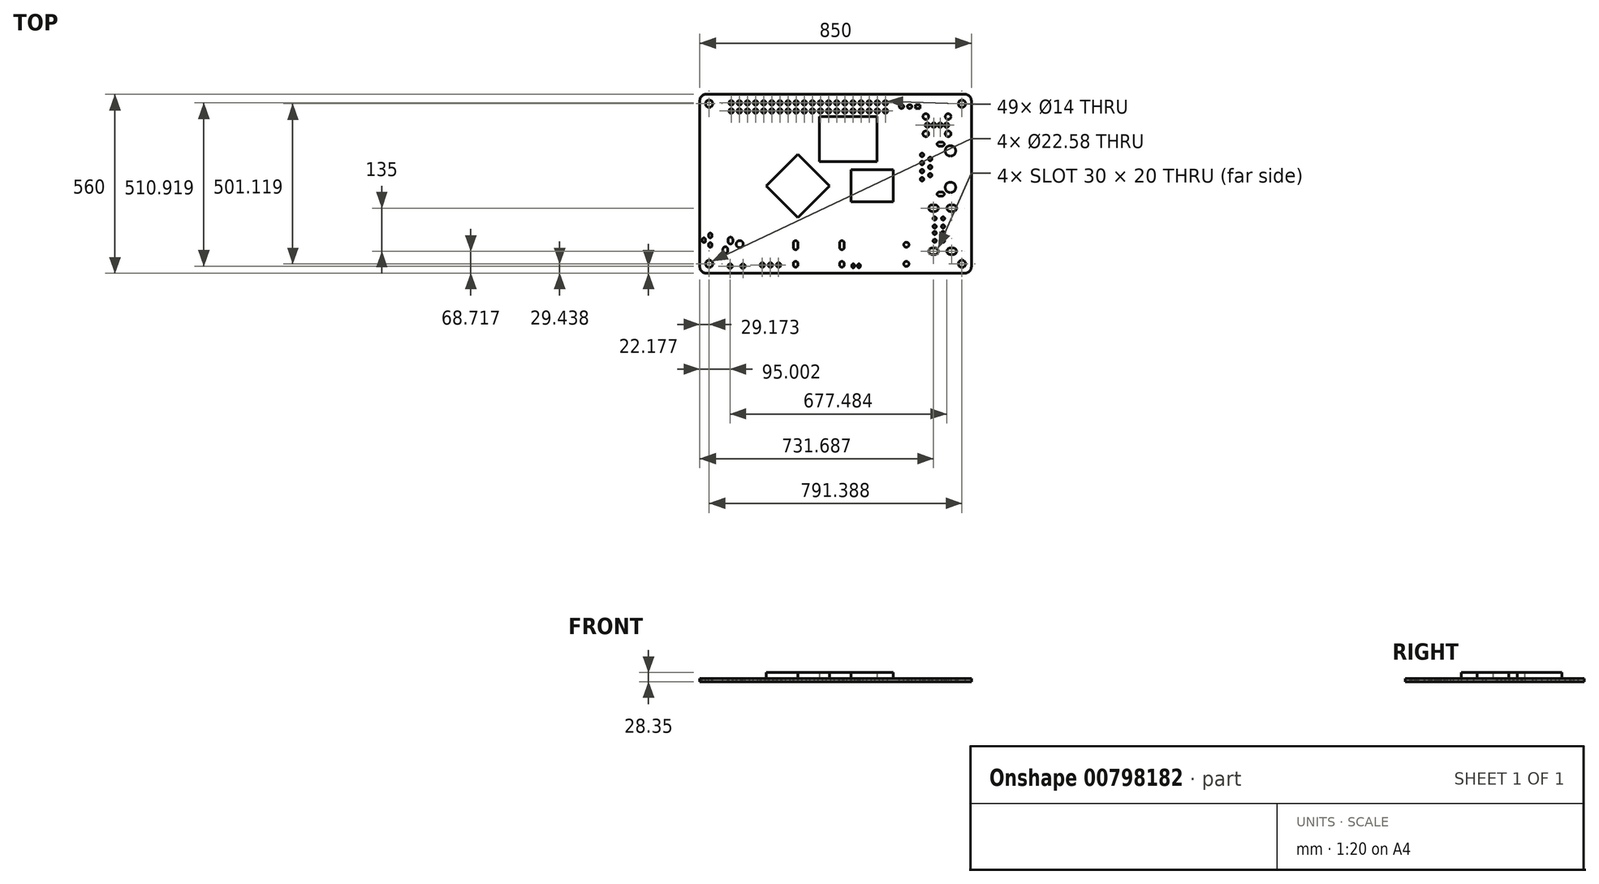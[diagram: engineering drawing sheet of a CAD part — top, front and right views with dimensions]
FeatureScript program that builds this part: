
annotation { "Feature Type Name" : "Feature", "Feature Type Description" : "" }
export const myFeature = defineFeature(function(context is Context, id is Id, definition is map)
    precondition{}
    {
        {
            var Q0;
            Q0=qCreatedBy(makeId("Top.planeOp"),FACE);
            var sketch = newSketch(context, id + "F0", { "sketchPlane" : qUnion([Q0])});
            skCircle(sketch, "E0", {"center": v(1575.33, 490.02) * mm, "radius": 27.56 * mm});
            skCircle(sketch, "E1", {"center": v(1575.33, 390.02) * mm, "radius": 27.56 * mm});
            skCircle(sketch, "E2", {"center": v(1575.33, 67.98) * mm, "radius": 27.56 * mm});
            skCircle(sketch, "E3", {"center": v(1575.33, -32.02) * mm, "radius": 27.56 * mm});
            skCircle(sketch, "E4", {"center": v(1415.5, 454) * mm, "radius": 65 * mm});
            skCircle(sketch, "E5", {"center": v(1415.5, 4) * mm, "radius": 65 * mm});
            skLineSegment(sketch, "E6", {"start": v(1275.73, 560.7) * mm, "end": v(1315.1, 560.7) * mm});
            skArc(sketch, "E7", {"start": v(1315.1, 560.7) * mm, "mid": v(1338.72, 537.07) * mm, "end": v(1315.1, 513.45) * mm});
            skLineSegment(sketch, "E8", {"start": v(1315.1, 513.45) * mm, "end": v(1275.73, 513.45) * mm});
            skArc(sketch, "E9", {"start": v(1275.73, 513.45) * mm, "mid": v(1252.1, 537.07) * mm, "end": v(1275.73, 560.7) * mm});
            skLineSegment(sketch, "E10", {"start": v(1275.73, -55.45) * mm, "end": v(1315.1, -55.45) * mm});
            skArc(sketch, "E11", {"start": v(1315.1, -55.45) * mm, "mid": v(1338.72, -79.07) * mm, "end": v(1315.1, -102.7) * mm});
            skLineSegment(sketch, "E12", {"start": v(1315.1, -102.7) * mm, "end": v(1275.73, -102.7) * mm});
            skArc(sketch, "E13", {"start": v(1275.73, -102.7) * mm, "mid": v(1252.1, -79.07) * mm, "end": v(1275.73, -55.45) * mm});
            skCircle(sketch, "E14", {"center": v(1165.5, 354) * mm, "radius": 21.65 * mm});
            skCircle(sketch, "E15", {"center": v(1165.5, 254) * mm, "radius": 21.65 * mm});
            skCircle(sketch, "E16", {"center": v(1165.5, 154) * mm, "radius": 21.65 * mm});
            skCircle(sketch, "E17", {"center": v(1065.5, 404) * mm, "radius": 21.65 * mm});
            skCircle(sketch, "E18", {"center": v(1065.5, 304) * mm, "radius": 21.65 * mm});
            skCircle(sketch, "E19", {"center": v(1065.5, 204) * mm, "radius": 21.65 * mm});
            skCircle(sketch, "E20", {"center": v(1065.5, 104) * mm, "radius": 21.65 * mm});
            skLineSegment(sketch, "E21", {"start": v(1187.15, 32.35) * mm, "end": v(1143.84, 32.35) * mm});
            skLineSegment(sketch, "E22", {"start": v(1143.84, 32.35) * mm, "end": v(1143.84, 75.65) * mm});
            skLineSegment(sketch, "E23", {"start": v(1143.84, 75.65) * mm, "end": v(1187.15, 75.65) * mm});
            skLineSegment(sketch, "E24", {"start": v(1187.15, 75.65) * mm, "end": v(1187.15, 32.35) * mm});
            skLineSegment(sketch, "E25", {"start": v(1651.71, 484.9) * mm, "end": v(1691.08, 484.9) * mm});
            skLineSegment(sketch, "E26", {"start": v(1671.4, 465.22) * mm, "end": v(1671.4, 504.6) * mm});
            skLineSegment(sketch, "E27", {"start": v(1651.71, -26.9) * mm, "end": v(1691.08, -26.9) * mm});
            skLineSegment(sketch, "E28", {"start": v(1671.4, -46.6) * mm, "end": v(1671.4, -7.22) * mm});
            skLineSegment(sketch, "E29", {"start": v(990.5, -76) * mm, "end": v(1840.5, -76) * mm});
            skLineSegment(sketch, "E30", {"start": v(1840.5, -76) * mm, "end": v(1840.5, 534) * mm});
            skLineSegment(sketch, "E31", {"start": v(1840.5, 534) * mm, "end": v(990.5, 534) * mm});
            skLineSegment(sketch, "E32", {"start": v(990.5, 534) * mm, "end": v(990.5, -76) * mm});
            skLineSegment(sketch, "E33", {"start": v(-197.69, 323.24) * mm, "end": v(-197.69, 874.44) * mm});
            skLineSegment(sketch, "E34", {"start": v(-197.69, 874.44) * mm, "end": v(511.01, 874.44) * mm});
            skLineSegment(sketch, "E35", {"start": v(511.01, 874.44) * mm, "end": v(511.01, 323.24) * mm});
            skLineSegment(sketch, "E36", {"start": v(511.01, 323.24) * mm, "end": v(-197.69, 323.24) * mm});
            skLineSegment(sketch, "E37", {"start": v(-197.39, 356.84) * mm, "end": v(-164.39, 323.84) * mm});
            skLineSegment(sketch, "E38", {"start": v(-164.39, 323.84) * mm, "end": v(-168.39, 323.84) * mm});
            skLineSegment(sketch, "E39", {"start": v(-168.39, 323.84) * mm, "end": v(-195.39, 350.84) * mm});
            skLineSegment(sketch, "E40", {"start": v(-195.39, 350.84) * mm, "end": v(-195.39, 346.84) * mm});
            skLineSegment(sketch, "E41", {"start": v(-195.39, 346.84) * mm, "end": v(-173.39, 324.84) * mm});
            skLineSegment(sketch, "E42", {"start": v(-173.39, 324.84) * mm, "end": v(-178.39, 324.84) * mm});
            skLineSegment(sketch, "E43", {"start": v(-178.39, 324.84) * mm, "end": v(-196.39, 342.84) * mm});
            skLineSegment(sketch, "E44", {"start": v(-196.39, 342.84) * mm, "end": v(-196.39, 337.84) * mm});
            skLineSegment(sketch, "E45", {"start": v(-196.39, 337.84) * mm, "end": v(-182.39, 323.84) * mm});
            skLineSegment(sketch, "E46", {"start": v(-182.39, 323.84) * mm, "end": v(-188.39, 323.84) * mm});
            skLineSegment(sketch, "E47", {"start": v(-188.39, 323.84) * mm, "end": v(-196.39, 331.84) * mm});
            skLineSegment(sketch, "E48", {"start": v(-196.39, 331.84) * mm, "end": v(-196.39, 328.84) * mm});
            skLineSegment(sketch, "E49", {"start": v(-196.39, 328.84) * mm, "end": v(-191.39, 323.84) * mm});
            skArc(sketch, "E50", {"start": v(1771.65, -246.84) * mm, "mid": v(1785.56, -252.6) * mm, "end": v(1791.32, -266.52) * mm});
            skArc(sketch, "E51", {"start": v(1791.32, -266.52) * mm, "mid": v(1785.56, -280.44) * mm, "end": v(1771.65, -286.2) * mm});
            skArc(sketch, "E52", {"start": v(1771.65, -286.2) * mm, "mid": v(1757.73, -280.44) * mm, "end": v(1751.97, -266.52) * mm});
            skArc(sketch, "E53", {"start": v(1751.97, -266.52) * mm, "mid": v(1757.73, -252.6) * mm, "end": v(1771.65, -246.84) * mm});
            skArc(sketch, "E54", {"start": v(1732.28, -660.25) * mm, "mid": v(1743.8, -632.41) * mm, "end": v(1771.64, -620.88) * mm});
            skArc(sketch, "E55", {"start": v(1771.65, -620.88) * mm, "mid": v(1799.48, -632.41) * mm, "end": v(1811.01, -660.25) * mm});
            skArc(sketch, "E56", {"start": v(1771.65, -699.62) * mm, "mid": v(1743.8, -688.1) * mm, "end": v(1732.28, -660.25) * mm});
            skArc(sketch, "E57", {"start": v(1811.01, -660.25) * mm, "mid": v(1799.48, -688.1) * mm, "end": v(1771.64, -699.62) * mm});
            skLineSegment(sketch, "E58", {"start": v(-1594.49, 1150.77) * mm, "end": v(1594.49, 1150.77) * mm});
            skArc(sketch, "E59", {"start": v(1594.49, 1150.77) * mm, "mid": v(1650.16, 1127.7) * mm, "end": v(1673.22, 1072.03) * mm});
            skLineSegment(sketch, "E60", {"start": v(1673.22, 1072.03) * mm, "end": v(1673.22, -975.21) * mm});
            skArc(sketch, "E61", {"start": v(1673.22, -975.21) * mm, "mid": v(1650.16, -1030.89) * mm, "end": v(1594.49, -1053.95) * mm});
            skLineSegment(sketch, "E62", {"start": v(1594.49, -1053.95) * mm, "end": v(-1594.49, -1053.95) * mm});
            skArc(sketch, "E63", {"start": v(-1594.49, -1053.95) * mm, "mid": v(-1650.16, -1030.89) * mm, "end": v(-1673.22, -975.21) * mm});
            skArc(sketch, "E64", {"start": v(-1673.22, 1072.03) * mm, "mid": v(-1650.16, 1127.7) * mm, "end": v(-1594.49, 1150.77) * mm});
            skLineSegment(sketch, "E65", {"start": v(-1629.3, 698.95) * mm, "end": v(-1629.3, 738.32) * mm});
            skLineSegment(sketch, "E66", {"start": v(-1629.3, 738.32) * mm, "end": v(-1550.56, 738.32) * mm});
            skLineSegment(sketch, "E67", {"start": v(-1550.56, 738.32) * mm, "end": v(-1550.56, 698.95) * mm});
            skLineSegment(sketch, "E68", {"start": v(-1550.56, 698.95) * mm, "end": v(-1629.3, 698.95) * mm});
            skLineSegment(sketch, "E69", {"start": v(-1629.3, 815.1) * mm, "end": v(-1629.3, 854.46) * mm});
            skLineSegment(sketch, "E70", {"start": v(-1629.3, 854.46) * mm, "end": v(-1550.56, 854.46) * mm});
            skLineSegment(sketch, "E71", {"start": v(-1550.56, 854.46) * mm, "end": v(-1550.56, 815.1) * mm});
            skLineSegment(sketch, "E72", {"start": v(-1550.56, 815.1) * mm, "end": v(-1629.3, 815.1) * mm});
            skLineSegment(sketch, "E73", {"start": v(-1545.55, 756.04) * mm, "end": v(-1545.55, 797.38) * mm});
            skLineSegment(sketch, "E74", {"start": v(-1545.55, 797.38) * mm, "end": v(-1506.18, 797.38) * mm});
            skLineSegment(sketch, "E75", {"start": v(-1506.18, 797.38) * mm, "end": v(-1506.18, 756.04) * mm});
            skLineSegment(sketch, "E76", {"start": v(-1506.18, 756.04) * mm, "end": v(-1545.55, 756.04) * mm});
            skLineSegment(sketch, "E77", {"start": v(-197.36, -502.66) * mm, "end": v(-181.38, -502.66) * mm});
            skLineSegment(sketch, "E78", {"start": v(-181.38, -502.66) * mm, "end": v(-181.38, -542.66) * mm});
            skLineSegment(sketch, "E79", {"start": v(-181.38, -542.66) * mm, "end": v(-197.36, -542.66) * mm});
            skLineSegment(sketch, "E80", {"start": v(-197.36, -542.66) * mm, "end": v(-197.36, -502.66) * mm});
            skLineSegment(sketch, "E81", {"start": v(-154.92, -502.97) * mm, "end": v(-145.08, -502.97) * mm});
            skLineSegment(sketch, "E82", {"start": v(-145.08, -502.97) * mm, "end": v(-145.08, -542.34) * mm});
            skLineSegment(sketch, "E83", {"start": v(-145.08, -542.34) * mm, "end": v(-154.92, -542.34) * mm});
            skLineSegment(sketch, "E84", {"start": v(-154.92, -542.34) * mm, "end": v(-154.92, -502.97) * mm});
            skLineSegment(sketch, "E85", {"start": v(-174.6, -502.97) * mm, "end": v(-164.76, -502.97) * mm});
            skLineSegment(sketch, "E86", {"start": v(-164.76, -502.97) * mm, "end": v(-164.76, -542.34) * mm});
            skLineSegment(sketch, "E87", {"start": v(-164.76, -542.34) * mm, "end": v(-174.6, -542.34) * mm});
            skLineSegment(sketch, "E88", {"start": v(-174.6, -542.34) * mm, "end": v(-174.6, -502.97) * mm});
            skLineSegment(sketch, "E89", {"start": v(-213.98, -550.2) * mm, "end": v(-204.14, -550.2) * mm});
            skLineSegment(sketch, "E90", {"start": v(-204.14, -550.2) * mm, "end": v(-204.14, -589.58) * mm});
            skLineSegment(sketch, "E91", {"start": v(-204.14, -589.58) * mm, "end": v(-213.98, -589.58) * mm});
            skLineSegment(sketch, "E92", {"start": v(-213.98, -589.58) * mm, "end": v(-213.98, -550.2) * mm});
            skLineSegment(sketch, "E93", {"start": v(-154.92, -550.2) * mm, "end": v(-145.08, -550.2) * mm});
            skLineSegment(sketch, "E94", {"start": v(-145.08, -550.2) * mm, "end": v(-145.08, -589.58) * mm});
            skLineSegment(sketch, "E95", {"start": v(-145.08, -589.58) * mm, "end": v(-154.92, -589.58) * mm});
            skLineSegment(sketch, "E96", {"start": v(-154.92, -589.58) * mm, "end": v(-154.92, -550.2) * mm});
            skLineSegment(sketch, "E97", {"start": v(-174.6, -550.2) * mm, "end": v(-164.76, -550.2) * mm});
            skLineSegment(sketch, "E98", {"start": v(-164.76, -550.2) * mm, "end": v(-164.76, -589.58) * mm});
            skLineSegment(sketch, "E99", {"start": v(-164.76, -589.58) * mm, "end": v(-174.6, -589.58) * mm});
            skLineSegment(sketch, "E100", {"start": v(-174.6, -589.58) * mm, "end": v(-174.6, -550.2) * mm});
            skLineSegment(sketch, "E101", {"start": v(-213.98, -502.97) * mm, "end": v(-204.14, -502.97) * mm});
            skLineSegment(sketch, "E102", {"start": v(-204.14, -502.97) * mm, "end": v(-204.14, -542.34) * mm});
            skLineSegment(sketch, "E103", {"start": v(-204.14, -542.34) * mm, "end": v(-213.98, -542.34) * mm});
            skLineSegment(sketch, "E104", {"start": v(-213.98, -542.34) * mm, "end": v(-213.98, -502.97) * mm});
            skLineSegment(sketch, "E105", {"start": v(-233.66, -502.97) * mm, "end": v(-223.82, -502.97) * mm});
            skLineSegment(sketch, "E106", {"start": v(-223.82, -502.97) * mm, "end": v(-223.82, -542.34) * mm});
            skLineSegment(sketch, "E107", {"start": v(-223.82, -542.34) * mm, "end": v(-233.66, -542.34) * mm});
            skLineSegment(sketch, "E108", {"start": v(-233.66, -542.34) * mm, "end": v(-233.66, -502.97) * mm});
            skLineSegment(sketch, "E109", {"start": v(-233.66, -550.2) * mm, "end": v(-223.82, -550.2) * mm});
            skLineSegment(sketch, "E110", {"start": v(-223.82, -550.2) * mm, "end": v(-223.82, -589.58) * mm});
            skLineSegment(sketch, "E111", {"start": v(-223.82, -589.58) * mm, "end": v(-233.66, -589.58) * mm});
            skLineSegment(sketch, "E112", {"start": v(-233.66, -589.58) * mm, "end": v(-233.66, -550.2) * mm});
            skLineSegment(sketch, "E113", {"start": v(-197.36, -549.9) * mm, "end": v(-181.38, -549.9) * mm});
            skLineSegment(sketch, "E114", {"start": v(-181.38, -549.9) * mm, "end": v(-181.38, -589.9) * mm});
            skLineSegment(sketch, "E115", {"start": v(-181.38, -589.9) * mm, "end": v(-197.36, -589.9) * mm});
            skLineSegment(sketch, "E116", {"start": v(-197.36, -589.9) * mm, "end": v(-197.36, -549.9) * mm});
            skLineSegment(sketch, "E117", {"start": v(-142.13, -526.59) * mm, "end": v(-140.16, -526.59) * mm});
            skLineSegment(sketch, "E118", {"start": v(-140.16, -526.59) * mm, "end": v(-140.16, -565.96) * mm});
            skLineSegment(sketch, "E119", {"start": v(-140.16, -565.96) * mm, "end": v(-142.13, -565.96) * mm});
            skLineSegment(sketch, "E120", {"start": v(-150, -495.1) * mm, "end": v(-140.16, -485.25) * mm});
            skLineSegment(sketch, "E121", {"start": v(-140.16, -485.25) * mm, "end": v(-159.84, -485.25) * mm});
            skLineSegment(sketch, "E122", {"start": v(-159.84, -485.25) * mm, "end": v(-150, -495.1) * mm});
            skLineSegment(sketch, "E123", {"start": v(-236.6, -526.59) * mm, "end": v(-238.58, -526.59) * mm});
            skLineSegment(sketch, "E124", {"start": v(-238.58, -526.59) * mm, "end": v(-238.58, -565.96) * mm});
            skLineSegment(sketch, "E125", {"start": v(-238.58, -565.96) * mm, "end": v(-236.6, -565.96) * mm});
            skLineSegment(sketch, "E126", {"start": v(-92.36, -502.54) * mm, "end": v(-76.38, -502.54) * mm});
            skLineSegment(sketch, "E127", {"start": v(-76.38, -502.54) * mm, "end": v(-76.38, -542.54) * mm});
            skLineSegment(sketch, "E128", {"start": v(-76.38, -542.54) * mm, "end": v(-92.36, -542.54) * mm});
            skLineSegment(sketch, "E129", {"start": v(-92.36, -542.54) * mm, "end": v(-92.36, -502.54) * mm});
            skLineSegment(sketch, "E130", {"start": v(-49.92, -502.85) * mm, "end": v(-40.08, -502.85) * mm});
            skLineSegment(sketch, "E131", {"start": v(-40.08, -502.85) * mm, "end": v(-40.08, -542.22) * mm});
            skLineSegment(sketch, "E132", {"start": v(-40.08, -542.22) * mm, "end": v(-49.92, -542.22) * mm});
            skLineSegment(sketch, "E133", {"start": v(-49.92, -542.22) * mm, "end": v(-49.92, -502.85) * mm});
            skLineSegment(sketch, "E134", {"start": v(-69.6, -502.85) * mm, "end": v(-59.76, -502.85) * mm});
            skLineSegment(sketch, "E135", {"start": v(-59.76, -502.85) * mm, "end": v(-59.76, -542.22) * mm});
            skLineSegment(sketch, "E136", {"start": v(-59.76, -542.22) * mm, "end": v(-69.6, -542.22) * mm});
            skLineSegment(sketch, "E137", {"start": v(-69.6, -542.22) * mm, "end": v(-69.6, -502.85) * mm});
            skLineSegment(sketch, "E138", {"start": v(-108.98, -550.09) * mm, "end": v(-99.14, -550.09) * mm});
            skLineSegment(sketch, "E139", {"start": v(-99.14, -550.09) * mm, "end": v(-99.14, -589.46) * mm});
            skLineSegment(sketch, "E140", {"start": v(-99.14, -589.46) * mm, "end": v(-108.98, -589.46) * mm});
            skLineSegment(sketch, "E141", {"start": v(-108.98, -589.46) * mm, "end": v(-108.98, -550.09) * mm});
            skLineSegment(sketch, "E142", {"start": v(-49.92, -550.09) * mm, "end": v(-40.08, -550.09) * mm});
            skLineSegment(sketch, "E143", {"start": v(-40.08, -550.09) * mm, "end": v(-40.08, -589.46) * mm});
            skLineSegment(sketch, "E144", {"start": v(-40.08, -589.46) * mm, "end": v(-49.92, -589.46) * mm});
            skLineSegment(sketch, "E145", {"start": v(-49.92, -589.46) * mm, "end": v(-49.92, -550.09) * mm});
            skLineSegment(sketch, "E146", {"start": v(-69.6, -550.09) * mm, "end": v(-59.76, -550.09) * mm});
            skLineSegment(sketch, "E147", {"start": v(-59.76, -550.09) * mm, "end": v(-59.76, -589.46) * mm});
            skLineSegment(sketch, "E148", {"start": v(-59.76, -589.46) * mm, "end": v(-69.6, -589.46) * mm});
            skLineSegment(sketch, "E149", {"start": v(-69.6, -589.46) * mm, "end": v(-69.6, -550.09) * mm});
            skLineSegment(sketch, "E150", {"start": v(-108.98, -502.85) * mm, "end": v(-99.14, -502.85) * mm});
            skLineSegment(sketch, "E151", {"start": v(-99.14, -502.85) * mm, "end": v(-99.14, -542.22) * mm});
            skLineSegment(sketch, "E152", {"start": v(-99.14, -542.22) * mm, "end": v(-108.98, -542.22) * mm});
            skLineSegment(sketch, "E153", {"start": v(-108.98, -542.22) * mm, "end": v(-108.98, -502.85) * mm});
            skLineSegment(sketch, "E154", {"start": v(-128.66, -502.85) * mm, "end": v(-118.82, -502.85) * mm});
            skLineSegment(sketch, "E155", {"start": v(-118.82, -502.85) * mm, "end": v(-118.82, -542.22) * mm});
            skLineSegment(sketch, "E156", {"start": v(-118.82, -542.22) * mm, "end": v(-128.66, -542.22) * mm});
            skLineSegment(sketch, "E157", {"start": v(-128.66, -542.22) * mm, "end": v(-128.66, -502.85) * mm});
            skLineSegment(sketch, "E158", {"start": v(-128.66, -550.09) * mm, "end": v(-118.82, -550.09) * mm});
            skLineSegment(sketch, "E159", {"start": v(-118.82, -550.09) * mm, "end": v(-118.82, -589.46) * mm});
            skLineSegment(sketch, "E160", {"start": v(-118.82, -589.46) * mm, "end": v(-128.66, -589.46) * mm});
            skLineSegment(sketch, "E161", {"start": v(-128.66, -589.46) * mm, "end": v(-128.66, -550.09) * mm});
            skLineSegment(sketch, "E162", {"start": v(-92.36, -549.77) * mm, "end": v(-76.38, -549.77) * mm});
            skLineSegment(sketch, "E163", {"start": v(-76.38, -549.77) * mm, "end": v(-76.38, -589.77) * mm});
            skLineSegment(sketch, "E164", {"start": v(-76.38, -589.77) * mm, "end": v(-92.36, -589.77) * mm});
            skLineSegment(sketch, "E165", {"start": v(-92.36, -589.77) * mm, "end": v(-92.36, -549.77) * mm});
            skLineSegment(sketch, "E166", {"start": v(-37.13, -526.47) * mm, "end": v(-35.16, -526.47) * mm});
            skLineSegment(sketch, "E167", {"start": v(-35.16, -526.47) * mm, "end": v(-35.16, -565.85) * mm});
            skLineSegment(sketch, "E168", {"start": v(-35.16, -565.85) * mm, "end": v(-37.13, -565.85) * mm});
            skLineSegment(sketch, "E169", {"start": v(-45, -494.98) * mm, "end": v(-35.16, -485.14) * mm});
            skLineSegment(sketch, "E170", {"start": v(-35.16, -485.14) * mm, "end": v(-54.84, -485.14) * mm});
            skLineSegment(sketch, "E171", {"start": v(-54.84, -485.14) * mm, "end": v(-45, -494.98) * mm});
            skLineSegment(sketch, "E172", {"start": v(-131.6, -526.47) * mm, "end": v(-133.58, -526.47) * mm});
            skLineSegment(sketch, "E173", {"start": v(-133.58, -526.47) * mm, "end": v(-133.58, -565.85) * mm});
            skLineSegment(sketch, "E174", {"start": v(-133.58, -565.85) * mm, "end": v(-131.6, -565.85) * mm});
            skLineSegment(sketch, "E175", {"start": v(-1042.38, 782.65) * mm, "end": v(-1042.38, 773.6) * mm});
            skLineSegment(sketch, "E176", {"start": v(-1042.38, 773.6) * mm, "end": v(-1073.88, 773.6) * mm});
            skLineSegment(sketch, "E177", {"start": v(-1073.88, 773.6) * mm, "end": v(-1073.88, 782.65) * mm});
            skLineSegment(sketch, "E178", {"start": v(-1073.88, 782.65) * mm, "end": v(-1042.38, 782.65) * mm});
            skLineSegment(sketch, "E179", {"start": v(-1042.38, 762.97) * mm, "end": v(-1042.38, 753.91) * mm});
            skLineSegment(sketch, "E180", {"start": v(-1042.38, 753.91) * mm, "end": v(-1073.88, 753.91) * mm});
            skLineSegment(sketch, "E181", {"start": v(-1073.88, 753.91) * mm, "end": v(-1073.88, 762.97) * mm});
            skLineSegment(sketch, "E182", {"start": v(-1073.88, 762.97) * mm, "end": v(-1042.38, 762.97) * mm});
            skLineSegment(sketch, "E183", {"start": v(-1042.38, 743.28) * mm, "end": v(-1042.38, 734.22) * mm});
            skLineSegment(sketch, "E184", {"start": v(-1042.38, 734.22) * mm, "end": v(-1073.88, 734.22) * mm});
            skLineSegment(sketch, "E185", {"start": v(-1073.88, 734.22) * mm, "end": v(-1073.88, 743.28) * mm});
            skLineSegment(sketch, "E186", {"start": v(-1073.88, 743.28) * mm, "end": v(-1042.38, 743.28) * mm});
            skLineSegment(sketch, "E187", {"start": v(-1042.38, 723.6) * mm, "end": v(-1042.38, 714.54) * mm});
            skLineSegment(sketch, "E188", {"start": v(-1042.38, 714.54) * mm, "end": v(-1073.88, 714.54) * mm});
            skLineSegment(sketch, "E189", {"start": v(-1073.88, 714.54) * mm, "end": v(-1073.88, 723.6) * mm});
            skLineSegment(sketch, "E190", {"start": v(-1073.88, 723.6) * mm, "end": v(-1042.38, 723.6) * mm});
            skLineSegment(sketch, "E191", {"start": v(-1042.38, 703.91) * mm, "end": v(-1042.38, 694.85) * mm});
            skLineSegment(sketch, "E192", {"start": v(-1042.38, 694.85) * mm, "end": v(-1073.88, 694.85) * mm});
            skLineSegment(sketch, "E193", {"start": v(-1073.88, 694.85) * mm, "end": v(-1073.88, 703.91) * mm});
            skLineSegment(sketch, "E194", {"start": v(-1073.88, 703.91) * mm, "end": v(-1042.38, 703.91) * mm});
            skLineSegment(sketch, "E195", {"start": v(-1042.38, 684.23) * mm, "end": v(-1042.38, 675.17) * mm});
            skLineSegment(sketch, "E196", {"start": v(-1042.38, 675.17) * mm, "end": v(-1073.88, 675.17) * mm});
            skLineSegment(sketch, "E197", {"start": v(-1073.88, 675.17) * mm, "end": v(-1073.88, 684.23) * mm});
            skLineSegment(sketch, "E198", {"start": v(-1073.88, 684.23) * mm, "end": v(-1042.38, 684.23) * mm});
            skLineSegment(sketch, "E199", {"start": v(-1092.2, 665.92) * mm, "end": v(-1083.13, 665.92) * mm});
            skLineSegment(sketch, "E200", {"start": v(-1083.13, 665.92) * mm, "end": v(-1083.13, 634.42) * mm});
            skLineSegment(sketch, "E201", {"start": v(-1083.13, 634.42) * mm, "end": v(-1092.2, 634.42) * mm});
            skLineSegment(sketch, "E202", {"start": v(-1092.2, 634.42) * mm, "end": v(-1092.2, 665.92) * mm});
            skLineSegment(sketch, "E203", {"start": v(-1111.87, 665.92) * mm, "end": v(-1102.81, 665.92) * mm});
            skLineSegment(sketch, "E204", {"start": v(-1102.81, 665.92) * mm, "end": v(-1102.81, 634.42) * mm});
            skLineSegment(sketch, "E205", {"start": v(-1102.81, 634.42) * mm, "end": v(-1111.87, 634.42) * mm});
            skLineSegment(sketch, "E206", {"start": v(-1111.87, 634.42) * mm, "end": v(-1111.87, 665.92) * mm});
            skLineSegment(sketch, "E207", {"start": v(-1131.56, 665.92) * mm, "end": v(-1122.5, 665.92) * mm});
            skLineSegment(sketch, "E208", {"start": v(-1122.5, 665.92) * mm, "end": v(-1122.5, 634.42) * mm});
            skLineSegment(sketch, "E209", {"start": v(-1122.5, 634.42) * mm, "end": v(-1131.56, 634.42) * mm});
            skLineSegment(sketch, "E210", {"start": v(-1131.56, 634.42) * mm, "end": v(-1131.56, 665.92) * mm});
            skLineSegment(sketch, "E211", {"start": v(-1151.24, 665.92) * mm, "end": v(-1142.18, 665.92) * mm});
            skLineSegment(sketch, "E212", {"start": v(-1142.18, 665.92) * mm, "end": v(-1142.18, 634.42) * mm});
            skLineSegment(sketch, "E213", {"start": v(-1142.18, 634.42) * mm, "end": v(-1151.24, 634.42) * mm});
            skLineSegment(sketch, "E214", {"start": v(-1151.24, 634.42) * mm, "end": v(-1151.24, 665.92) * mm});
            skLineSegment(sketch, "E215", {"start": v(-1170.93, 665.92) * mm, "end": v(-1161.87, 665.92) * mm});
            skLineSegment(sketch, "E216", {"start": v(-1161.87, 665.92) * mm, "end": v(-1161.87, 634.42) * mm});
            skLineSegment(sketch, "E217", {"start": v(-1161.87, 634.42) * mm, "end": v(-1170.93, 634.42) * mm});
            skLineSegment(sketch, "E218", {"start": v(-1170.93, 634.42) * mm, "end": v(-1170.93, 665.92) * mm});
            skLineSegment(sketch, "E219", {"start": v(-1190.61, 665.92) * mm, "end": v(-1181.55, 665.92) * mm});
            skLineSegment(sketch, "E220", {"start": v(-1181.55, 665.92) * mm, "end": v(-1181.55, 634.42) * mm});
            skLineSegment(sketch, "E221", {"start": v(-1181.55, 634.42) * mm, "end": v(-1190.61, 634.42) * mm});
            skLineSegment(sketch, "E222", {"start": v(-1190.61, 634.42) * mm, "end": v(-1190.61, 665.92) * mm});
            skLineSegment(sketch, "E223", {"start": v(-1199.86, 684.23) * mm, "end": v(-1199.86, 675.17) * mm});
            skLineSegment(sketch, "E224", {"start": v(-1199.86, 675.17) * mm, "end": v(-1231.36, 675.17) * mm});
            skLineSegment(sketch, "E225", {"start": v(-1231.36, 675.17) * mm, "end": v(-1231.36, 684.23) * mm});
            skLineSegment(sketch, "E226", {"start": v(-1231.36, 684.23) * mm, "end": v(-1199.86, 684.23) * mm});
            skLineSegment(sketch, "E227", {"start": v(-1199.86, 703.91) * mm, "end": v(-1199.86, 694.85) * mm});
            skLineSegment(sketch, "E228", {"start": v(-1199.86, 694.85) * mm, "end": v(-1231.36, 694.85) * mm});
            skLineSegment(sketch, "E229", {"start": v(-1231.36, 694.85) * mm, "end": v(-1231.36, 703.91) * mm});
            skLineSegment(sketch, "E230", {"start": v(-1231.36, 703.91) * mm, "end": v(-1199.86, 703.91) * mm});
            skLineSegment(sketch, "E231", {"start": v(-1199.86, 723.6) * mm, "end": v(-1199.86, 714.54) * mm});
            skLineSegment(sketch, "E232", {"start": v(-1199.86, 714.54) * mm, "end": v(-1231.36, 714.54) * mm});
            skLineSegment(sketch, "E233", {"start": v(-1231.36, 714.54) * mm, "end": v(-1231.36, 723.6) * mm});
            skLineSegment(sketch, "E234", {"start": v(-1231.36, 723.6) * mm, "end": v(-1199.86, 723.6) * mm});
            skLineSegment(sketch, "E235", {"start": v(-1199.86, 743.28) * mm, "end": v(-1199.86, 734.22) * mm});
            skLineSegment(sketch, "E236", {"start": v(-1199.86, 734.22) * mm, "end": v(-1231.36, 734.22) * mm});
            skLineSegment(sketch, "E237", {"start": v(-1231.36, 734.22) * mm, "end": v(-1231.36, 743.28) * mm});
            skLineSegment(sketch, "E238", {"start": v(-1231.36, 743.28) * mm, "end": v(-1199.86, 743.28) * mm});
            skLineSegment(sketch, "E239", {"start": v(-1199.86, 762.97) * mm, "end": v(-1199.86, 753.91) * mm});
            skLineSegment(sketch, "E240", {"start": v(-1199.86, 753.91) * mm, "end": v(-1231.36, 753.91) * mm});
            skLineSegment(sketch, "E241", {"start": v(-1231.36, 753.91) * mm, "end": v(-1231.36, 762.97) * mm});
            skLineSegment(sketch, "E242", {"start": v(-1231.36, 762.97) * mm, "end": v(-1199.86, 762.97) * mm});
            skLineSegment(sketch, "E243", {"start": v(-1199.86, 782.65) * mm, "end": v(-1199.86, 773.6) * mm});
            skLineSegment(sketch, "E244", {"start": v(-1199.86, 773.6) * mm, "end": v(-1231.36, 773.6) * mm});
            skLineSegment(sketch, "E245", {"start": v(-1231.36, 773.6) * mm, "end": v(-1231.36, 782.65) * mm});
            skLineSegment(sketch, "E246", {"start": v(-1231.36, 782.65) * mm, "end": v(-1199.86, 782.65) * mm});
            skLineSegment(sketch, "E247", {"start": v(-1190.61, 823.4) * mm, "end": v(-1181.55, 823.4) * mm});
            skLineSegment(sketch, "E248", {"start": v(-1181.55, 823.4) * mm, "end": v(-1181.55, 791.9) * mm});
            skLineSegment(sketch, "E249", {"start": v(-1181.55, 791.9) * mm, "end": v(-1190.61, 791.9) * mm});
            skLineSegment(sketch, "E250", {"start": v(-1190.61, 791.9) * mm, "end": v(-1190.61, 823.4) * mm});
            skLineSegment(sketch, "E251", {"start": v(-1170.93, 823.4) * mm, "end": v(-1161.87, 823.4) * mm});
            skLineSegment(sketch, "E252", {"start": v(-1161.87, 823.4) * mm, "end": v(-1161.87, 791.9) * mm});
            skLineSegment(sketch, "E253", {"start": v(-1161.87, 791.9) * mm, "end": v(-1170.93, 791.9) * mm});
            skLineSegment(sketch, "E254", {"start": v(-1170.93, 791.9) * mm, "end": v(-1170.93, 823.4) * mm});
            skLineSegment(sketch, "E255", {"start": v(-1151.24, 823.4) * mm, "end": v(-1142.18, 823.4) * mm});
            skLineSegment(sketch, "E256", {"start": v(-1142.18, 823.4) * mm, "end": v(-1142.18, 791.9) * mm});
            skLineSegment(sketch, "E257", {"start": v(-1142.18, 791.9) * mm, "end": v(-1151.24, 791.9) * mm});
            skLineSegment(sketch, "E258", {"start": v(-1151.24, 791.9) * mm, "end": v(-1151.24, 823.4) * mm});
            skLineSegment(sketch, "E259", {"start": v(-1131.56, 823.4) * mm, "end": v(-1122.5, 823.4) * mm});
            skLineSegment(sketch, "E260", {"start": v(-1122.5, 823.4) * mm, "end": v(-1122.5, 791.9) * mm});
            skLineSegment(sketch, "E261", {"start": v(-1122.5, 791.9) * mm, "end": v(-1131.56, 791.9) * mm});
            skLineSegment(sketch, "E262", {"start": v(-1131.56, 791.9) * mm, "end": v(-1131.56, 823.4) * mm});
            skLineSegment(sketch, "E263", {"start": v(-1111.87, 823.4) * mm, "end": v(-1102.81, 823.4) * mm});
            skLineSegment(sketch, "E264", {"start": v(-1102.81, 823.4) * mm, "end": v(-1102.81, 791.9) * mm});
            skLineSegment(sketch, "E265", {"start": v(-1102.81, 791.9) * mm, "end": v(-1111.87, 791.9) * mm});
            skLineSegment(sketch, "E266", {"start": v(-1111.87, 791.9) * mm, "end": v(-1111.87, 823.4) * mm});
            skLineSegment(sketch, "E267", {"start": v(-1092.2, 823.4) * mm, "end": v(-1083.13, 823.4) * mm});
            skLineSegment(sketch, "E268", {"start": v(-1083.13, 823.4) * mm, "end": v(-1083.13, 791.9) * mm});
            skLineSegment(sketch, "E269", {"start": v(-1083.13, 791.9) * mm, "end": v(-1092.2, 791.9) * mm});
            skLineSegment(sketch, "E270", {"start": v(-1092.2, 791.9) * mm, "end": v(-1092.2, 823.4) * mm});
            skLineSegment(sketch, "E271", {"start": v(-1093.57, 772.22) * mm, "end": v(-1093.57, 685.6) * mm});
            skLineSegment(sketch, "E272", {"start": v(-1093.57, 685.6) * mm, "end": v(-1180.18, 685.6) * mm});
            skLineSegment(sketch, "E273", {"start": v(-1180.18, 685.6) * mm, "end": v(-1180.18, 772.22) * mm});
            skLineSegment(sketch, "E274", {"start": v(-1180.18, 772.22) * mm, "end": v(-1093.57, 772.22) * mm});
            skLineSegment(sketch, "E275", {"start": v(-1226.12, 792.85) * mm, "end": v(-1226.12, 817.85) * mm});
            skLineSegment(sketch, "E276", {"start": v(-1226.12, 817.85) * mm, "end": v(-1201.12, 817.85) * mm});
            skLineSegment(sketch, "E277", {"start": v(-1047.63, 664.98) * mm, "end": v(-1047.63, 639.98) * mm});
            skLineSegment(sketch, "E278", {"start": v(-1047.63, 639.98) * mm, "end": v(-1072.63, 639.98) * mm});
            skLineSegment(sketch, "E279", {"start": v(-1201.87, 638.91) * mm, "end": v(-1226.87, 638.91) * mm});
            skLineSegment(sketch, "E280", {"start": v(-1226.87, 638.91) * mm, "end": v(-1226.87, 663.91) * mm});
            skArc(sketch, "E281", {"start": v(-1041.06, 813.91) * mm, "mid": v(-1056.87, 829.73) * mm, "end": v(-1072.68, 813.91) * mm});
            skArc(sketch, "E282", {"start": v(-1072.68, 813.91) * mm, "mid": v(-1056.87, 798.1) * mm, "end": v(-1041.06, 813.91) * mm});
            skLineSegment(sketch, "E283", {"start": v(188.84, -153.65) * mm, "end": v(188.84, -173.48) * mm});
            skLineSegment(sketch, "E284", {"start": v(188.84, -173.48) * mm, "end": v(712.46, -173.48) * mm});
            skLineSegment(sketch, "E285", {"start": v(712.46, -173.48) * mm, "end": v(712.46, -153.65) * mm});
            skLineSegment(sketch, "E286", {"start": v(188.84, -153.65) * mm, "end": v(188.84, 200.68) * mm});
            skLineSegment(sketch, "E287", {"start": v(712.46, 200.68) * mm, "end": v(712.46, -153.65) * mm});
            skLineSegment(sketch, "E288", {"start": v(188.84, 200.68) * mm, "end": v(188.84, 220.52) * mm});
            skLineSegment(sketch, "E289", {"start": v(188.84, 220.52) * mm, "end": v(712.46, 220.52) * mm});
            skLineSegment(sketch, "E290", {"start": v(712.46, 220.52) * mm, "end": v(712.46, 200.68) * mm});
            skArc(sketch, "E291", {"start": v(164.23, -183.18) * mm, "mid": v(159.31, -188.1) * mm, "end": v(154.4, -183.17) * mm});
            skArc(sketch, "E292", {"start": v(154.4, -183.17) * mm, "mid": v(159.31, -178.26) * mm, "end": v(164.23, -183.18) * mm});
            skLineSegment(sketch, "E293", {"start": v(196.71, -173.48) * mm, "end": v(188.84, -165.6) * mm});
            skLineSegment(sketch, "E294", {"start": v(204.58, -173.48) * mm, "end": v(188.84, -157.73) * mm});
            skLineSegment(sketch, "E295", {"start": v(-464.29, -366.24) * mm, "end": v(-74.53, 23.52) * mm});
            skLineSegment(sketch, "E296", {"start": v(-74.53, 23.52) * mm, "end": v(-464.28, 413.27) * mm});
            skLineSegment(sketch, "E297", {"start": v(-464.28, 413.27) * mm, "end": v(-854.04, 23.52) * mm});
            skLineSegment(sketch, "E298", {"start": v(-854.04, 23.52) * mm, "end": v(-464.29, -366.24) * mm});
            skLineSegment(sketch, "E299", {"start": v(-842.87, 12.35) * mm, "end": v(-842.87, 34.7) * mm});
            skLineSegment(sketch, "E300", {"start": v(-848.45, 17.94) * mm, "end": v(-848.45, 29.1) * mm});
            skArc(sketch, "E301", {"start": v(-844.89, -0.14) * mm, "mid": v(-849.85, -5.1) * mm, "end": v(-854.82, -0.14) * mm});
            skArc(sketch, "E302", {"start": v(-854.82, -0.14) * mm, "mid": v(-849.85, 4.82) * mm, "end": v(-844.89, -0.14) * mm});
            skLineSegment(sketch, "E303", {"start": v(-938.12, -586.35) * mm, "end": v(-916.42, -586.35) * mm});
            skArc(sketch, "E304", {"start": v(-916.42, -586.35) * mm, "mid": v(-911.52, -591.25) * mm, "end": v(-916.42, -596.15) * mm});
            skLineSegment(sketch, "E305", {"start": v(-916.42, -596.15) * mm, "end": v(-938.12, -596.15) * mm});
            skArc(sketch, "E306", {"start": v(-938.12, -596.15) * mm, "mid": v(-943.02, -591.25) * mm, "end": v(-938.12, -586.35) * mm});
            skLineSegment(sketch, "E307", {"start": v(-938.12, -604.05) * mm, "end": v(-916.42, -604.05) * mm});
            skArc(sketch, "E308", {"start": v(-916.42, -604.05) * mm, "mid": v(-911.52, -608.95) * mm, "end": v(-916.42, -613.85) * mm});
            skLineSegment(sketch, "E309", {"start": v(-916.42, -613.85) * mm, "end": v(-938.12, -613.85) * mm});
            skArc(sketch, "E310", {"start": v(-938.12, -613.85) * mm, "mid": v(-943.02, -608.95) * mm, "end": v(-938.12, -604.05) * mm});
            skLineSegment(sketch, "E311", {"start": v(-938.12, -621.75) * mm, "end": v(-916.42, -621.75) * mm});
            skArc(sketch, "E312", {"start": v(-916.42, -621.75) * mm, "mid": v(-911.52, -626.65) * mm, "end": v(-916.42, -631.55) * mm});
            skLineSegment(sketch, "E313", {"start": v(-916.42, -631.55) * mm, "end": v(-938.12, -631.55) * mm});
            skArc(sketch, "E314", {"start": v(-938.12, -631.55) * mm, "mid": v(-943.02, -626.65) * mm, "end": v(-938.12, -621.75) * mm});
            skLineSegment(sketch, "E315", {"start": v(-938.12, -639.45) * mm, "end": v(-916.42, -639.45) * mm});
            skArc(sketch, "E316", {"start": v(-916.42, -639.45) * mm, "mid": v(-911.52, -644.35) * mm, "end": v(-916.42, -649.25) * mm});
            skLineSegment(sketch, "E317", {"start": v(-916.42, -649.25) * mm, "end": v(-938.12, -649.25) * mm});
            skArc(sketch, "E318", {"start": v(-938.12, -649.25) * mm, "mid": v(-943.02, -644.35) * mm, "end": v(-938.12, -639.45) * mm});
            skLineSegment(sketch, "E319", {"start": v(-938.12, -657.16) * mm, "end": v(-916.42, -657.16) * mm});
            skArc(sketch, "E320", {"start": v(-916.42, -657.16) * mm, "mid": v(-911.52, -662.06) * mm, "end": v(-916.42, -666.95) * mm});
            skLineSegment(sketch, "E321", {"start": v(-916.42, -666.95) * mm, "end": v(-938.12, -666.95) * mm});
            skArc(sketch, "E322", {"start": v(-938.12, -666.95) * mm, "mid": v(-943.02, -662.06) * mm, "end": v(-938.12, -657.16) * mm});
            skLineSegment(sketch, "E323", {"start": v(-908.47, -696.6) * mm, "end": v(-908.47, -674.9) * mm});
            skArc(sketch, "E324", {"start": v(-908.47, -674.9) * mm, "mid": v(-903.57, -670) * mm, "end": v(-898.67, -674.9) * mm});
            skLineSegment(sketch, "E325", {"start": v(-898.67, -674.9) * mm, "end": v(-898.67, -696.6) * mm});
            skArc(sketch, "E326", {"start": v(-898.67, -696.6) * mm, "mid": v(-903.57, -701.5) * mm, "end": v(-908.47, -696.6) * mm});
            skLineSegment(sketch, "E327", {"start": v(-890.77, -696.6) * mm, "end": v(-890.77, -674.9) * mm});
            skArc(sketch, "E328", {"start": v(-890.77, -674.9) * mm, "mid": v(-885.87, -670) * mm, "end": v(-880.97, -674.9) * mm});
            skLineSegment(sketch, "E329", {"start": v(-880.97, -674.9) * mm, "end": v(-880.97, -696.6) * mm});
            skArc(sketch, "E330", {"start": v(-880.97, -696.6) * mm, "mid": v(-885.87, -701.5) * mm, "end": v(-890.77, -696.6) * mm});
            skLineSegment(sketch, "E331", {"start": v(-873.07, -696.6) * mm, "end": v(-873.07, -674.9) * mm});
            skArc(sketch, "E332", {"start": v(-873.07, -674.9) * mm, "mid": v(-868.17, -670) * mm, "end": v(-863.27, -674.9) * mm});
            skLineSegment(sketch, "E333", {"start": v(-863.27, -674.9) * mm, "end": v(-863.27, -696.6) * mm});
            skArc(sketch, "E334", {"start": v(-863.27, -696.6) * mm, "mid": v(-868.17, -701.5) * mm, "end": v(-873.07, -696.6) * mm});
            skLineSegment(sketch, "E335", {"start": v(-855.37, -696.6) * mm, "end": v(-855.37, -674.9) * mm});
            skArc(sketch, "E336", {"start": v(-855.37, -674.9) * mm, "mid": v(-850.47, -670) * mm, "end": v(-845.57, -674.9) * mm});
            skLineSegment(sketch, "E337", {"start": v(-845.57, -674.9) * mm, "end": v(-845.57, -696.6) * mm});
            skArc(sketch, "E338", {"start": v(-845.57, -696.6) * mm, "mid": v(-850.47, -701.5) * mm, "end": v(-855.37, -696.6) * mm});
            skLineSegment(sketch, "E339", {"start": v(-837.67, -696.6) * mm, "end": v(-837.67, -674.9) * mm});
            skArc(sketch, "E340", {"start": v(-837.67, -674.9) * mm, "mid": v(-832.77, -670) * mm, "end": v(-827.87, -674.9) * mm});
            skLineSegment(sketch, "E341", {"start": v(-827.87, -674.9) * mm, "end": v(-827.87, -696.6) * mm});
            skArc(sketch, "E342", {"start": v(-827.87, -696.6) * mm, "mid": v(-832.77, -701.5) * mm, "end": v(-837.67, -696.6) * mm});
            skLineSegment(sketch, "E343", {"start": v(-819.92, -657.16) * mm, "end": v(-798.22, -657.16) * mm});
            skArc(sketch, "E344", {"start": v(-798.22, -657.16) * mm, "mid": v(-793.32, -662.06) * mm, "end": v(-798.22, -666.95) * mm});
            skLineSegment(sketch, "E345", {"start": v(-798.22, -666.95) * mm, "end": v(-819.92, -666.95) * mm});
            skArc(sketch, "E346", {"start": v(-819.92, -666.95) * mm, "mid": v(-824.82, -662.06) * mm, "end": v(-819.92, -657.16) * mm});
            skLineSegment(sketch, "E347", {"start": v(-819.92, -639.45) * mm, "end": v(-798.22, -639.45) * mm});
            skArc(sketch, "E348", {"start": v(-798.22, -639.45) * mm, "mid": v(-793.32, -644.35) * mm, "end": v(-798.22, -649.25) * mm});
            skLineSegment(sketch, "E349", {"start": v(-798.22, -649.25) * mm, "end": v(-819.92, -649.25) * mm});
            skArc(sketch, "E350", {"start": v(-819.92, -649.25) * mm, "mid": v(-824.82, -644.35) * mm, "end": v(-819.92, -639.45) * mm});
            skLineSegment(sketch, "E351", {"start": v(-819.92, -621.75) * mm, "end": v(-798.22, -621.75) * mm});
            skArc(sketch, "E352", {"start": v(-798.22, -621.75) * mm, "mid": v(-793.32, -626.65) * mm, "end": v(-798.22, -631.55) * mm});
            skLineSegment(sketch, "E353", {"start": v(-798.22, -631.55) * mm, "end": v(-819.92, -631.55) * mm});
            skArc(sketch, "E354", {"start": v(-819.92, -631.55) * mm, "mid": v(-824.82, -626.65) * mm, "end": v(-819.92, -621.75) * mm});
            skLineSegment(sketch, "E355", {"start": v(-819.92, -604.05) * mm, "end": v(-798.22, -604.05) * mm});
            skArc(sketch, "E356", {"start": v(-798.22, -604.05) * mm, "mid": v(-793.32, -608.95) * mm, "end": v(-798.22, -613.85) * mm});
            skLineSegment(sketch, "E357", {"start": v(-798.22, -613.85) * mm, "end": v(-819.92, -613.85) * mm});
            skArc(sketch, "E358", {"start": v(-819.92, -613.85) * mm, "mid": v(-824.82, -608.95) * mm, "end": v(-819.92, -604.05) * mm});
            skLineSegment(sketch, "E359", {"start": v(-819.92, -586.35) * mm, "end": v(-798.22, -586.35) * mm});
            skArc(sketch, "E360", {"start": v(-798.22, -586.35) * mm, "mid": v(-793.32, -591.25) * mm, "end": v(-798.22, -596.15) * mm});
            skLineSegment(sketch, "E361", {"start": v(-798.22, -596.15) * mm, "end": v(-819.92, -596.15) * mm});
            skArc(sketch, "E362", {"start": v(-819.92, -596.15) * mm, "mid": v(-824.82, -591.25) * mm, "end": v(-819.92, -586.35) * mm});
            skLineSegment(sketch, "E363", {"start": v(-837.67, -578.4) * mm, "end": v(-837.67, -556.7) * mm});
            skArc(sketch, "E364", {"start": v(-837.67, -556.7) * mm, "mid": v(-832.77, -551.8) * mm, "end": v(-827.87, -556.7) * mm});
            skLineSegment(sketch, "E365", {"start": v(-827.87, -556.7) * mm, "end": v(-827.87, -578.4) * mm});
            skArc(sketch, "E366", {"start": v(-827.87, -578.4) * mm, "mid": v(-832.77, -583.3) * mm, "end": v(-837.67, -578.4) * mm});
            skLineSegment(sketch, "E367", {"start": v(-855.37, -578.4) * mm, "end": v(-855.37, -556.7) * mm});
            skArc(sketch, "E368", {"start": v(-855.37, -556.7) * mm, "mid": v(-850.47, -551.8) * mm, "end": v(-845.57, -556.7) * mm});
            skLineSegment(sketch, "E369", {"start": v(-845.57, -556.7) * mm, "end": v(-845.57, -578.4) * mm});
            skArc(sketch, "E370", {"start": v(-845.57, -578.4) * mm, "mid": v(-850.47, -583.3) * mm, "end": v(-855.37, -578.4) * mm});
            skLineSegment(sketch, "E371", {"start": v(-873.07, -578.4) * mm, "end": v(-873.07, -556.7) * mm});
            skArc(sketch, "E372", {"start": v(-873.07, -556.7) * mm, "mid": v(-868.17, -551.8) * mm, "end": v(-863.27, -556.7) * mm});
            skLineSegment(sketch, "E373", {"start": v(-863.27, -556.7) * mm, "end": v(-863.27, -578.4) * mm});
            skArc(sketch, "E374", {"start": v(-863.27, -578.4) * mm, "mid": v(-868.17, -583.3) * mm, "end": v(-873.07, -578.4) * mm});
            skLineSegment(sketch, "E375", {"start": v(-890.77, -578.4) * mm, "end": v(-890.77, -556.7) * mm});
            skArc(sketch, "E376", {"start": v(-890.77, -556.7) * mm, "mid": v(-885.87, -551.8) * mm, "end": v(-880.97, -556.7) * mm});
            skLineSegment(sketch, "E377", {"start": v(-880.97, -556.7) * mm, "end": v(-880.97, -578.4) * mm});
            skArc(sketch, "E378", {"start": v(-880.97, -578.4) * mm, "mid": v(-885.87, -583.3) * mm, "end": v(-890.77, -578.4) * mm});
            skLineSegment(sketch, "E379", {"start": v(-908.47, -578.4) * mm, "end": v(-908.47, -556.7) * mm});
            skArc(sketch, "E380", {"start": v(-908.47, -556.7) * mm, "mid": v(-903.57, -551.8) * mm, "end": v(-898.67, -556.7) * mm});
            skLineSegment(sketch, "E381", {"start": v(-898.67, -556.7) * mm, "end": v(-898.67, -578.4) * mm});
            skArc(sketch, "E382", {"start": v(-898.67, -578.4) * mm, "mid": v(-903.57, -583.3) * mm, "end": v(-908.47, -578.4) * mm});
            skLineSegment(sketch, "E383", {"start": v(-848.47, -646.35) * mm, "end": v(-887.87, -646.35) * mm});
            skLineSegment(sketch, "E384", {"start": v(-887.87, -646.35) * mm, "end": v(-887.87, -606.95) * mm});
            skLineSegment(sketch, "E385", {"start": v(-887.87, -606.95) * mm, "end": v(-848.47, -606.95) * mm});
            skLineSegment(sketch, "E386", {"start": v(-848.47, -606.95) * mm, "end": v(-848.47, -646.35) * mm});
            skArc(sketch, "E387", {"start": v(-951.14, -587.28) * mm, "mid": v(-963.05, -575.37) * mm, "end": v(-974.97, -587.28) * mm});
            skArc(sketch, "E388", {"start": v(-974.97, -587.28) * mm, "mid": v(-963.05, -599.2) * mm, "end": v(-951.14, -587.28) * mm});
            skCircle(sketch, "E389", {"center": v(872.83, -702.9) * mm, "radius": 31.5 * mm});
            skCircle(sketch, "E390", {"center": v(872.83, -939.11) * mm, "radius": 31.5 * mm});
            skLineSegment(sketch, "E391", {"start": v(805.9, -710.76) * mm, "end": v(687.8, -710.76) * mm});
            skLineSegment(sketch, "E392", {"start": v(687.8, -710.76) * mm, "end": v(687.8, -632.02) * mm});
            skLineSegment(sketch, "E393", {"start": v(687.8, -632.02) * mm, "end": v(805.9, -632.02) * mm});
            skLineSegment(sketch, "E394", {"start": v(805.9, -632.02) * mm, "end": v(805.9, -710.76) * mm});
            skLineSegment(sketch, "E395", {"start": v(805.9, -891.87) * mm, "end": v(687.8, -891.87) * mm});
            skLineSegment(sketch, "E396", {"start": v(687.8, -891.87) * mm, "end": v(687.8, -813.13) * mm});
            skLineSegment(sketch, "E397", {"start": v(687.8, -813.13) * mm, "end": v(805.9, -813.13) * mm});
            skLineSegment(sketch, "E398", {"start": v(805.9, -813.13) * mm, "end": v(805.9, -891.87) * mm});
            skLineSegment(sketch, "E399", {"start": v(805.9, -1017.85) * mm, "end": v(687.8, -1017.85) * mm});
            skLineSegment(sketch, "E400", {"start": v(687.8, -1017.85) * mm, "end": v(687.8, -939.11) * mm});
            skLineSegment(sketch, "E401", {"start": v(687.8, -939.11) * mm, "end": v(805.9, -939.11) * mm});
            skLineSegment(sketch, "E402", {"start": v(805.9, -939.11) * mm, "end": v(805.9, -1017.85) * mm});
            skLineSegment(sketch, "E403", {"start": v(1050, -801.31) * mm, "end": v(931.89, -801.31) * mm});
            skLineSegment(sketch, "E404", {"start": v(931.89, -801.31) * mm, "end": v(931.89, -722.57) * mm});
            skLineSegment(sketch, "E405", {"start": v(931.89, -722.57) * mm, "end": v(1050, -722.57) * mm});
            skLineSegment(sketch, "E406", {"start": v(1050, -722.57) * mm, "end": v(1050, -801.31) * mm});
            skLineSegment(sketch, "E407", {"start": v(1050, -1017.85) * mm, "end": v(931.89, -1017.85) * mm});
            skLineSegment(sketch, "E408", {"start": v(931.89, -1017.85) * mm, "end": v(931.89, -939.11) * mm});
            skLineSegment(sketch, "E409", {"start": v(931.89, -939.11) * mm, "end": v(1050, -939.11) * mm});
            skLineSegment(sketch, "E410", {"start": v(1050, -939.11) * mm, "end": v(1050, -1017.85) * mm});
            skLineSegment(sketch, "E411", {"start": v(774.4, -1135.96) * mm, "end": v(774.4, -1057.22) * mm});
            skLineSegment(sketch, "E412", {"start": v(774.4, -1057.22) * mm, "end": v(750.78, -1057.22) * mm});
            skLineSegment(sketch, "E413", {"start": v(750.78, -1057.22) * mm, "end": v(750.78, -584.78) * mm});
            skLineSegment(sketch, "E414", {"start": v(750.78, -584.78) * mm, "end": v(994.88, -584.78) * mm});
            skLineSegment(sketch, "E415", {"start": v(994.88, -584.78) * mm, "end": v(994.88, -1057.22) * mm});
            skLineSegment(sketch, "E416", {"start": v(994.88, -1057.22) * mm, "end": v(971.26, -1057.22) * mm});
            skLineSegment(sketch, "E417", {"start": v(971.26, -1057.22) * mm, "end": v(971.26, -1135.96) * mm});
            skLineSegment(sketch, "E418", {"start": v(971.26, -1135.96) * mm, "end": v(774.4, -1135.96) * mm});
            skCircle(sketch, "E419", {"center": v(1131.83, 770.35) * mm, "radius": 27.56 * mm});
            skCircle(sketch, "E420", {"center": v(1210.57, 770.35) * mm, "radius": 27.56 * mm});
            skCircle(sketch, "E421", {"center": v(1289.31, 770.35) * mm, "radius": 27.56 * mm});
            skCircle(sketch, "E422", {"center": v(1368.05, 770.35) * mm, "radius": 27.56 * mm});
            skCircle(sketch, "E423", {"center": v(1112.15, 876.65) * mm, "radius": 35.43 * mm});
            skCircle(sketch, "E424", {"center": v(1387.74, 876.65) * mm, "radius": 35.43 * mm});
            skCircle(sketch, "E425", {"center": v(1387.74, 664.05) * mm, "radius": 35.43 * mm});
            skCircle(sketch, "E426", {"center": v(1112.15, 664.05) * mm, "radius": 35.43 * mm});
            skLineSegment(sketch, "E427", {"start": v(1068.84, 922.08) * mm, "end": v(1840.5, 922.08) * mm});
            skLineSegment(sketch, "E428", {"start": v(1840.5, 922.08) * mm, "end": v(1840.5, 618.61) * mm});
            skLineSegment(sketch, "E429", {"start": v(1840.5, 618.61) * mm, "end": v(1068.84, 618.61) * mm});
            skLineSegment(sketch, "E430", {"start": v(1068.84, 618.61) * mm, "end": v(1068.84, 922.08) * mm});
            skLineSegment(sketch, "E431", {"start": v(-1642.2, -656.51) * mm, "end": v(-1642.2, -638.8) * mm});
            skArc(sketch, "E432", {"start": v(-1642.2, -638.8) * mm, "mid": v(-1622.52, -619.1) * mm, "end": v(-1602.83, -638.8) * mm});
            skLineSegment(sketch, "E433", {"start": v(-1602.83, -638.8) * mm, "end": v(-1602.83, -656.51) * mm});
            skArc(sketch, "E434", {"start": v(-1602.83, -656.51) * mm, "mid": v(-1622.52, -676.2) * mm, "end": v(-1642.2, -656.51) * mm});
            skLineSegment(sketch, "E435", {"start": v(-1563.46, -597.46) * mm, "end": v(-1563.46, -579.74) * mm});
            skArc(sketch, "E436", {"start": v(-1563.46, -579.74) * mm, "mid": v(-1543.78, -560.05) * mm, "end": v(-1524.1, -579.74) * mm});
            skLineSegment(sketch, "E437", {"start": v(-1524.1, -579.74) * mm, "end": v(-1524.1, -597.46) * mm});
            skArc(sketch, "E438", {"start": v(-1524.1, -597.46) * mm, "mid": v(-1543.78, -617.14) * mm, "end": v(-1563.46, -597.46) * mm});
            skLineSegment(sketch, "E439", {"start": v(-1563.46, -715.57) * mm, "end": v(-1563.46, -697.85) * mm});
            skArc(sketch, "E440", {"start": v(-1563.46, -697.85) * mm, "mid": v(-1543.78, -678.16) * mm, "end": v(-1524.1, -697.85) * mm});
            skLineSegment(sketch, "E441", {"start": v(-1524.1, -697.85) * mm, "end": v(-1524.1, -715.57) * mm});
            skArc(sketch, "E442", {"start": v(-1524.1, -715.57) * mm, "mid": v(-1543.78, -735.25) * mm, "end": v(-1563.46, -715.57) * mm});
            skLineSegment(sketch, "E443", {"start": v(-1622.52, -553.17) * mm, "end": v(-1622.52, -742.14) * mm});
            skLineSegment(sketch, "E444", {"start": v(-1622.52, -742.14) * mm, "end": v(-1504.4, -742.14) * mm});
            skLineSegment(sketch, "E445", {"start": v(-1504.4, -742.14) * mm, "end": v(-1504.4, -553.17) * mm});
            skLineSegment(sketch, "E446", {"start": v(-1504.4, -553.17) * mm, "end": v(-1622.52, -553.17) * mm});
            skLineSegment(sketch, "E447", {"start": v(-1622.52, -596.47) * mm, "end": v(-1701.26, -596.47) * mm});
            skLineSegment(sketch, "E448", {"start": v(-1701.26, -596.47) * mm, "end": v(-1701.26, -698.84) * mm});
            skLineSegment(sketch, "E449", {"start": v(-1701.26, -698.84) * mm, "end": v(-1622.52, -698.84) * mm});
            skCircle(sketch, "E450", {"center": v(606.83, -368.65) * mm, "radius": 19.68 * mm});
            skCircle(sketch, "E451", {"center": v(-1414.17, 917.35) * mm, "radius": 19.68 * mm});
            skCircle(sketch, "E452", {"center": v(1557.32, 1034.86) * mm, "radius": 98.42 * mm});
            skCircle(sketch, "E453", {"center": v(1557.32, -938.05) * mm, "radius": 98.42 * mm});
            skCircle(sketch, "E454", {"center": v(-1557.32, -938.05) * mm, "radius": 98.42 * mm});
            skCircle(sketch, "E455", {"center": v(-1557.32, 1034.86) * mm, "radius": 98.42 * mm});
            skCircle(sketch, "E456", {"center": v(1111.83, -794.65) * mm, "radius": 15 * mm});
            skArc(sketch, "E457", {"start": v(1111.83, -776.65) * mm, "mid": v(1124.56, -781.93) * mm, "end": v(1129.83, -794.65) * mm});
            skArc(sketch, "E458", {"start": v(1129.83, -794.65) * mm, "mid": v(1124.56, -807.38) * mm, "end": v(1111.83, -812.65) * mm});
            skArc(sketch, "E459", {"start": v(1111.83, -812.65) * mm, "mid": v(1099.1, -807.38) * mm, "end": v(1093.83, -794.65) * mm});
            skArc(sketch, "E460", {"start": v(1093.83, -794.65) * mm, "mid": v(1099.1, -781.93) * mm, "end": v(1111.83, -776.65) * mm});
            skCircle(sketch, "E461", {"center": v(-1434.17, 392.35) * mm, "radius": 15 * mm});
            skArc(sketch, "E462", {"start": v(-1434.17, 410.35) * mm, "mid": v(-1421.44, 405.07) * mm, "end": v(-1416.17, 392.35) * mm});
            skArc(sketch, "E463", {"start": v(-1416.17, 392.35) * mm, "mid": v(-1421.44, 379.62) * mm, "end": v(-1434.17, 374.35) * mm});
            skArc(sketch, "E464", {"start": v(-1434.17, 374.35) * mm, "mid": v(-1446.9, 379.62) * mm, "end": v(-1452.17, 392.35) * mm});
            skArc(sketch, "E465", {"start": v(-1452.17, 392.35) * mm, "mid": v(-1446.9, 405.07) * mm, "end": v(-1434.17, 410.35) * mm});
            skCircle(sketch, "E466", {"center": v(-1116.17, -262.65) * mm, "radius": 15 * mm});
            skArc(sketch, "E467", {"start": v(-1116.17, -244.65) * mm, "mid": v(-1103.44, -249.93) * mm, "end": v(-1098.17, -262.65) * mm});
            skArc(sketch, "E468", {"start": v(-1098.17, -262.65) * mm, "mid": v(-1103.44, -275.38) * mm, "end": v(-1116.17, -280.65) * mm});
            skArc(sketch, "E469", {"start": v(-1116.17, -280.65) * mm, "mid": v(-1128.9, -275.38) * mm, "end": v(-1134.17, -262.65) * mm});
            skArc(sketch, "E470", {"start": v(-1134.17, -262.65) * mm, "mid": v(-1128.9, -249.93) * mm, "end": v(-1116.17, -244.65) * mm});
            skCircle(sketch, "E471", {"center": v(-1500.17, -777.65) * mm, "radius": 15 * mm});
            skArc(sketch, "E472", {"start": v(-1500.17, -759.65) * mm, "mid": v(-1487.44, -764.93) * mm, "end": v(-1482.17, -777.65) * mm});
            skArc(sketch, "E473", {"start": v(-1482.17, -777.65) * mm, "mid": v(-1487.44, -790.38) * mm, "end": v(-1500.17, -795.65) * mm});
            skArc(sketch, "E474", {"start": v(-1500.17, -795.65) * mm, "mid": v(-1512.9, -790.38) * mm, "end": v(-1518.17, -777.65) * mm});
            skArc(sketch, "E475", {"start": v(-1518.17, -777.65) * mm, "mid": v(-1512.9, -764.93) * mm, "end": v(-1500.17, -759.65) * mm});
            skCircle(sketch, "E476", {"center": v(-770.17, 373.35) * mm, "radius": 15 * mm});
            skArc(sketch, "E477", {"start": v(-770.17, 355.35) * mm, "mid": v(-782.9, 360.62) * mm, "end": v(-788.17, 373.35) * mm});
            skArc(sketch, "E478", {"start": v(-788.17, 373.35) * mm, "mid": v(-782.9, 386.07) * mm, "end": v(-770.17, 391.35) * mm});
            skArc(sketch, "E479", {"start": v(-770.17, 391.35) * mm, "mid": v(-757.44, 386.07) * mm, "end": v(-752.17, 373.35) * mm});
            skArc(sketch, "E480", {"start": v(-752.17, 373.35) * mm, "mid": v(-757.44, 360.62) * mm, "end": v(-770.17, 355.35) * mm});
            skCircle(sketch, "E481", {"center": v(658.83, 362.35) * mm, "radius": 15 * mm});
            skArc(sketch, "E482", {"start": v(676.83, 362.35) * mm, "mid": v(671.56, 349.62) * mm, "end": v(658.83, 344.35) * mm});
            skArc(sketch, "E483", {"start": v(658.83, 344.35) * mm, "mid": v(646.1, 349.62) * mm, "end": v(640.83, 362.35) * mm});
            skArc(sketch, "E484", {"start": v(640.83, 362.35) * mm, "mid": v(646.1, 375.07) * mm, "end": v(658.83, 380.35) * mm});
            skArc(sketch, "E485", {"start": v(658.83, 380.35) * mm, "mid": v(671.56, 375.07) * mm, "end": v(676.83, 362.35) * mm});
            skCircle(sketch, "E486", {"center": v(-1056.17, -77.65) * mm, "radius": 15 * mm});
            skArc(sketch, "E487", {"start": v(-1056.17, -59.65) * mm, "mid": v(-1043.44, -64.93) * mm, "end": v(-1038.17, -77.65) * mm});
            skArc(sketch, "E488", {"start": v(-1038.17, -77.65) * mm, "mid": v(-1043.44, -90.38) * mm, "end": v(-1056.17, -95.65) * mm});
            skArc(sketch, "E489", {"start": v(-1056.17, -95.65) * mm, "mid": v(-1068.9, -90.38) * mm, "end": v(-1074.17, -77.65) * mm});
            skArc(sketch, "E490", {"start": v(-1074.17, -77.65) * mm, "mid": v(-1068.9, -64.93) * mm, "end": v(-1056.17, -59.65) * mm});
            skCircle(sketch, "E491", {"center": v(-1228.17, -562.65) * mm, "radius": 15 * mm});
            skArc(sketch, "E492", {"start": v(-1228.17, -544.65) * mm, "mid": v(-1215.44, -549.93) * mm, "end": v(-1210.17, -562.65) * mm});
            skArc(sketch, "E493", {"start": v(-1210.17, -562.65) * mm, "mid": v(-1215.44, -575.38) * mm, "end": v(-1228.17, -580.65) * mm});
            skArc(sketch, "E494", {"start": v(-1228.17, -580.65) * mm, "mid": v(-1240.9, -575.38) * mm, "end": v(-1246.17, -562.65) * mm});
            skArc(sketch, "E495", {"start": v(-1246.17, -562.65) * mm, "mid": v(-1240.9, -549.93) * mm, "end": v(-1228.17, -544.65) * mm});
            skCircle(sketch, "E496", {"center": v(-1429.17, -798.65) * mm, "radius": 15 * mm});
            skArc(sketch, "E497", {"start": v(-1429.17, -780.65) * mm, "mid": v(-1416.44, -785.93) * mm, "end": v(-1411.17, -798.65) * mm});
            skArc(sketch, "E498", {"start": v(-1411.17, -798.65) * mm, "mid": v(-1416.44, -811.38) * mm, "end": v(-1429.17, -816.65) * mm});
            skArc(sketch, "E499", {"start": v(-1429.17, -816.65) * mm, "mid": v(-1441.9, -811.38) * mm, "end": v(-1447.17, -798.65) * mm});
            skArc(sketch, "E500", {"start": v(-1447.17, -798.65) * mm, "mid": v(-1441.9, -785.93) * mm, "end": v(-1429.17, -780.65) * mm});
            skCircle(sketch, "E501", {"center": v(-785.17, -535.65) * mm, "radius": 15 * mm});
            skArc(sketch, "E502", {"start": v(-785.17, -553.65) * mm, "mid": v(-797.9, -548.38) * mm, "end": v(-803.17, -535.65) * mm});
            skArc(sketch, "E503", {"start": v(-803.17, -535.65) * mm, "mid": v(-797.9, -522.93) * mm, "end": v(-785.17, -517.65) * mm});
            skArc(sketch, "E504", {"start": v(-785.17, -517.65) * mm, "mid": v(-772.44, -522.93) * mm, "end": v(-767.17, -535.65) * mm});
            skArc(sketch, "E505", {"start": v(-767.17, -535.65) * mm, "mid": v(-772.44, -548.38) * mm, "end": v(-785.17, -553.65) * mm});
            skLineSegment(sketch, "E506", {"start": v(272.36, -971.28) * mm, "end": v(272.36, -955.53) * mm});
            skArc(sketch, "E507", {"start": v(272.36, -955.53) * mm, "mid": v(288.1, -939.78) * mm, "end": v(303.85, -955.53) * mm});
            skLineSegment(sketch, "E508", {"start": v(303.85, -955.53) * mm, "end": v(303.85, -971.28) * mm});
            skArc(sketch, "E509", {"start": v(303.85, -971.28) * mm, "mid": v(288.1, -987.02) * mm, "end": v(272.36, -971.28) * mm});
            skLineSegment(sketch, "E510", {"start": v(201.5, -971.28) * mm, "end": v(201.5, -955.53) * mm});
            skArc(sketch, "E511", {"start": v(201.5, -955.53) * mm, "mid": v(217.24, -939.78) * mm, "end": v(232.99, -955.53) * mm});
            skLineSegment(sketch, "E512", {"start": v(232.99, -955.53) * mm, "end": v(232.99, -971.28) * mm});
            skArc(sketch, "E513", {"start": v(232.99, -971.28) * mm, "mid": v(217.24, -987.02) * mm, "end": v(201.5, -971.28) * mm});
            skLineSegment(sketch, "E514", {"start": v(224.72, -896.55) * mm, "end": v(205.04, -896.55) * mm});
            skLineSegment(sketch, "E515", {"start": v(214.88, -906.4) * mm, "end": v(214.88, -886.7) * mm});
            skArc(sketch, "E516", {"start": v(343.22, -947.65) * mm, "mid": v(252.67, -857.1) * mm, "end": v(162.12, -947.65) * mm});
            skArc(sketch, "E517", {"start": v(162.12, -947.65) * mm, "mid": v(252.67, -1038.2) * mm, "end": v(343.22, -947.65) * mm});
            skLineSegment(sketch, "E518", {"start": v(-843.06, -508.48) * mm, "end": v(-1079.28, -508.48) * mm});
            skLineSegment(sketch, "E519", {"start": v(-1079.28, -508.48) * mm, "end": v(-1079.28, -410.05) * mm});
            skLineSegment(sketch, "E520", {"start": v(-1079.28, -410.05) * mm, "end": v(-843.06, -410.05) * mm});
            skLineSegment(sketch, "E521", {"start": v(-843.06, -410.05) * mm, "end": v(-843.06, -508.48) * mm});
            skLineSegment(sketch, "E522", {"start": v(-843.06, -335.25) * mm, "end": v(-1079.28, -335.25) * mm});
            skLineSegment(sketch, "E523", {"start": v(-1079.28, -335.25) * mm, "end": v(-1079.28, -236.83) * mm});
            skLineSegment(sketch, "E524", {"start": v(-1079.28, -236.83) * mm, "end": v(-843.06, -236.83) * mm});
            skLineSegment(sketch, "E525", {"start": v(-843.06, -236.83) * mm, "end": v(-843.06, -335.25) * mm});
            skLineSegment(sketch, "E526", {"start": v(-1084.2, -513.4) * mm, "end": v(-1084.2, -231.9) * mm});
            skLineSegment(sketch, "E527", {"start": v(-1084.2, -231.9) * mm, "end": v(-838.14, -231.9) * mm});
            skLineSegment(sketch, "E528", {"start": v(-838.14, -231.9) * mm, "end": v(-838.14, -513.4) * mm});
            skLineSegment(sketch, "E529", {"start": v(-838.14, -513.4) * mm, "end": v(-1084.2, -513.4) * mm});
            skLineSegment(sketch, "E530", {"start": v(-972.75, 241.76) * mm, "end": v(-972.75, 418.93) * mm});
            skLineSegment(sketch, "E531", {"start": v(-972.75, 418.93) * mm, "end": v(-905.82, 418.93) * mm});
            skLineSegment(sketch, "E532", {"start": v(-905.82, 418.93) * mm, "end": v(-905.82, 241.76) * mm});
            skLineSegment(sketch, "E533", {"start": v(-905.82, 241.76) * mm, "end": v(-972.75, 241.76) * mm});
            skLineSegment(sketch, "E534", {"start": v(-862.52, 241.76) * mm, "end": v(-862.52, 418.93) * mm});
            skLineSegment(sketch, "E535", {"start": v(-862.52, 418.93) * mm, "end": v(-795.59, 418.93) * mm});
            skLineSegment(sketch, "E536", {"start": v(-795.59, 418.93) * mm, "end": v(-795.59, 241.76) * mm});
            skLineSegment(sketch, "E537", {"start": v(-795.59, 241.76) * mm, "end": v(-862.52, 241.76) * mm});
            skLineSegment(sketch, "E538", {"start": v(-976.69, 422.87) * mm, "end": v(-791.65, 422.87) * mm});
            skLineSegment(sketch, "E539", {"start": v(-791.65, 422.87) * mm, "end": v(-791.65, 237.83) * mm});
            skLineSegment(sketch, "E540", {"start": v(-791.65, 237.83) * mm, "end": v(-976.69, 237.83) * mm});
            skLineSegment(sketch, "E541", {"start": v(-976.69, 237.83) * mm, "end": v(-976.69, 422.87) * mm});
            skLineSegment(sketch, "E542", {"start": v(-1222.75, 123.93) * mm, "end": v(-1045.59, 123.93) * mm});
            skLineSegment(sketch, "E543", {"start": v(-1045.59, 123.93) * mm, "end": v(-1045.59, 57) * mm});
            skLineSegment(sketch, "E544", {"start": v(-1045.59, 57) * mm, "end": v(-1222.75, 57) * mm});
            skLineSegment(sketch, "E545", {"start": v(-1222.75, 57) * mm, "end": v(-1222.75, 123.93) * mm});
            skLineSegment(sketch, "E546", {"start": v(-1222.75, 13.7) * mm, "end": v(-1045.59, 13.7) * mm});
            skLineSegment(sketch, "E547", {"start": v(-1045.59, 13.7) * mm, "end": v(-1045.59, -53.24) * mm});
            skLineSegment(sketch, "E548", {"start": v(-1045.59, -53.24) * mm, "end": v(-1222.75, -53.24) * mm});
            skLineSegment(sketch, "E549", {"start": v(-1222.75, -53.24) * mm, "end": v(-1222.75, 13.7) * mm});
            skLineSegment(sketch, "E550", {"start": v(-1041.65, 127.87) * mm, "end": v(-1041.65, -57.17) * mm});
            skLineSegment(sketch, "E551", {"start": v(-1041.65, -57.17) * mm, "end": v(-1226.69, -57.17) * mm});
            skLineSegment(sketch, "E552", {"start": v(-1226.69, -57.17) * mm, "end": v(-1226.69, 127.87) * mm});
            skLineSegment(sketch, "E553", {"start": v(-1226.69, 127.87) * mm, "end": v(-1041.65, 127.87) * mm});
            skLineSegment(sketch, "E554", {"start": v(548.25, 608.93) * mm, "end": v(725.41, 608.93) * mm});
            skLineSegment(sketch, "E555", {"start": v(725.41, 608.93) * mm, "end": v(725.41, 542) * mm});
            skLineSegment(sketch, "E556", {"start": v(725.41, 542) * mm, "end": v(548.25, 542) * mm});
            skLineSegment(sketch, "E557", {"start": v(548.25, 542) * mm, "end": v(548.25, 608.93) * mm});
            skLineSegment(sketch, "E558", {"start": v(548.25, 498.7) * mm, "end": v(725.41, 498.7) * mm});
            skLineSegment(sketch, "E559", {"start": v(725.41, 498.7) * mm, "end": v(725.41, 431.76) * mm});
            skLineSegment(sketch, "E560", {"start": v(725.41, 431.76) * mm, "end": v(548.25, 431.76) * mm});
            skLineSegment(sketch, "E561", {"start": v(548.25, 431.76) * mm, "end": v(548.25, 498.7) * mm});
            skLineSegment(sketch, "E562", {"start": v(729.35, 612.87) * mm, "end": v(729.35, 427.83) * mm});
            skLineSegment(sketch, "E563", {"start": v(729.35, 427.83) * mm, "end": v(544.31, 427.83) * mm});
            skLineSegment(sketch, "E564", {"start": v(544.31, 427.83) * mm, "end": v(544.31, 612.87) * mm});
            skLineSegment(sketch, "E565", {"start": v(544.31, 612.87) * mm, "end": v(729.35, 612.87) * mm});
            skLineSegment(sketch, "E566", {"start": v(1060, -390.16) * mm, "end": v(1060, -453.15) * mm});
            skLineSegment(sketch, "E567", {"start": v(1060, -453.15) * mm, "end": v(918.26, -453.15) * mm});
            skLineSegment(sketch, "E568", {"start": v(918.26, -453.15) * mm, "end": v(918.26, -390.16) * mm});
            skLineSegment(sketch, "E569", {"start": v(918.26, -390.16) * mm, "end": v(1060, -390.16) * mm});
            skLineSegment(sketch, "E570", {"start": v(847.4, -390.16) * mm, "end": v(847.4, -453.15) * mm});
            skLineSegment(sketch, "E571", {"start": v(847.4, -453.15) * mm, "end": v(705.67, -453.15) * mm});
            skLineSegment(sketch, "E572", {"start": v(705.67, -453.15) * mm, "end": v(705.67, -390.16) * mm});
            skLineSegment(sketch, "E573", {"start": v(705.67, -390.16) * mm, "end": v(847.4, -390.16) * mm});
            skLineSegment(sketch, "E574", {"start": v(752.9, -396.06) * mm, "end": v(752.9, -291.73) * mm});
            skLineSegment(sketch, "E575", {"start": v(752.9, -291.73) * mm, "end": v(981.26, -291.73) * mm});
            skLineSegment(sketch, "E576", {"start": v(981.26, -291.73) * mm, "end": v(1012.75, -323.23) * mm});
            skLineSegment(sketch, "E577", {"start": v(1012.75, -323.23) * mm, "end": v(1012.75, -396.06) * mm});
            skLineSegment(sketch, "E578", {"start": v(752.9, -447.24) * mm, "end": v(752.9, -551.58) * mm});
            skLineSegment(sketch, "E579", {"start": v(752.9, -551.58) * mm, "end": v(981.26, -551.58) * mm});
            skLineSegment(sketch, "E580", {"start": v(981.26, -551.58) * mm, "end": v(1012.75, -520.08) * mm});
            skLineSegment(sketch, "E581", {"start": v(1012.75, -520.08) * mm, "end": v(1012.75, -447.24) * mm});
            skLineSegment(sketch, "E582", {"start": v(1060, -476.77) * mm, "end": v(1020.63, -476.77) * mm});
            skLineSegment(sketch, "E583", {"start": v(1040.31, -457.09) * mm, "end": v(1040.31, -496.46) * mm});
            skLineSegment(sketch, "E584", {"start": v(747, -474.8) * mm, "end": v(707.63, -474.8) * mm});
            skLineSegment(sketch, "E585", {"start": v(804.1, -457.09) * mm, "end": v(804.1, -517.48) * mm});
            skArc(sketch, "E586", {"start": v(804.1, -517.48) * mm, "mid": v(779.52, -490.28) * mm, "end": v(763.97, -457.09) * mm});
            skLineSegment(sketch, "E587", {"start": v(763.97, -457.09) * mm, "end": v(804.1, -457.09) * mm});
            skLineSegment(sketch, "E588", {"start": v(804.1, -325.84) * mm, "end": v(804.1, -386.22) * mm});
            skLineSegment(sketch, "E589", {"start": v(804.1, -386.22) * mm, "end": v(763.98, -386.22) * mm});
            skArc(sketch, "E590", {"start": v(763.98, -386.22) * mm, "mid": v(779.53, -353.04) * mm, "end": v(804.1, -325.84) * mm});
            skCircle(sketch, "E591", {"center": v(-1299.2, -966.63) * mm, "radius": 27.56 * mm});
            skCircle(sketch, "E592", {"center": v(-1141.73, -966.63) * mm, "radius": 27.56 * mm});
            skCircle(sketch, "E593", {"center": v(-1181.1, -694.98) * mm, "radius": 43.3 * mm});
            skLineSegment(sketch, "E594", {"start": v(-1265.74, -639.86) * mm, "end": v(-1265.74, -663.48) * mm});
            skArc(sketch, "E595", {"start": v(-1265.74, -663.48) * mm, "mid": v(-1295.27, -693) * mm, "end": v(-1324.8, -663.48) * mm});
            skLineSegment(sketch, "E596", {"start": v(-1324.8, -663.48) * mm, "end": v(-1324.8, -639.86) * mm});
            skArc(sketch, "E597", {"start": v(-1324.8, -639.86) * mm, "mid": v(-1295.27, -610.33) * mm, "end": v(-1265.74, -639.86) * mm});
            skLineSegment(sketch, "E598", {"start": v(-1328.74, -757.97) * mm, "end": v(-1328.74, -781.6) * mm});
            skArc(sketch, "E599", {"start": v(-1328.74, -781.6) * mm, "mid": v(-1358.26, -811.12) * mm, "end": v(-1387.8, -781.6) * mm});
            skLineSegment(sketch, "E600", {"start": v(-1387.8, -781.6) * mm, "end": v(-1387.8, -757.97) * mm});
            skArc(sketch, "E601", {"start": v(-1387.8, -757.97) * mm, "mid": v(-1358.26, -728.44) * mm, "end": v(-1328.74, -757.97) * mm});
            skLineSegment(sketch, "E602", {"start": v(-1377.95, -1124.11) * mm, "end": v(-1062.99, -1124.11) * mm});
            skLineSegment(sketch, "E603", {"start": v(-1062.99, -1124.11) * mm, "end": v(-1062.99, -710.73) * mm});
            skLineSegment(sketch, "E604", {"start": v(-1062.99, -710.73) * mm, "end": v(-1106.3, -710.73) * mm});
            skLineSegment(sketch, "E605", {"start": v(-1106.3, -710.73) * mm, "end": v(-1106.3, -600.49) * mm});
            skLineSegment(sketch, "E606", {"start": v(-1106.3, -600.49) * mm, "end": v(-1338.58, -600.49) * mm});
            skLineSegment(sketch, "E607", {"start": v(-1338.58, -600.49) * mm, "end": v(-1338.58, -710.73) * mm});
            skLineSegment(sketch, "E608", {"start": v(-1338.58, -710.73) * mm, "end": v(-1377.95, -710.73) * mm});
            skLineSegment(sketch, "E609", {"start": v(-1377.95, -710.73) * mm, "end": v(-1377.95, -1124.11) * mm});
            skLineSegment(sketch, "E610", {"start": v(1040.34, 1021.52) * mm, "end": v(1040.34, 978.2) * mm});
            skLineSegment(sketch, "E611", {"start": v(1040.34, 978.2) * mm, "end": v(985.22, 978.2) * mm});
            skLineSegment(sketch, "E612", {"start": v(985.22, 978.2) * mm, "end": v(985.22, 1021.52) * mm});
            skLineSegment(sketch, "E613", {"start": v(985.22, 1021.52) * mm, "end": v(1040.34, 1021.52) * mm});
            skLineSegment(sketch, "E614", {"start": v(906.87, 1021.52) * mm, "end": v(918.68, 1021.52) * mm});
            skArc(sketch, "E615", {"start": v(918.68, 1021.52) * mm, "mid": v(940.34, 999.86) * mm, "end": v(918.68, 978.2) * mm});
            skLineSegment(sketch, "E616", {"start": v(918.68, 978.2) * mm, "end": v(906.87, 978.2) * mm});
            skArc(sketch, "E617", {"start": v(906.87, 978.2) * mm, "mid": v(885.22, 999.86) * mm, "end": v(906.87, 1021.52) * mm});
            skLineSegment(sketch, "E618", {"start": v(806.87, 1021.52) * mm, "end": v(818.68, 1021.52) * mm});
            skArc(sketch, "E619", {"start": v(818.68, 1021.52) * mm, "mid": v(840.34, 999.86) * mm, "end": v(818.68, 978.2) * mm});
            skLineSegment(sketch, "E620", {"start": v(818.68, 978.2) * mm, "end": v(806.87, 978.2) * mm});
            skArc(sketch, "E621", {"start": v(806.87, 978.2) * mm, "mid": v(785.22, 999.86) * mm, "end": v(806.87, 1021.52) * mm});
            skLineSegment(sketch, "E622", {"start": v(1046.64, 940.8) * mm, "end": v(778.92, 940.8) * mm});
            skLineSegment(sketch, "E623", {"start": v(778.92, 940.8) * mm, "end": v(778.92, 1106.16) * mm});
            skLineSegment(sketch, "E624", {"start": v(778.92, 1106.16) * mm, "end": v(853.72, 1106.16) * mm});
            skLineSegment(sketch, "E625", {"start": v(853.72, 1106.16) * mm, "end": v(853.72, 1145.53) * mm});
            skLineSegment(sketch, "E626", {"start": v(853.72, 1145.53) * mm, "end": v(971.83, 1145.53) * mm});
            skLineSegment(sketch, "E627", {"start": v(971.83, 1145.53) * mm, "end": v(971.83, 1106.16) * mm});
            skLineSegment(sketch, "E628", {"start": v(971.83, 1106.16) * mm, "end": v(1046.64, 1106.16) * mm});
            skLineSegment(sketch, "E629", {"start": v(1046.64, 1106.16) * mm, "end": v(1046.64, 940.8) * mm});
            skLineSegment(sketch, "E630", {"start": v(-930.08, -980.21) * mm, "end": v(-930.08, -925.1) * mm});
            skLineSegment(sketch, "E631", {"start": v(-930.08, -925.1) * mm, "end": v(-874.96, -925.1) * mm});
            skLineSegment(sketch, "E632", {"start": v(-874.96, -925.1) * mm, "end": v(-874.96, -980.21) * mm});
            skLineSegment(sketch, "E633", {"start": v(-874.96, -980.21) * mm, "end": v(-930.08, -980.21) * mm});
            skCircle(sketch, "E634", {"center": v(-802.52, -952.65) * mm, "radius": 27.56 * mm});
            skCircle(sketch, "E635", {"center": v(-702.52, -952.65) * mm, "radius": 27.56 * mm});
            skLineSegment(sketch, "E636", {"start": v(-952.52, -902.65) * mm, "end": v(-652.52, -902.65) * mm});
            skLineSegment(sketch, "E637", {"start": v(-652.52, -902.65) * mm, "end": v(-652.52, -1002.65) * mm});
            skLineSegment(sketch, "E638", {"start": v(-652.52, -1002.65) * mm, "end": v(-952.52, -1002.65) * mm});
            skLineSegment(sketch, "E639", {"start": v(-952.52, -1002.65) * mm, "end": v(-952.52, -902.65) * mm});
            skLineSegment(sketch, "E640", {"start": v(-949.76, -952.65) * mm, "end": v(-989.13, -913.28) * mm});
            skLineSegment(sketch, "E641", {"start": v(-989.13, -913.28) * mm, "end": v(-989.13, -992.02) * mm});
            skLineSegment(sketch, "E642", {"start": v(-989.13, -992.02) * mm, "end": v(-949.76, -952.65) * mm});
            skLineSegment(sketch, "E643", {"start": v(462.83, -731.34) * mm, "end": v(462.83, -675.34) * mm});
            skLineSegment(sketch, "E644", {"start": v(462.83, -675.34) * mm, "end": v(502.83, -675.34) * mm});
            skLineSegment(sketch, "E645", {"start": v(502.83, -675.34) * mm, "end": v(502.83, -731.34) * mm});
            skLineSegment(sketch, "E646", {"start": v(502.83, -731.34) * mm, "end": v(462.83, -731.34) * mm});
            skLineSegment(sketch, "E647", {"start": v(500.23, -817.96) * mm, "end": v(500.23, -761.96) * mm});
            skLineSegment(sketch, "E648", {"start": v(500.23, -761.96) * mm, "end": v(540.23, -761.96) * mm});
            skLineSegment(sketch, "E649", {"start": v(540.23, -761.96) * mm, "end": v(540.23, -817.96) * mm});
            skLineSegment(sketch, "E650", {"start": v(540.23, -817.96) * mm, "end": v(500.23, -817.96) * mm});
            skLineSegment(sketch, "E651", {"start": v(425.43, -817.96) * mm, "end": v(425.43, -761.96) * mm});
            skLineSegment(sketch, "E652", {"start": v(425.43, -761.96) * mm, "end": v(465.43, -761.96) * mm});
            skLineSegment(sketch, "E653", {"start": v(465.43, -761.96) * mm, "end": v(465.43, -817.96) * mm});
            skLineSegment(sketch, "E654", {"start": v(465.43, -817.96) * mm, "end": v(425.43, -817.96) * mm});
            skLineSegment(sketch, "E655", {"start": v(516.33, -719.1) * mm, "end": v(541.9, -719.1) * mm});
            skLineSegment(sketch, "E656", {"start": v(423.77, -719.1) * mm, "end": v(449.33, -719.1) * mm});
            skLineSegment(sketch, "E657", {"start": v(541.9, -719.1) * mm, "end": v(541.9, -748.56) * mm});
            skLineSegment(sketch, "E658", {"start": v(423.77, -748.56) * mm, "end": v(423.77, -719.1) * mm});
            skLineSegment(sketch, "E659", {"start": v(478.93, -774.21) * mm, "end": v(486.73, -774.21) * mm});
            skLineSegment(sketch, "E660", {"start": v(130.52, -519.65) * mm, "end": v(74.52, -519.65) * mm});
            skLineSegment(sketch, "E661", {"start": v(74.52, -519.65) * mm, "end": v(74.52, -479.65) * mm});
            skLineSegment(sketch, "E662", {"start": v(74.52, -479.65) * mm, "end": v(130.52, -479.65) * mm});
            skLineSegment(sketch, "E663", {"start": v(130.52, -479.65) * mm, "end": v(130.52, -519.65) * mm});
            skLineSegment(sketch, "E664", {"start": v(217.14, -482.25) * mm, "end": v(161.14, -482.25) * mm});
            skLineSegment(sketch, "E665", {"start": v(161.14, -482.25) * mm, "end": v(161.14, -442.25) * mm});
            skLineSegment(sketch, "E666", {"start": v(161.14, -442.25) * mm, "end": v(217.14, -442.25) * mm});
            skLineSegment(sketch, "E667", {"start": v(217.14, -442.25) * mm, "end": v(217.14, -482.25) * mm});
            skLineSegment(sketch, "E668", {"start": v(217.14, -557.06) * mm, "end": v(161.14, -557.06) * mm});
            skLineSegment(sketch, "E669", {"start": v(161.14, -557.06) * mm, "end": v(161.14, -517.06) * mm});
            skLineSegment(sketch, "E670", {"start": v(161.14, -517.06) * mm, "end": v(217.14, -517.06) * mm});
            skLineSegment(sketch, "E671", {"start": v(217.14, -517.06) * mm, "end": v(217.14, -557.06) * mm});
            skLineSegment(sketch, "E672", {"start": v(118.27, -466.15) * mm, "end": v(118.27, -440.6) * mm});
            skLineSegment(sketch, "E673", {"start": v(118.27, -558.71) * mm, "end": v(118.27, -533.15) * mm});
            skLineSegment(sketch, "E674", {"start": v(118.27, -440.6) * mm, "end": v(147.74, -440.6) * mm});
            skLineSegment(sketch, "E675", {"start": v(147.74, -558.71) * mm, "end": v(118.27, -558.71) * mm});
            skLineSegment(sketch, "E676", {"start": v(173.39, -503.56) * mm, "end": v(173.39, -495.75) * mm});
            skLineSegment(sketch, "E677", {"start": v(-839.06, -827.4) * mm, "end": v(-839.06, -883.4) * mm});
            skLineSegment(sketch, "E678", {"start": v(-839.06, -883.4) * mm, "end": v(-879.06, -883.4) * mm});
            skLineSegment(sketch, "E679", {"start": v(-879.06, -883.4) * mm, "end": v(-879.06, -827.4) * mm});
            skLineSegment(sketch, "E680", {"start": v(-879.06, -827.4) * mm, "end": v(-839.06, -827.4) * mm});
            skLineSegment(sketch, "E681", {"start": v(-876.46, -740.78) * mm, "end": v(-876.46, -796.78) * mm});
            skLineSegment(sketch, "E682", {"start": v(-876.46, -796.78) * mm, "end": v(-916.46, -796.78) * mm});
            skLineSegment(sketch, "E683", {"start": v(-916.46, -796.78) * mm, "end": v(-916.46, -740.78) * mm});
            skLineSegment(sketch, "E684", {"start": v(-916.46, -740.78) * mm, "end": v(-876.46, -740.78) * mm});
            skLineSegment(sketch, "E685", {"start": v(-801.66, -740.78) * mm, "end": v(-801.66, -796.78) * mm});
            skLineSegment(sketch, "E686", {"start": v(-801.66, -796.78) * mm, "end": v(-841.66, -796.78) * mm});
            skLineSegment(sketch, "E687", {"start": v(-841.66, -796.78) * mm, "end": v(-841.66, -740.78) * mm});
            skLineSegment(sketch, "E688", {"start": v(-841.66, -740.78) * mm, "end": v(-801.66, -740.78) * mm});
            skLineSegment(sketch, "E689", {"start": v(-796.07, -772.72) * mm, "end": v(-780.32, -788.48) * mm});
            skLineSegment(sketch, "E690", {"start": v(-780.32, -788.48) * mm, "end": v(-780.32, -756.98) * mm});
            skLineSegment(sketch, "E691", {"start": v(-780.32, -756.98) * mm, "end": v(-796.07, -772.72) * mm});
            skLineSegment(sketch, "E692", {"start": v(-892.56, -839.65) * mm, "end": v(-918.12, -839.65) * mm});
            skLineSegment(sketch, "E693", {"start": v(-800, -839.65) * mm, "end": v(-825.56, -839.65) * mm});
            skLineSegment(sketch, "E694", {"start": v(-918.12, -839.65) * mm, "end": v(-918.12, -810.18) * mm});
            skLineSegment(sketch, "E695", {"start": v(-800, -810.18) * mm, "end": v(-800, -839.65) * mm});
            skLineSegment(sketch, "E696", {"start": v(-855.16, -784.54) * mm, "end": v(-862.96, -784.54) * mm});
            skLineSegment(sketch, "E697", {"start": v(-904.7, 783.28) * mm, "end": v(-849.58, 783.28) * mm});
            skLineSegment(sketch, "E698", {"start": v(-849.58, 783.28) * mm, "end": v(-849.58, 738) * mm});
            skLineSegment(sketch, "E699", {"start": v(-849.58, 738) * mm, "end": v(-904.7, 738) * mm});
            skLineSegment(sketch, "E700", {"start": v(-904.7, 738) * mm, "end": v(-904.7, 783.28) * mm});
            skLineSegment(sketch, "E701", {"start": v(-1004.3, 703.36) * mm, "end": v(-949.18, 703.36) * mm});
            skLineSegment(sketch, "E702", {"start": v(-949.18, 703.36) * mm, "end": v(-949.18, 658.08) * mm});
            skLineSegment(sketch, "E703", {"start": v(-949.18, 658.08) * mm, "end": v(-1004.3, 658.08) * mm});
            skLineSegment(sketch, "E704", {"start": v(-1004.3, 658.08) * mm, "end": v(-1004.3, 703.36) * mm});
            skLineSegment(sketch, "E705", {"start": v(-1004.3, 783.28) * mm, "end": v(-949.18, 783.28) * mm});
            skLineSegment(sketch, "E706", {"start": v(-949.18, 783.28) * mm, "end": v(-949.18, 738) * mm});
            skLineSegment(sketch, "E707", {"start": v(-949.18, 738) * mm, "end": v(-1004.3, 738) * mm});
            skLineSegment(sketch, "E708", {"start": v(-1004.3, 738) * mm, "end": v(-1004.3, 783.28) * mm});
            skLineSegment(sketch, "E709", {"start": v(-904.7, 703.36) * mm, "end": v(-849.58, 703.36) * mm});
            skLineSegment(sketch, "E710", {"start": v(-849.58, 703.36) * mm, "end": v(-849.58, 658.08) * mm});
            skLineSegment(sketch, "E711", {"start": v(-849.58, 658.08) * mm, "end": v(-904.7, 658.08) * mm});
            skLineSegment(sketch, "E712", {"start": v(-904.7, 658.08) * mm, "end": v(-904.7, 703.36) * mm});
            skLineSegment(sketch, "E713", {"start": v(-993.87, 769.9) * mm, "end": v(-993.87, 671.47) * mm});
            skArc(sketch, "E714", {"start": v(-993.87, 671.47) * mm, "mid": v(-992.71, 668.69) * mm, "end": v(-989.93, 667.53) * mm});
            skLineSegment(sketch, "E715", {"start": v(-989.93, 667.53) * mm, "end": v(-863.95, 667.53) * mm});
            skArc(sketch, "E716", {"start": v(-863.95, 667.53) * mm, "mid": v(-861.16, 668.69) * mm, "end": v(-860, 671.47) * mm});
            skLineSegment(sketch, "E717", {"start": v(-860, 671.47) * mm, "end": v(-860, 769.9) * mm});
            skArc(sketch, "E718", {"start": v(-860, 769.9) * mm, "mid": v(-861.16, 772.68) * mm, "end": v(-863.95, 773.83) * mm});
            skLineSegment(sketch, "E719", {"start": v(-863.95, 773.83) * mm, "end": v(-989.93, 773.83) * mm});
            skArc(sketch, "E720", {"start": v(-989.93, 773.83) * mm, "mid": v(-992.71, 772.68) * mm, "end": v(-993.87, 769.9) * mm});
            skLineSegment(sketch, "E721", {"start": v(-931.94, 770.68) * mm, "end": v(-931.94, 730.68) * mm});
            skLineSegment(sketch, "E722", {"start": v(-931.94, 730.68) * mm, "end": v(-911.94, 750.68) * mm});
            skLineSegment(sketch, "E723", {"start": v(-911.94, 750.68) * mm, "end": v(-931.94, 770.68) * mm});
            skLineSegment(sketch, "E724", {"start": v(1326.33, 1112.75) * mm, "end": v(1374.33, 1112.75) * mm});
            skLineSegment(sketch, "E725", {"start": v(1374.33, 1112.75) * mm, "end": v(1374.33, 1086.75) * mm});
            skLineSegment(sketch, "E726", {"start": v(1374.33, 1086.75) * mm, "end": v(1326.33, 1086.75) * mm});
            skLineSegment(sketch, "E727", {"start": v(1326.33, 1086.75) * mm, "end": v(1326.33, 1112.75) * mm});
            skLineSegment(sketch, "E728", {"start": v(1326.33, 1037.94) * mm, "end": v(1374.33, 1037.94) * mm});
            skLineSegment(sketch, "E729", {"start": v(1374.33, 1037.94) * mm, "end": v(1374.33, 1011.94) * mm});
            skLineSegment(sketch, "E730", {"start": v(1374.33, 1011.94) * mm, "end": v(1326.33, 1011.94) * mm});
            skLineSegment(sketch, "E731", {"start": v(1326.33, 1011.94) * mm, "end": v(1326.33, 1037.94) * mm});
            skLineSegment(sketch, "E732", {"start": v(1211.33, 1037.94) * mm, "end": v(1259.33, 1037.94) * mm});
            skLineSegment(sketch, "E733", {"start": v(1259.33, 1037.94) * mm, "end": v(1259.33, 1011.94) * mm});
            skLineSegment(sketch, "E734", {"start": v(1259.33, 1011.94) * mm, "end": v(1211.33, 1011.94) * mm});
            skLineSegment(sketch, "E735", {"start": v(1211.33, 1011.94) * mm, "end": v(1211.33, 1037.94) * mm});
            skLineSegment(sketch, "E736", {"start": v(1211.33, 1075.35) * mm, "end": v(1259.33, 1075.35) * mm});
            skLineSegment(sketch, "E737", {"start": v(1259.33, 1075.35) * mm, "end": v(1259.33, 1049.35) * mm});
            skLineSegment(sketch, "E738", {"start": v(1259.33, 1049.35) * mm, "end": v(1211.33, 1049.35) * mm});
            skLineSegment(sketch, "E739", {"start": v(1211.33, 1049.35) * mm, "end": v(1211.33, 1075.35) * mm});
            skLineSegment(sketch, "E740", {"start": v(1211.33, 1112.75) * mm, "end": v(1259.33, 1112.75) * mm});
            skLineSegment(sketch, "E741", {"start": v(1259.33, 1112.75) * mm, "end": v(1259.33, 1086.75) * mm});
            skLineSegment(sketch, "E742", {"start": v(1259.33, 1086.75) * mm, "end": v(1211.33, 1086.75) * mm});
            skLineSegment(sketch, "E743", {"start": v(1211.33, 1086.75) * mm, "end": v(1211.33, 1112.75) * mm});
            skLineSegment(sketch, "E744", {"start": v(1317.83, 1122.35) * mm, "end": v(1317.83, 1002.35) * mm});
            skLineSegment(sketch, "E745", {"start": v(1317.83, 1002.35) * mm, "end": v(1267.83, 1002.35) * mm});
            skLineSegment(sketch, "E746", {"start": v(1267.83, 1002.35) * mm, "end": v(1267.83, 1122.35) * mm});
            skLineSegment(sketch, "E747", {"start": v(1267.83, 1122.35) * mm, "end": v(1317.83, 1122.35) * mm});
            skLineSegment(sketch, "E748", {"start": v(1234.33, -1018.06) * mm, "end": v(1186.33, -1018.06) * mm});
            skLineSegment(sketch, "E749", {"start": v(1186.33, -1018.06) * mm, "end": v(1186.33, -992.06) * mm});
            skLineSegment(sketch, "E750", {"start": v(1186.33, -992.06) * mm, "end": v(1234.33, -992.06) * mm});
            skLineSegment(sketch, "E751", {"start": v(1234.33, -992.06) * mm, "end": v(1234.33, -1018.06) * mm});
            skLineSegment(sketch, "E752", {"start": v(1234.33, -943.25) * mm, "end": v(1186.33, -943.25) * mm});
            skLineSegment(sketch, "E753", {"start": v(1186.33, -943.25) * mm, "end": v(1186.33, -917.25) * mm});
            skLineSegment(sketch, "E754", {"start": v(1186.33, -917.25) * mm, "end": v(1234.33, -917.25) * mm});
            skLineSegment(sketch, "E755", {"start": v(1234.33, -917.25) * mm, "end": v(1234.33, -943.25) * mm});
            skLineSegment(sketch, "E756", {"start": v(1349.33, -943.25) * mm, "end": v(1301.33, -943.25) * mm});
            skLineSegment(sketch, "E757", {"start": v(1301.33, -943.25) * mm, "end": v(1301.33, -917.25) * mm});
            skLineSegment(sketch, "E758", {"start": v(1301.33, -917.25) * mm, "end": v(1349.33, -917.25) * mm});
            skLineSegment(sketch, "E759", {"start": v(1349.33, -917.25) * mm, "end": v(1349.33, -943.25) * mm});
            skLineSegment(sketch, "E760", {"start": v(1349.33, -980.65) * mm, "end": v(1301.33, -980.65) * mm});
            skLineSegment(sketch, "E761", {"start": v(1301.33, -980.65) * mm, "end": v(1301.33, -954.65) * mm});
            skLineSegment(sketch, "E762", {"start": v(1301.33, -954.65) * mm, "end": v(1349.33, -954.65) * mm});
            skLineSegment(sketch, "E763", {"start": v(1349.33, -954.65) * mm, "end": v(1349.33, -980.65) * mm});
            skLineSegment(sketch, "E764", {"start": v(1349.33, -1018.06) * mm, "end": v(1301.33, -1018.06) * mm});
            skLineSegment(sketch, "E765", {"start": v(1301.33, -1018.06) * mm, "end": v(1301.33, -992.06) * mm});
            skLineSegment(sketch, "E766", {"start": v(1301.33, -992.06) * mm, "end": v(1349.33, -992.06) * mm});
            skLineSegment(sketch, "E767", {"start": v(1349.33, -992.06) * mm, "end": v(1349.33, -1018.06) * mm});
            skLineSegment(sketch, "E768", {"start": v(1242.83, -1027.65) * mm, "end": v(1242.83, -907.65) * mm});
            skLineSegment(sketch, "E769", {"start": v(1242.83, -907.65) * mm, "end": v(1292.83, -907.65) * mm});
            skLineSegment(sketch, "E770", {"start": v(1292.83, -907.65) * mm, "end": v(1292.83, -1027.65) * mm});
            skLineSegment(sketch, "E771", {"start": v(1292.83, -1027.65) * mm, "end": v(1242.83, -1027.65) * mm});
            skLineSegment(sketch, "E772", {"start": v(-1387.35, 321.25) * mm, "end": v(-1387.35, 346.25) * mm});
            skLineSegment(sketch, "E773", {"start": v(-1387.35, 346.25) * mm, "end": v(-1347.35, 346.25) * mm});
            skLineSegment(sketch, "E774", {"start": v(-1347.35, 346.25) * mm, "end": v(-1347.35, 321.25) * mm});
            skLineSegment(sketch, "E775", {"start": v(-1347.35, 321.25) * mm, "end": v(-1387.35, 321.25) * mm});
            skLineSegment(sketch, "E776", {"start": v(-1387.35, 283.85) * mm, "end": v(-1387.35, 308.85) * mm});
            skLineSegment(sketch, "E777", {"start": v(-1387.35, 308.85) * mm, "end": v(-1347.35, 308.85) * mm});
            skLineSegment(sketch, "E778", {"start": v(-1347.35, 308.85) * mm, "end": v(-1347.35, 283.85) * mm});
            skLineSegment(sketch, "E779", {"start": v(-1347.35, 283.85) * mm, "end": v(-1387.35, 283.85) * mm});
            skLineSegment(sketch, "E780", {"start": v(-1387.35, 246.44) * mm, "end": v(-1387.35, 271.44) * mm});
            skLineSegment(sketch, "E781", {"start": v(-1387.35, 271.44) * mm, "end": v(-1347.35, 271.44) * mm});
            skLineSegment(sketch, "E782", {"start": v(-1347.35, 271.44) * mm, "end": v(-1347.35, 246.44) * mm});
            skLineSegment(sketch, "E783", {"start": v(-1347.35, 246.44) * mm, "end": v(-1387.35, 246.44) * mm});
            skLineSegment(sketch, "E784", {"start": v(-1284.99, 246.44) * mm, "end": v(-1284.99, 271.44) * mm});
            skLineSegment(sketch, "E785", {"start": v(-1284.99, 271.44) * mm, "end": v(-1244.99, 271.44) * mm});
            skLineSegment(sketch, "E786", {"start": v(-1244.99, 271.44) * mm, "end": v(-1244.99, 246.44) * mm});
            skLineSegment(sketch, "E787", {"start": v(-1244.99, 246.44) * mm, "end": v(-1284.99, 246.44) * mm});
            skLineSegment(sketch, "E788", {"start": v(-1284.99, 321.25) * mm, "end": v(-1284.99, 346.25) * mm});
            skLineSegment(sketch, "E789", {"start": v(-1284.99, 346.25) * mm, "end": v(-1244.99, 346.25) * mm});
            skLineSegment(sketch, "E790", {"start": v(-1244.99, 346.25) * mm, "end": v(-1244.99, 321.25) * mm});
            skLineSegment(sketch, "E791", {"start": v(-1244.99, 321.25) * mm, "end": v(-1284.99, 321.25) * mm});
            skLineSegment(sketch, "E792", {"start": v(-1337.67, 355.85) * mm, "end": v(-1294.67, 355.85) * mm});
            skLineSegment(sketch, "E793", {"start": v(-1294.67, 355.85) * mm, "end": v(-1294.67, 236.85) * mm});
            skLineSegment(sketch, "E794", {"start": v(-1294.67, 236.85) * mm, "end": v(-1337.67, 236.85) * mm});
            skLineSegment(sketch, "E795", {"start": v(-1337.67, 236.85) * mm, "end": v(-1337.67, 355.85) * mm});
            skLineSegment(sketch, "E796", {"start": v(600.93, 646.17) * mm, "end": v(575.93, 646.17) * mm});
            skLineSegment(sketch, "E797", {"start": v(575.93, 646.17) * mm, "end": v(575.93, 686.17) * mm});
            skLineSegment(sketch, "E798", {"start": v(575.93, 686.17) * mm, "end": v(600.93, 686.17) * mm});
            skLineSegment(sketch, "E799", {"start": v(600.93, 686.17) * mm, "end": v(600.93, 646.17) * mm});
            skLineSegment(sketch, "E800", {"start": v(638.33, 646.17) * mm, "end": v(613.33, 646.17) * mm});
            skLineSegment(sketch, "E801", {"start": v(613.33, 646.17) * mm, "end": v(613.33, 686.17) * mm});
            skLineSegment(sketch, "E802", {"start": v(613.33, 686.17) * mm, "end": v(638.33, 686.17) * mm});
            skLineSegment(sketch, "E803", {"start": v(638.33, 686.17) * mm, "end": v(638.33, 646.17) * mm});
            skLineSegment(sketch, "E804", {"start": v(675.73, 646.17) * mm, "end": v(650.73, 646.17) * mm});
            skLineSegment(sketch, "E805", {"start": v(650.73, 646.17) * mm, "end": v(650.73, 686.17) * mm});
            skLineSegment(sketch, "E806", {"start": v(650.73, 686.17) * mm, "end": v(675.73, 686.17) * mm});
            skLineSegment(sketch, "E807", {"start": v(675.73, 686.17) * mm, "end": v(675.73, 646.17) * mm});
            skLineSegment(sketch, "E808", {"start": v(675.73, 748.53) * mm, "end": v(650.73, 748.53) * mm});
            skLineSegment(sketch, "E809", {"start": v(650.73, 748.53) * mm, "end": v(650.73, 788.53) * mm});
            skLineSegment(sketch, "E810", {"start": v(650.73, 788.53) * mm, "end": v(675.73, 788.53) * mm});
            skLineSegment(sketch, "E811", {"start": v(675.73, 788.53) * mm, "end": v(675.73, 748.53) * mm});
            skLineSegment(sketch, "E812", {"start": v(600.93, 748.53) * mm, "end": v(575.93, 748.53) * mm});
            skLineSegment(sketch, "E813", {"start": v(575.93, 748.53) * mm, "end": v(575.93, 788.53) * mm});
            skLineSegment(sketch, "E814", {"start": v(575.93, 788.53) * mm, "end": v(600.93, 788.53) * mm});
            skLineSegment(sketch, "E815", {"start": v(600.93, 788.53) * mm, "end": v(600.93, 748.53) * mm});
            skLineSegment(sketch, "E816", {"start": v(566.33, 695.85) * mm, "end": v(566.33, 738.85) * mm});
            skLineSegment(sketch, "E817", {"start": v(566.33, 738.85) * mm, "end": v(685.33, 738.85) * mm});
            skLineSegment(sketch, "E818", {"start": v(685.33, 738.85) * mm, "end": v(685.33, 695.85) * mm});
            skLineSegment(sketch, "E819", {"start": v(685.33, 695.85) * mm, "end": v(566.33, 695.85) * mm});
            skLineSegment(sketch, "E820", {"start": v(-930.27, 78.53) * mm, "end": v(-905.27, 78.53) * mm});
            skLineSegment(sketch, "E821", {"start": v(-905.27, 78.53) * mm, "end": v(-905.27, 38.53) * mm});
            skLineSegment(sketch, "E822", {"start": v(-905.27, 38.53) * mm, "end": v(-930.27, 38.53) * mm});
            skLineSegment(sketch, "E823", {"start": v(-930.27, 38.53) * mm, "end": v(-930.27, 78.53) * mm});
            skLineSegment(sketch, "E824", {"start": v(-967.67, 78.53) * mm, "end": v(-942.67, 78.53) * mm});
            skLineSegment(sketch, "E825", {"start": v(-942.67, 78.53) * mm, "end": v(-942.67, 38.53) * mm});
            skLineSegment(sketch, "E826", {"start": v(-942.67, 38.53) * mm, "end": v(-967.67, 38.53) * mm});
            skLineSegment(sketch, "E827", {"start": v(-967.67, 38.53) * mm, "end": v(-967.67, 78.53) * mm});
            skLineSegment(sketch, "E828", {"start": v(-1005.07, 78.53) * mm, "end": v(-980.07, 78.53) * mm});
            skLineSegment(sketch, "E829", {"start": v(-980.07, 78.53) * mm, "end": v(-980.07, 38.53) * mm});
            skLineSegment(sketch, "E830", {"start": v(-980.07, 38.53) * mm, "end": v(-1005.07, 38.53) * mm});
            skLineSegment(sketch, "E831", {"start": v(-1005.07, 38.53) * mm, "end": v(-1005.07, 78.53) * mm});
            skLineSegment(sketch, "E832", {"start": v(-1005.07, -23.83) * mm, "end": v(-980.07, -23.83) * mm});
            skLineSegment(sketch, "E833", {"start": v(-980.07, -23.83) * mm, "end": v(-980.07, -63.83) * mm});
            skLineSegment(sketch, "E834", {"start": v(-980.07, -63.83) * mm, "end": v(-1005.07, -63.83) * mm});
            skLineSegment(sketch, "E835", {"start": v(-1005.07, -63.83) * mm, "end": v(-1005.07, -23.83) * mm});
            skLineSegment(sketch, "E836", {"start": v(-930.27, -23.83) * mm, "end": v(-905.27, -23.83) * mm});
            skLineSegment(sketch, "E837", {"start": v(-905.27, -23.83) * mm, "end": v(-905.27, -63.83) * mm});
            skLineSegment(sketch, "E838", {"start": v(-905.27, -63.83) * mm, "end": v(-930.27, -63.83) * mm});
            skLineSegment(sketch, "E839", {"start": v(-930.27, -63.83) * mm, "end": v(-930.27, -23.83) * mm});
            skLineSegment(sketch, "E840", {"start": v(-895.67, 28.85) * mm, "end": v(-895.67, -14.15) * mm});
            skLineSegment(sketch, "E841", {"start": v(-895.67, -14.15) * mm, "end": v(-1014.67, -14.15) * mm});
            skLineSegment(sketch, "E842", {"start": v(-1014.67, -14.15) * mm, "end": v(-1014.67, 28.85) * mm});
            skLineSegment(sketch, "E843", {"start": v(-1014.67, 28.85) * mm, "end": v(-895.67, 28.85) * mm});
            skLineSegment(sketch, "E844", {"start": v(-998.99, 282.44) * mm, "end": v(-998.99, 257.44) * mm});
            skLineSegment(sketch, "E845", {"start": v(-998.99, 257.44) * mm, "end": v(-1038.99, 257.44) * mm});
            skLineSegment(sketch, "E846", {"start": v(-1038.99, 257.44) * mm, "end": v(-1038.99, 282.44) * mm});
            skLineSegment(sketch, "E847", {"start": v(-1038.99, 282.44) * mm, "end": v(-998.99, 282.44) * mm});
            skLineSegment(sketch, "E848", {"start": v(-998.99, 319.85) * mm, "end": v(-998.99, 294.85) * mm});
            skLineSegment(sketch, "E849", {"start": v(-998.99, 294.85) * mm, "end": v(-1038.99, 294.85) * mm});
            skLineSegment(sketch, "E850", {"start": v(-1038.99, 294.85) * mm, "end": v(-1038.99, 319.85) * mm});
            skLineSegment(sketch, "E851", {"start": v(-1038.99, 319.85) * mm, "end": v(-998.99, 319.85) * mm});
            skLineSegment(sketch, "E852", {"start": v(-998.99, 357.25) * mm, "end": v(-998.99, 332.25) * mm});
            skLineSegment(sketch, "E853", {"start": v(-998.99, 332.25) * mm, "end": v(-1038.99, 332.25) * mm});
            skLineSegment(sketch, "E854", {"start": v(-1038.99, 332.25) * mm, "end": v(-1038.99, 357.25) * mm});
            skLineSegment(sketch, "E855", {"start": v(-1038.99, 357.25) * mm, "end": v(-998.99, 357.25) * mm});
            skLineSegment(sketch, "E856", {"start": v(-1101.35, 357.25) * mm, "end": v(-1101.35, 332.25) * mm});
            skLineSegment(sketch, "E857", {"start": v(-1101.35, 332.25) * mm, "end": v(-1141.35, 332.25) * mm});
            skLineSegment(sketch, "E858", {"start": v(-1141.35, 332.25) * mm, "end": v(-1141.35, 357.25) * mm});
            skLineSegment(sketch, "E859", {"start": v(-1141.35, 357.25) * mm, "end": v(-1101.35, 357.25) * mm});
            skLineSegment(sketch, "E860", {"start": v(-1101.35, 282.44) * mm, "end": v(-1101.35, 257.44) * mm});
            skLineSegment(sketch, "E861", {"start": v(-1101.35, 257.44) * mm, "end": v(-1141.35, 257.44) * mm});
            skLineSegment(sketch, "E862", {"start": v(-1141.35, 257.44) * mm, "end": v(-1141.35, 282.44) * mm});
            skLineSegment(sketch, "E863", {"start": v(-1141.35, 282.44) * mm, "end": v(-1101.35, 282.44) * mm});
            skLineSegment(sketch, "E864", {"start": v(-1048.67, 247.85) * mm, "end": v(-1091.67, 247.85) * mm});
            skLineSegment(sketch, "E865", {"start": v(-1091.67, 247.85) * mm, "end": v(-1091.67, 366.85) * mm});
            skLineSegment(sketch, "E866", {"start": v(-1091.67, 366.85) * mm, "end": v(-1048.67, 366.85) * mm});
            skLineSegment(sketch, "E867", {"start": v(-1048.67, 366.85) * mm, "end": v(-1048.67, 247.85) * mm});
            skLineSegment(sketch, "E868", {"start": v(-1583.03, 615.46) * mm, "end": v(-1606.65, 615.46) * mm});
            skArc(sketch, "E869", {"start": v(-1606.65, 615.46) * mm, "mid": v(-1630.27, 639.08) * mm, "end": v(-1606.65, 662.7) * mm});
            skLineSegment(sketch, "E870", {"start": v(-1606.65, 662.7) * mm, "end": v(-1583.03, 662.7) * mm});
            skArc(sketch, "E871", {"start": v(-1583.03, 662.7) * mm, "mid": v(-1559.4, 639.08) * mm, "end": v(-1583.03, 615.46) * mm});
            skLineSegment(sketch, "E872", {"start": v(-1583.03, 332) * mm, "end": v(-1606.65, 332) * mm});
            skArc(sketch, "E873", {"start": v(-1606.65, 332) * mm, "mid": v(-1630.27, 355.61) * mm, "end": v(-1606.65, 379.24) * mm});
            skLineSegment(sketch, "E874", {"start": v(-1606.65, 379.24) * mm, "end": v(-1583.03, 379.24) * mm});
            skArc(sketch, "E875", {"start": v(-1583.03, 379.24) * mm, "mid": v(-1559.4, 355.61) * mm, "end": v(-1583.03, 332) * mm});
            skCircle(sketch, "E876", {"center": v(-1487.36, 592.82) * mm, "radius": 23.62 * mm});
            skCircle(sketch, "E877", {"center": v(-1487.36, 401.87) * mm, "radius": 23.62 * mm});
            skLineSegment(sketch, "E878", {"start": v(-1634.2, 536.72) * mm, "end": v(-1555.47, 536.72) * mm});
            skLineSegment(sketch, "E879", {"start": v(-1555.47, 536.72) * mm, "end": v(-1555.47, 457.98) * mm});
            skLineSegment(sketch, "E880", {"start": v(-1555.47, 457.98) * mm, "end": v(-1634.2, 457.98) * mm});
            skLineSegment(sketch, "E881", {"start": v(-1634.2, 457.98) * mm, "end": v(-1634.2, 536.72) * mm});
            skLineSegment(sketch, "E882", {"start": v(-1514.13, 556.4) * mm, "end": v(-1447.2, 556.4) * mm});
            skLineSegment(sketch, "E883", {"start": v(-1447.2, 556.4) * mm, "end": v(-1447.2, 540.65) * mm});
            skLineSegment(sketch, "E884", {"start": v(-1447.2, 540.65) * mm, "end": v(-1514.13, 540.65) * mm});
            skLineSegment(sketch, "E885", {"start": v(-1514.13, 540.65) * mm, "end": v(-1514.13, 556.4) * mm});
            skLineSegment(sketch, "E886", {"start": v(-1514.13, 530.81) * mm, "end": v(-1447.2, 530.81) * mm});
            skLineSegment(sketch, "E887", {"start": v(-1447.2, 530.81) * mm, "end": v(-1447.2, 515.06) * mm});
            skLineSegment(sketch, "E888", {"start": v(-1447.2, 515.06) * mm, "end": v(-1514.13, 515.06) * mm});
            skLineSegment(sketch, "E889", {"start": v(-1514.13, 515.06) * mm, "end": v(-1514.13, 530.81) * mm});
            skLineSegment(sketch, "E890", {"start": v(-1514.13, 505.22) * mm, "end": v(-1447.2, 505.22) * mm});
            skLineSegment(sketch, "E891", {"start": v(-1447.2, 505.22) * mm, "end": v(-1447.2, 489.47) * mm});
            skLineSegment(sketch, "E892", {"start": v(-1447.2, 489.47) * mm, "end": v(-1514.13, 489.47) * mm});
            skLineSegment(sketch, "E893", {"start": v(-1514.13, 489.47) * mm, "end": v(-1514.13, 505.22) * mm});
            skLineSegment(sketch, "E894", {"start": v(-1514.13, 479.63) * mm, "end": v(-1447.2, 479.63) * mm});
            skLineSegment(sketch, "E895", {"start": v(-1447.2, 479.63) * mm, "end": v(-1447.2, 463.88) * mm});
            skLineSegment(sketch, "E896", {"start": v(-1447.2, 463.88) * mm, "end": v(-1514.13, 463.88) * mm});
            skLineSegment(sketch, "E897", {"start": v(-1514.13, 463.88) * mm, "end": v(-1514.13, 479.63) * mm});
            skLineSegment(sketch, "E898", {"start": v(-1514.13, 454.04) * mm, "end": v(-1447.2, 454.04) * mm});
            skLineSegment(sketch, "E899", {"start": v(-1447.2, 454.04) * mm, "end": v(-1447.2, 438.3) * mm});
            skLineSegment(sketch, "E900", {"start": v(-1447.2, 438.3) * mm, "end": v(-1514.13, 438.3) * mm});
            skLineSegment(sketch, "E901", {"start": v(-1514.13, 438.3) * mm, "end": v(-1514.13, 454.04) * mm});
            skLineSegment(sketch, "E902", {"start": v(-1677.52, 347.74) * mm, "end": v(-1472.8, 347.74) * mm});
            skLineSegment(sketch, "E903", {"start": v(-1472.8, 347.74) * mm, "end": v(-1472.8, 646.95) * mm});
            skLineSegment(sketch, "E904", {"start": v(-1472.8, 646.95) * mm, "end": v(-1709.01, 646.95) * mm});
            skLineSegment(sketch, "E905", {"start": v(-1709.01, 646.95) * mm, "end": v(-1709.01, 347.74) * mm});
            skLineSegment(sketch, "E906", {"start": v(-1709.01, 347.74) * mm, "end": v(-1677.52, 347.74) * mm});
            skLineSegment(sketch, "E907", {"start": v(-1677.52, 646.95) * mm, "end": v(-1677.52, 347.74) * mm});
            skLineSegment(sketch, "E908", {"start": v(-1439.33, 548.53) * mm, "end": v(-1425.55, 562.3) * mm});
            skLineSegment(sketch, "E909", {"start": v(-1425.55, 562.3) * mm, "end": v(-1425.55, 534.75) * mm});
            skLineSegment(sketch, "E910", {"start": v(-1425.55, 534.75) * mm, "end": v(-1439.33, 548.53) * mm});
            skCircle(sketch, "E911", {"center": v(1324.35, -655.45) * mm, "radius": 19.68 * mm});
            skCircle(sketch, "E912", {"center": v(1324.35, -557.02) * mm, "radius": 19.68 * mm});
            skCircle(sketch, "E913", {"center": v(1324.35, -478.28) * mm, "radius": 19.68 * mm});
            skCircle(sketch, "E914", {"center": v(1324.35, -379.86) * mm, "radius": 19.68 * mm});
            skCircle(sketch, "E915", {"center": v(1221.2, -655.45) * mm, "radius": 19.68 * mm});
            skCircle(sketch, "E916", {"center": v(1221.2, -557.02) * mm, "radius": 19.68 * mm});
            skCircle(sketch, "E917", {"center": v(1221.2, -478.28) * mm, "radius": 19.68 * mm});
            skCircle(sketch, "E918", {"center": v(1221.2, -379.86) * mm, "radius": 19.68 * mm});
            skLineSegment(sketch, "E919", {"start": v(1450.73, -822.77) * mm, "end": v(1411.36, -822.77) * mm});
            skArc(sketch, "E920", {"start": v(1411.36, -822.77) * mm, "mid": v(1371.99, -783.4) * mm, "end": v(1411.36, -744.03) * mm});
            skLineSegment(sketch, "E921", {"start": v(1411.36, -744.03) * mm, "end": v(1450.73, -744.03) * mm});
            skArc(sketch, "E922", {"start": v(1450.73, -744.03) * mm, "mid": v(1490.1, -783.4) * mm, "end": v(1450.73, -822.77) * mm});
            skLineSegment(sketch, "E923", {"start": v(1450.73, -291.28) * mm, "end": v(1411.36, -291.28) * mm});
            skArc(sketch, "E924", {"start": v(1411.36, -291.28) * mm, "mid": v(1371.99, -251.9) * mm, "end": v(1411.36, -212.54) * mm});
            skLineSegment(sketch, "E925", {"start": v(1411.36, -212.54) * mm, "end": v(1450.73, -212.54) * mm});
            skArc(sketch, "E926", {"start": v(1450.73, -212.54) * mm, "mid": v(1490.1, -251.9) * mm, "end": v(1450.73, -291.28) * mm});
            skLineSegment(sketch, "E927", {"start": v(1227.1, -291.28) * mm, "end": v(1187.74, -291.28) * mm});
            skArc(sketch, "E928", {"start": v(1187.74, -291.28) * mm, "mid": v(1148.37, -251.9) * mm, "end": v(1187.74, -212.54) * mm});
            skLineSegment(sketch, "E929", {"start": v(1187.74, -212.54) * mm, "end": v(1227.1, -212.54) * mm});
            skArc(sketch, "E930", {"start": v(1227.1, -212.54) * mm, "mid": v(1266.48, -251.9) * mm, "end": v(1227.1, -291.28) * mm});
            skLineSegment(sketch, "E931", {"start": v(1227.1, -822.77) * mm, "end": v(1187.74, -822.77) * mm});
            skArc(sketch, "E932", {"start": v(1187.74, -822.77) * mm, "mid": v(1148.37, -783.4) * mm, "end": v(1187.74, -744.03) * mm});
            skLineSegment(sketch, "E933", {"start": v(1187.74, -744.03) * mm, "end": v(1227.1, -744.03) * mm});
            skArc(sketch, "E934", {"start": v(1227.1, -744.03) * mm, "mid": v(1266.48, -783.4) * mm, "end": v(1227.1, -822.77) * mm});
            skLineSegment(sketch, "E935", {"start": v(1840.5, -234.19) * mm, "end": v(1840.5, -801.12) * mm});
            skLineSegment(sketch, "E936", {"start": v(1840.5, -801.12) * mm, "end": v(1157.42, -801.12) * mm});
            skLineSegment(sketch, "E937", {"start": v(1157.42, -801.12) * mm, "end": v(1157.42, -234.19) * mm});
            skLineSegment(sketch, "E938", {"start": v(1157.42, -234.19) * mm, "end": v(1840.5, -234.19) * mm});
            skCircle(sketch, "E939", {"center": v(-1522.52, -312.56) * mm, "radius": 20 * mm});
            skCircle(sketch, "E940", {"center": v(-1522.52, 2.44) * mm, "radius": 20 * mm});
            skLineSegment(sketch, "E941", {"start": v(107.96, -937.5) * mm, "end": v(107.96, -949.3) * mm});
            skArc(sketch, "E942", {"start": v(107.96, -949.3) * mm, "mid": v(78.43, -978.83) * mm, "end": v(48.9, -949.3) * mm});
            skLineSegment(sketch, "E943", {"start": v(48.9, -949.3) * mm, "end": v(48.9, -937.5) * mm});
            skArc(sketch, "E944", {"start": v(48.9, -937.5) * mm, "mid": v(78.43, -907.97) * mm, "end": v(107.96, -937.5) * mm});
            skLineSegment(sketch, "E945", {"start": v(-462.9, -937.5) * mm, "end": v(-462.9, -949.3) * mm});
            skArc(sketch, "E946", {"start": v(-462.9, -949.3) * mm, "mid": v(-492.44, -978.83) * mm, "end": v(-521.96, -949.3) * mm});
            skLineSegment(sketch, "E947", {"start": v(-521.96, -949.3) * mm, "end": v(-521.96, -937.5) * mm});
            skArc(sketch, "E948", {"start": v(-521.96, -937.5) * mm, "mid": v(-492.44, -907.97) * mm, "end": v(-462.9, -937.5) * mm});
            skLineSegment(sketch, "E949", {"start": v(107.96, -683.16) * mm, "end": v(107.96, -734.35) * mm});
            skArc(sketch, "E950", {"start": v(107.96, -734.35) * mm, "mid": v(78.43, -763.87) * mm, "end": v(48.9, -734.35) * mm});
            skLineSegment(sketch, "E951", {"start": v(48.9, -734.35) * mm, "end": v(48.9, -683.16) * mm});
            skArc(sketch, "E952", {"start": v(48.9, -683.16) * mm, "mid": v(78.43, -653.64) * mm, "end": v(107.96, -683.16) * mm});
            skLineSegment(sketch, "E953", {"start": v(-462.9, -683.16) * mm, "end": v(-462.9, -734.35) * mm});
            skArc(sketch, "E954", {"start": v(-462.9, -734.35) * mm, "mid": v(-492.44, -763.87) * mm, "end": v(-521.96, -734.35) * mm});
            skLineSegment(sketch, "E955", {"start": v(-521.96, -734.35) * mm, "end": v(-521.96, -683.16) * mm});
            skArc(sketch, "E956", {"start": v(-521.96, -683.16) * mm, "mid": v(-492.44, -653.64) * mm, "end": v(-462.9, -683.16) * mm});
            skLineSegment(sketch, "E957", {"start": v(-24.33, -633.17) * mm, "end": v(-24.33, -724.5) * mm});
            skArc(sketch, "E958", {"start": v(-24.33, -724.5) * mm, "mid": v(-29.84, -730.02) * mm, "end": v(-35.35, -724.5) * mm});
            skLineSegment(sketch, "E959", {"start": v(-35.35, -724.5) * mm, "end": v(-35.35, -633.17) * mm});
            skArc(sketch, "E960", {"start": v(-35.35, -633.17) * mm, "mid": v(-29.84, -627.65) * mm, "end": v(-24.33, -633.17) * mm});
            skLineSegment(sketch, "E961", {"start": v(-44.01, -633.17) * mm, "end": v(-44.01, -724.5) * mm});
            skArc(sketch, "E962", {"start": v(-44.01, -724.5) * mm, "mid": v(-49.52, -730.02) * mm, "end": v(-55.04, -724.5) * mm});
            skLineSegment(sketch, "E963", {"start": v(-55.04, -724.5) * mm, "end": v(-55.04, -633.17) * mm});
            skArc(sketch, "E964", {"start": v(-55.04, -633.17) * mm, "mid": v(-49.52, -627.65) * mm, "end": v(-44.01, -633.17) * mm});
            skLineSegment(sketch, "E965", {"start": v(-63.7, -633.17) * mm, "end": v(-63.7, -724.5) * mm});
            skArc(sketch, "E966", {"start": v(-63.7, -724.5) * mm, "mid": v(-69.2, -730.02) * mm, "end": v(-74.72, -724.5) * mm});
            skLineSegment(sketch, "E967", {"start": v(-74.72, -724.5) * mm, "end": v(-74.72, -633.17) * mm});
            skArc(sketch, "E968", {"start": v(-74.72, -633.17) * mm, "mid": v(-69.2, -627.65) * mm, "end": v(-63.7, -633.17) * mm});
            skLineSegment(sketch, "E969", {"start": v(-83.38, -633.17) * mm, "end": v(-83.38, -724.5) * mm});
            skArc(sketch, "E970", {"start": v(-83.38, -724.5) * mm, "mid": v(-88.9, -730.02) * mm, "end": v(-94.4, -724.5) * mm});
            skLineSegment(sketch, "E971", {"start": v(-94.4, -724.5) * mm, "end": v(-94.4, -633.17) * mm});
            skArc(sketch, "E972", {"start": v(-94.4, -633.17) * mm, "mid": v(-88.9, -627.65) * mm, "end": v(-83.38, -633.17) * mm});
            skLineSegment(sketch, "E973", {"start": v(-103.07, -633.17) * mm, "end": v(-103.07, -724.5) * mm});
            skArc(sketch, "E974", {"start": v(-103.07, -724.5) * mm, "mid": v(-108.58, -730.02) * mm, "end": v(-114.1, -724.5) * mm});
            skLineSegment(sketch, "E975", {"start": v(-114.1, -724.5) * mm, "end": v(-114.1, -633.17) * mm});
            skArc(sketch, "E976", {"start": v(-114.1, -633.17) * mm, "mid": v(-108.58, -627.65) * mm, "end": v(-103.07, -633.17) * mm});
            skLineSegment(sketch, "E977", {"start": v(-122.75, -633.17) * mm, "end": v(-122.75, -724.5) * mm});
            skArc(sketch, "E978", {"start": v(-122.75, -724.5) * mm, "mid": v(-128.26, -730.02) * mm, "end": v(-133.78, -724.5) * mm});
            skLineSegment(sketch, "E979", {"start": v(-133.78, -724.5) * mm, "end": v(-133.78, -633.17) * mm});
            skArc(sketch, "E980", {"start": v(-133.78, -633.17) * mm, "mid": v(-128.26, -627.65) * mm, "end": v(-122.75, -633.17) * mm});
            skLineSegment(sketch, "E981", {"start": v(-142.44, -633.17) * mm, "end": v(-142.44, -724.5) * mm});
            skArc(sketch, "E982", {"start": v(-142.44, -724.5) * mm, "mid": v(-147.95, -730.02) * mm, "end": v(-153.46, -724.5) * mm});
            skLineSegment(sketch, "E983", {"start": v(-153.46, -724.5) * mm, "end": v(-153.46, -633.17) * mm});
            skArc(sketch, "E984", {"start": v(-153.46, -633.17) * mm, "mid": v(-147.95, -627.65) * mm, "end": v(-142.44, -633.17) * mm});
            skLineSegment(sketch, "E985", {"start": v(-162.12, -633.17) * mm, "end": v(-162.12, -724.5) * mm});
            skArc(sketch, "E986", {"start": v(-162.12, -724.5) * mm, "mid": v(-167.63, -730.02) * mm, "end": v(-173.15, -724.5) * mm});
            skLineSegment(sketch, "E987", {"start": v(-173.15, -724.5) * mm, "end": v(-173.15, -633.17) * mm});
            skArc(sketch, "E988", {"start": v(-173.15, -633.17) * mm, "mid": v(-167.63, -627.65) * mm, "end": v(-162.12, -633.17) * mm});
            skLineSegment(sketch, "E989", {"start": v(-181.8, -633.17) * mm, "end": v(-181.8, -724.5) * mm});
            skArc(sketch, "E990", {"start": v(-181.8, -724.5) * mm, "mid": v(-187.32, -730.02) * mm, "end": v(-192.83, -724.5) * mm});
            skLineSegment(sketch, "E991", {"start": v(-192.83, -724.5) * mm, "end": v(-192.83, -633.17) * mm});
            skArc(sketch, "E992", {"start": v(-192.83, -633.17) * mm, "mid": v(-187.32, -627.65) * mm, "end": v(-181.8, -633.17) * mm});
            skLineSegment(sketch, "E993", {"start": v(-201.5, -633.17) * mm, "end": v(-201.5, -724.5) * mm});
            skArc(sketch, "E994", {"start": v(-201.5, -724.5) * mm, "mid": v(-207, -730.02) * mm, "end": v(-212.52, -724.5) * mm});
            skLineSegment(sketch, "E995", {"start": v(-212.52, -724.5) * mm, "end": v(-212.52, -633.17) * mm});
            skArc(sketch, "E996", {"start": v(-212.52, -633.17) * mm, "mid": v(-207, -627.65) * mm, "end": v(-201.5, -633.17) * mm});
            skLineSegment(sketch, "E997", {"start": v(-221.18, -633.17) * mm, "end": v(-221.18, -724.5) * mm});
            skArc(sketch, "E998", {"start": v(-221.18, -724.5) * mm, "mid": v(-226.69, -730.02) * mm, "end": v(-232.2, -724.5) * mm});
            skLineSegment(sketch, "E999", {"start": v(-232.2, -724.5) * mm, "end": v(-232.2, -633.17) * mm});
            skArc(sketch, "E1000", {"start": v(-232.2, -633.17) * mm, "mid": v(-226.69, -627.65) * mm, "end": v(-221.18, -633.17) * mm});
            skLineSegment(sketch, "E1001", {"start": v(-240.86, -633.17) * mm, "end": v(-240.86, -724.5) * mm});
            skArc(sketch, "E1002", {"start": v(-240.86, -724.5) * mm, "mid": v(-246.37, -730.02) * mm, "end": v(-251.89, -724.5) * mm});
            skLineSegment(sketch, "E1003", {"start": v(-251.89, -724.5) * mm, "end": v(-251.89, -633.17) * mm});
            skArc(sketch, "E1004", {"start": v(-251.89, -633.17) * mm, "mid": v(-246.37, -627.65) * mm, "end": v(-240.86, -633.17) * mm});
            skLineSegment(sketch, "E1005", {"start": v(-260.55, -633.17) * mm, "end": v(-260.55, -724.5) * mm});
            skArc(sketch, "E1006", {"start": v(-260.55, -724.5) * mm, "mid": v(-266.06, -730.02) * mm, "end": v(-271.57, -724.5) * mm});
            skLineSegment(sketch, "E1007", {"start": v(-271.57, -724.5) * mm, "end": v(-271.57, -633.17) * mm});
            skArc(sketch, "E1008", {"start": v(-271.57, -633.17) * mm, "mid": v(-266.06, -627.65) * mm, "end": v(-260.55, -633.17) * mm});
            skLineSegment(sketch, "E1009", {"start": v(-280.23, -633.17) * mm, "end": v(-280.23, -724.5) * mm});
            skArc(sketch, "E1010", {"start": v(-280.23, -724.5) * mm, "mid": v(-285.74, -730.02) * mm, "end": v(-291.26, -724.5) * mm});
            skLineSegment(sketch, "E1011", {"start": v(-291.26, -724.5) * mm, "end": v(-291.26, -633.17) * mm});
            skArc(sketch, "E1012", {"start": v(-291.26, -633.17) * mm, "mid": v(-285.74, -627.65) * mm, "end": v(-280.23, -633.17) * mm});
            skLineSegment(sketch, "E1013", {"start": v(-299.92, -633.17) * mm, "end": v(-299.92, -724.5) * mm});
            skArc(sketch, "E1014", {"start": v(-299.92, -724.5) * mm, "mid": v(-305.43, -730.02) * mm, "end": v(-310.94, -724.5) * mm});
            skLineSegment(sketch, "E1015", {"start": v(-310.94, -724.5) * mm, "end": v(-310.94, -633.17) * mm});
            skArc(sketch, "E1016", {"start": v(-310.94, -633.17) * mm, "mid": v(-305.43, -627.65) * mm, "end": v(-299.92, -633.17) * mm});
            skLineSegment(sketch, "E1017", {"start": v(-319.6, -633.17) * mm, "end": v(-319.6, -724.5) * mm});
            skArc(sketch, "E1018", {"start": v(-319.6, -724.5) * mm, "mid": v(-325.11, -730.02) * mm, "end": v(-330.63, -724.5) * mm});
            skLineSegment(sketch, "E1019", {"start": v(-330.63, -724.5) * mm, "end": v(-330.63, -633.17) * mm});
            skArc(sketch, "E1020", {"start": v(-330.63, -633.17) * mm, "mid": v(-325.11, -627.65) * mm, "end": v(-319.6, -633.17) * mm});
            skLineSegment(sketch, "E1021", {"start": v(-339.29, -633.17) * mm, "end": v(-339.29, -724.5) * mm});
            skArc(sketch, "E1022", {"start": v(-339.29, -724.5) * mm, "mid": v(-344.8, -730.02) * mm, "end": v(-350.31, -724.5) * mm});
            skLineSegment(sketch, "E1023", {"start": v(-350.31, -724.5) * mm, "end": v(-350.31, -633.17) * mm});
            skArc(sketch, "E1024", {"start": v(-350.31, -633.17) * mm, "mid": v(-344.8, -627.65) * mm, "end": v(-339.29, -633.17) * mm});
            skLineSegment(sketch, "E1025", {"start": v(-358.97, -633.17) * mm, "end": v(-358.97, -724.5) * mm});
            skArc(sketch, "E1026", {"start": v(-358.97, -724.5) * mm, "mid": v(-364.48, -730.02) * mm, "end": v(-370, -724.5) * mm});
            skLineSegment(sketch, "E1027", {"start": v(-370, -724.5) * mm, "end": v(-370, -633.17) * mm});
            skArc(sketch, "E1028", {"start": v(-370, -633.17) * mm, "mid": v(-364.48, -627.65) * mm, "end": v(-358.97, -633.17) * mm});
            skLineSegment(sketch, "E1029", {"start": v(-378.66, -633.17) * mm, "end": v(-378.66, -724.5) * mm});
            skArc(sketch, "E1030", {"start": v(-378.66, -724.5) * mm, "mid": v(-384.17, -730.02) * mm, "end": v(-389.68, -724.5) * mm});
            skLineSegment(sketch, "E1031", {"start": v(-389.68, -724.5) * mm, "end": v(-389.68, -633.17) * mm});
            skArc(sketch, "E1032", {"start": v(-389.68, -633.17) * mm, "mid": v(-384.17, -627.65) * mm, "end": v(-378.66, -633.17) * mm});
            skLineSegment(sketch, "E1033", {"start": v(-503.4, -628.05) * mm, "end": v(-401.4, -628.05) * mm});
            skLineSegment(sketch, "E1034", {"start": v(-13.4, -628.05) * mm, "end": v(88.6, -628.05) * mm});
            skLineSegment(sketch, "E1035", {"start": v(88.6, -779.05) * mm, "end": v(88.6, -1124.11) * mm});
            skLineSegment(sketch, "E1036", {"start": v(88.6, -1124.11) * mm, "end": v(-502.4, -1124.11) * mm});
            skLineSegment(sketch, "E1037", {"start": v(-502.4, -1124.11) * mm, "end": v(-502.4, -781.05) * mm});
            skLineSegment(sketch, "E1038", {"start": v(-1429.61, -338.56) * mm, "end": v(-1378.61, -338.56) * mm});
            skLineSegment(sketch, "E1039", {"start": v(-1378.61, -338.56) * mm, "end": v(-1378.61, -349.56) * mm});
            skLineSegment(sketch, "E1040", {"start": v(-1378.61, -349.56) * mm, "end": v(-1429.61, -349.56) * mm});
            skLineSegment(sketch, "E1041", {"start": v(-1429.61, -349.56) * mm, "end": v(-1429.61, -338.56) * mm});
            skLineSegment(sketch, "E1042", {"start": v(-1429.61, -318.85) * mm, "end": v(-1378.61, -318.85) * mm});
            skLineSegment(sketch, "E1043", {"start": v(-1378.61, -318.85) * mm, "end": v(-1378.61, -329.85) * mm});
            skLineSegment(sketch, "E1044", {"start": v(-1378.61, -329.85) * mm, "end": v(-1429.61, -329.85) * mm});
            skLineSegment(sketch, "E1045", {"start": v(-1429.61, -329.85) * mm, "end": v(-1429.61, -318.85) * mm});
            skLineSegment(sketch, "E1046", {"start": v(-1463.11, -373.6) * mm, "end": v(-1463.11, -452.3) * mm});
            skLineSegment(sketch, "E1047", {"start": v(-1463.11, -452.3) * mm, "end": v(-1561.52, -452.3) * mm});
            skLineSegment(sketch, "E1048", {"start": v(-1561.52, -452.3) * mm, "end": v(-1561.52, -373.6) * mm});
            skLineSegment(sketch, "E1049", {"start": v(-1561.52, -373.6) * mm, "end": v(-1463.11, -373.6) * mm});
            skLineSegment(sketch, "E1050", {"start": v(-1429.61, -299.15) * mm, "end": v(-1378.61, -299.15) * mm});
            skLineSegment(sketch, "E1051", {"start": v(-1378.61, -299.15) * mm, "end": v(-1378.61, -310.15) * mm});
            skLineSegment(sketch, "E1052", {"start": v(-1378.61, -310.15) * mm, "end": v(-1429.61, -310.15) * mm});
            skLineSegment(sketch, "E1053", {"start": v(-1429.61, -310.15) * mm, "end": v(-1429.61, -299.15) * mm});
            skLineSegment(sketch, "E1054", {"start": v(-1429.61, -279.45) * mm, "end": v(-1378.61, -279.45) * mm});
            skLineSegment(sketch, "E1055", {"start": v(-1378.61, -279.45) * mm, "end": v(-1378.61, -290.45) * mm});
            skLineSegment(sketch, "E1056", {"start": v(-1378.61, -290.45) * mm, "end": v(-1429.61, -290.45) * mm});
            skLineSegment(sketch, "E1057", {"start": v(-1429.61, -290.45) * mm, "end": v(-1429.61, -279.45) * mm});
            skLineSegment(sketch, "E1058", {"start": v(-1429.61, -259.75) * mm, "end": v(-1378.61, -259.75) * mm});
            skLineSegment(sketch, "E1059", {"start": v(-1378.61, -259.75) * mm, "end": v(-1378.61, -270.75) * mm});
            skLineSegment(sketch, "E1060", {"start": v(-1378.61, -270.75) * mm, "end": v(-1429.61, -270.75) * mm});
            skLineSegment(sketch, "E1061", {"start": v(-1429.61, -270.75) * mm, "end": v(-1429.61, -259.75) * mm});
            skLineSegment(sketch, "E1062", {"start": v(-1429.61, -240.15) * mm, "end": v(-1378.61, -240.15) * mm});
            skLineSegment(sketch, "E1063", {"start": v(-1378.61, -240.15) * mm, "end": v(-1378.61, -251.15) * mm});
            skLineSegment(sketch, "E1064", {"start": v(-1378.61, -251.15) * mm, "end": v(-1429.61, -251.15) * mm});
            skLineSegment(sketch, "E1065", {"start": v(-1429.61, -251.15) * mm, "end": v(-1429.61, -240.15) * mm});
            skLineSegment(sketch, "E1066", {"start": v(-1429.61, -220.45) * mm, "end": v(-1378.61, -220.45) * mm});
            skLineSegment(sketch, "E1067", {"start": v(-1378.61, -220.45) * mm, "end": v(-1378.61, -231.45) * mm});
            skLineSegment(sketch, "E1068", {"start": v(-1378.61, -231.45) * mm, "end": v(-1429.61, -231.45) * mm});
            skLineSegment(sketch, "E1069", {"start": v(-1429.61, -231.45) * mm, "end": v(-1429.61, -220.45) * mm});
            skLineSegment(sketch, "E1070", {"start": v(-1429.61, -200.75) * mm, "end": v(-1378.61, -200.75) * mm});
            skLineSegment(sketch, "E1071", {"start": v(-1378.61, -200.75) * mm, "end": v(-1378.61, -211.75) * mm});
            skLineSegment(sketch, "E1072", {"start": v(-1378.61, -211.75) * mm, "end": v(-1429.61, -211.75) * mm});
            skLineSegment(sketch, "E1073", {"start": v(-1429.61, -211.75) * mm, "end": v(-1429.61, -200.75) * mm});
            skLineSegment(sketch, "E1074", {"start": v(-1429.61, -181.06) * mm, "end": v(-1378.61, -181.06) * mm});
            skLineSegment(sketch, "E1075", {"start": v(-1378.61, -181.06) * mm, "end": v(-1378.61, -192.06) * mm});
            skLineSegment(sketch, "E1076", {"start": v(-1378.61, -192.06) * mm, "end": v(-1429.61, -192.06) * mm});
            skLineSegment(sketch, "E1077", {"start": v(-1429.61, -192.06) * mm, "end": v(-1429.61, -181.06) * mm});
            skLineSegment(sketch, "E1078", {"start": v(-1429.61, -161.35) * mm, "end": v(-1378.61, -161.35) * mm});
            skLineSegment(sketch, "E1079", {"start": v(-1378.61, -161.35) * mm, "end": v(-1378.61, -172.35) * mm});
            skLineSegment(sketch, "E1080", {"start": v(-1378.61, -172.35) * mm, "end": v(-1429.61, -172.35) * mm});
            skLineSegment(sketch, "E1081", {"start": v(-1429.61, -172.35) * mm, "end": v(-1429.61, -161.35) * mm});
            skLineSegment(sketch, "E1082", {"start": v(-1429.61, -141.65) * mm, "end": v(-1378.61, -141.65) * mm});
            skLineSegment(sketch, "E1083", {"start": v(-1378.61, -141.65) * mm, "end": v(-1378.61, -152.65) * mm});
            skLineSegment(sketch, "E1084", {"start": v(-1378.61, -152.65) * mm, "end": v(-1429.61, -152.65) * mm});
            skLineSegment(sketch, "E1085", {"start": v(-1429.61, -152.65) * mm, "end": v(-1429.61, -141.65) * mm});
            skLineSegment(sketch, "E1086", {"start": v(-1429.61, -121.95) * mm, "end": v(-1378.61, -121.95) * mm});
            skLineSegment(sketch, "E1087", {"start": v(-1378.61, -121.95) * mm, "end": v(-1378.61, -132.95) * mm});
            skLineSegment(sketch, "E1088", {"start": v(-1378.61, -132.95) * mm, "end": v(-1429.61, -132.95) * mm});
            skLineSegment(sketch, "E1089", {"start": v(-1429.61, -132.95) * mm, "end": v(-1429.61, -121.95) * mm});
            skLineSegment(sketch, "E1090", {"start": v(-1429.61, -102.35) * mm, "end": v(-1378.61, -102.35) * mm});
            skLineSegment(sketch, "E1091", {"start": v(-1378.61, -102.35) * mm, "end": v(-1378.61, -113.35) * mm});
            skLineSegment(sketch, "E1092", {"start": v(-1378.61, -113.35) * mm, "end": v(-1429.61, -113.35) * mm});
            skLineSegment(sketch, "E1093", {"start": v(-1429.61, -113.35) * mm, "end": v(-1429.61, -102.35) * mm});
            skLineSegment(sketch, "E1094", {"start": v(-1429.61, -82.65) * mm, "end": v(-1378.61, -82.65) * mm});
            skLineSegment(sketch, "E1095", {"start": v(-1378.61, -82.65) * mm, "end": v(-1378.61, -93.65) * mm});
            skLineSegment(sketch, "E1096", {"start": v(-1378.61, -93.65) * mm, "end": v(-1429.61, -93.65) * mm});
            skLineSegment(sketch, "E1097", {"start": v(-1429.61, -93.65) * mm, "end": v(-1429.61, -82.65) * mm});
            skLineSegment(sketch, "E1098", {"start": v(-1429.61, 35.44) * mm, "end": v(-1378.61, 35.44) * mm});
            skLineSegment(sketch, "E1099", {"start": v(-1378.61, 35.44) * mm, "end": v(-1378.61, 24.44) * mm});
            skLineSegment(sketch, "E1100", {"start": v(-1378.61, 24.44) * mm, "end": v(-1429.61, 24.44) * mm});
            skLineSegment(sketch, "E1101", {"start": v(-1429.61, 24.44) * mm, "end": v(-1429.61, 35.44) * mm});
            skLineSegment(sketch, "E1102", {"start": v(-1429.61, 15.85) * mm, "end": v(-1378.61, 15.85) * mm});
            skLineSegment(sketch, "E1103", {"start": v(-1378.61, 15.85) * mm, "end": v(-1378.61, 4.85) * mm});
            skLineSegment(sketch, "E1104", {"start": v(-1378.61, 4.85) * mm, "end": v(-1429.61, 4.85) * mm});
            skLineSegment(sketch, "E1105", {"start": v(-1429.61, 4.85) * mm, "end": v(-1429.61, 15.85) * mm});
            skLineSegment(sketch, "E1106", {"start": v(-1429.61, -3.85) * mm, "end": v(-1378.61, -3.85) * mm});
            skLineSegment(sketch, "E1107", {"start": v(-1378.61, -3.85) * mm, "end": v(-1378.61, -14.85) * mm});
            skLineSegment(sketch, "E1108", {"start": v(-1378.61, -14.85) * mm, "end": v(-1429.61, -14.85) * mm});
            skLineSegment(sketch, "E1109", {"start": v(-1429.61, -14.85) * mm, "end": v(-1429.61, -3.85) * mm});
            skLineSegment(sketch, "E1110", {"start": v(-1429.61, -23.56) * mm, "end": v(-1378.61, -23.56) * mm});
            skLineSegment(sketch, "E1111", {"start": v(-1378.61, -23.56) * mm, "end": v(-1378.61, -34.56) * mm});
            skLineSegment(sketch, "E1112", {"start": v(-1378.61, -34.56) * mm, "end": v(-1429.61, -34.56) * mm});
            skLineSegment(sketch, "E1113", {"start": v(-1429.61, -34.56) * mm, "end": v(-1429.61, -23.56) * mm});
            skLineSegment(sketch, "E1114", {"start": v(-1429.61, -43.25) * mm, "end": v(-1378.61, -43.25) * mm});
            skLineSegment(sketch, "E1115", {"start": v(-1378.61, -43.25) * mm, "end": v(-1378.61, -54.25) * mm});
            skLineSegment(sketch, "E1116", {"start": v(-1378.61, -54.25) * mm, "end": v(-1429.61, -54.25) * mm});
            skLineSegment(sketch, "E1117", {"start": v(-1429.61, -54.25) * mm, "end": v(-1429.61, -43.25) * mm});
            skLineSegment(sketch, "E1118", {"start": v(-1429.61, -62.95) * mm, "end": v(-1378.61, -62.95) * mm});
            skLineSegment(sketch, "E1119", {"start": v(-1378.61, -62.95) * mm, "end": v(-1378.61, -73.95) * mm});
            skLineSegment(sketch, "E1120", {"start": v(-1378.61, -73.95) * mm, "end": v(-1429.61, -73.95) * mm});
            skLineSegment(sketch, "E1121", {"start": v(-1429.61, -73.95) * mm, "end": v(-1429.61, -62.95) * mm});
            skLineSegment(sketch, "E1122", {"start": v(-1429.61, 114.25) * mm, "end": v(-1378.61, 114.25) * mm});
            skLineSegment(sketch, "E1123", {"start": v(-1378.61, 114.25) * mm, "end": v(-1378.61, 103.25) * mm});
            skLineSegment(sketch, "E1124", {"start": v(-1378.61, 103.25) * mm, "end": v(-1429.61, 103.25) * mm});
            skLineSegment(sketch, "E1125", {"start": v(-1429.61, 103.25) * mm, "end": v(-1429.61, 114.25) * mm});
            skLineSegment(sketch, "E1126", {"start": v(-1429.61, 94.55) * mm, "end": v(-1378.61, 94.55) * mm});
            skLineSegment(sketch, "E1127", {"start": v(-1378.61, 94.55) * mm, "end": v(-1378.61, 83.55) * mm});
            skLineSegment(sketch, "E1128", {"start": v(-1378.61, 83.55) * mm, "end": v(-1429.61, 83.55) * mm});
            skLineSegment(sketch, "E1129", {"start": v(-1429.61, 83.55) * mm, "end": v(-1429.61, 94.55) * mm});
            skLineSegment(sketch, "E1130", {"start": v(-1429.61, 74.85) * mm, "end": v(-1378.61, 74.85) * mm});
            skLineSegment(sketch, "E1131", {"start": v(-1378.61, 74.85) * mm, "end": v(-1378.61, 63.85) * mm});
            skLineSegment(sketch, "E1132", {"start": v(-1378.61, 63.85) * mm, "end": v(-1429.61, 63.85) * mm});
            skLineSegment(sketch, "E1133", {"start": v(-1429.61, 63.85) * mm, "end": v(-1429.61, 74.85) * mm});
            skLineSegment(sketch, "E1134", {"start": v(-1429.61, 55.15) * mm, "end": v(-1378.61, 55.15) * mm});
            skLineSegment(sketch, "E1135", {"start": v(-1378.61, 55.15) * mm, "end": v(-1378.61, 44.15) * mm});
            skLineSegment(sketch, "E1136", {"start": v(-1378.61, 44.15) * mm, "end": v(-1429.61, 44.15) * mm});
            skLineSegment(sketch, "E1137", {"start": v(-1429.61, 44.15) * mm, "end": v(-1429.61, 55.15) * mm});
            skLineSegment(sketch, "E1138", {"start": v(-1463.11, 217) * mm, "end": v(-1463.11, 138.3) * mm});
            skLineSegment(sketch, "E1139", {"start": v(-1463.11, 138.3) * mm, "end": v(-1561.52, 138.3) * mm});
            skLineSegment(sketch, "E1140", {"start": v(-1561.52, 138.3) * mm, "end": v(-1561.52, 217) * mm});
            skLineSegment(sketch, "E1141", {"start": v(-1561.52, 217) * mm, "end": v(-1463.11, 217) * mm});
            skLineSegment(sketch, "E1142", {"start": v(-1458.02, -436.55) * mm, "end": v(-1421.82, -436.55) * mm});
            skLineSegment(sketch, "E1143", {"start": v(-1421.82, -436.55) * mm, "end": v(-1421.82, -362.65) * mm});
            skLineSegment(sketch, "E1144", {"start": v(-1337.02, 123.15) * mm, "end": v(-1337.02, 93.15) * mm});
            skLineSegment(sketch, "E1145", {"start": v(-1337.02, 93.15) * mm, "end": v(-1362.02, 108.15) * mm});
            skLineSegment(sketch, "E1146", {"start": v(-1362.02, 108.15) * mm, "end": v(-1337.02, 123.15) * mm});
            skLineSegment(sketch, "E1147", {"start": v(-1337.02, 123.15) * mm, "end": v(-1337.02, 118.15) * mm});
            skLineSegment(sketch, "E1148", {"start": v(-1337.02, 118.15) * mm, "end": v(-1341.02, 118.15) * mm});
            skLineSegment(sketch, "E1149", {"start": v(-1341.02, 118.15) * mm, "end": v(-1341.02, 98.15) * mm});
            skLineSegment(sketch, "E1150", {"start": v(-1341.02, 98.15) * mm, "end": v(-1345.02, 100.15) * mm});
            skLineSegment(sketch, "E1151", {"start": v(-1345.02, 100.15) * mm, "end": v(-1345.02, 115.15) * mm});
            skLineSegment(sketch, "E1152", {"start": v(-1345.02, 115.15) * mm, "end": v(-1348.02, 113.15) * mm});
            skLineSegment(sketch, "E1153", {"start": v(-1348.02, 113.15) * mm, "end": v(-1348.02, 102.15) * mm});
            skLineSegment(sketch, "E1154", {"start": v(-1348.02, 102.15) * mm, "end": v(-1357.02, 108.15) * mm});
            skLineSegment(sketch, "E1155", {"start": v(-1357.02, 108.15) * mm, "end": v(-1351.02, 112.15) * mm});
            skLineSegment(sketch, "E1156", {"start": v(-1351.02, 112.15) * mm, "end": v(-1351.02, 107.15) * mm});
            skLineSegment(sketch, "E1157", {"start": v(-1418.62, 132.35) * mm, "end": v(-1418.62, 201.25) * mm});
            skLineSegment(sketch, "E1158", {"start": v(-1418.62, 201.25) * mm, "end": v(-1442.52, 201.25) * mm});
            skLineSegment(sketch, "E1159", {"start": v(-1572.52, 201.25) * mm, "end": v(-1650.92, 201.25) * mm});
            skLineSegment(sketch, "E1160", {"start": v(-1650.92, 201.25) * mm, "end": v(-1650.92, -436.55) * mm});
            skLineSegment(sketch, "E1161", {"start": v(-1650.92, -436.55) * mm, "end": v(-1567.52, -436.55) * mm});
            skCircle(sketch, "E1162", {"center": v(-1285.67, 1044.86) * mm, "radius": 27.56 * mm});
            skLineSegment(sketch, "E1163", {"start": v(-1313.23, 917.3) * mm, "end": v(-1313.23, 972.42) * mm});
            skLineSegment(sketch, "E1164", {"start": v(-1313.23, 972.42) * mm, "end": v(-1258.1, 972.42) * mm});
            skLineSegment(sketch, "E1165", {"start": v(-1258.1, 972.42) * mm, "end": v(-1258.1, 917.3) * mm});
            skLineSegment(sketch, "E1166", {"start": v(-1258.1, 917.3) * mm, "end": v(-1313.23, 917.3) * mm});
            skCircle(sketch, "E1167", {"center": v(-1185.67, 944.86) * mm, "radius": 27.56 * mm});
            skCircle(sketch, "E1168", {"center": v(-1185.67, 1044.86) * mm, "radius": 27.56 * mm});
            skCircle(sketch, "E1169", {"center": v(-1085.67, 944.86) * mm, "radius": 27.56 * mm});
            skCircle(sketch, "E1170", {"center": v(-1085.67, 1044.86) * mm, "radius": 27.56 * mm});
            skCircle(sketch, "E1171", {"center": v(-985.67, 944.86) * mm, "radius": 27.56 * mm});
            skCircle(sketch, "E1172", {"center": v(-985.67, 1044.86) * mm, "radius": 27.56 * mm});
            skCircle(sketch, "E1173", {"center": v(-885.67, 944.86) * mm, "radius": 27.56 * mm});
            skCircle(sketch, "E1174", {"center": v(-885.67, 1044.86) * mm, "radius": 27.56 * mm});
            skCircle(sketch, "E1175", {"center": v(-785.67, 944.86) * mm, "radius": 27.56 * mm});
            skCircle(sketch, "E1176", {"center": v(-785.67, 1044.86) * mm, "radius": 27.56 * mm});
            skCircle(sketch, "E1177", {"center": v(-685.67, 944.86) * mm, "radius": 27.56 * mm});
            skCircle(sketch, "E1178", {"center": v(-685.67, 1044.86) * mm, "radius": 27.56 * mm});
            skCircle(sketch, "E1179", {"center": v(-585.67, 944.86) * mm, "radius": 27.56 * mm});
            skCircle(sketch, "E1180", {"center": v(-585.67, 1044.86) * mm, "radius": 27.56 * mm});
            skCircle(sketch, "E1181", {"center": v(-485.67, 944.86) * mm, "radius": 27.56 * mm});
            skCircle(sketch, "E1182", {"center": v(-485.67, 1044.86) * mm, "radius": 27.56 * mm});
            skCircle(sketch, "E1183", {"center": v(-385.67, 944.86) * mm, "radius": 27.56 * mm});
            skCircle(sketch, "E1184", {"center": v(-385.67, 1044.86) * mm, "radius": 27.56 * mm});
            skCircle(sketch, "E1185", {"center": v(-285.67, 944.86) * mm, "radius": 27.56 * mm});
            skCircle(sketch, "E1186", {"center": v(-285.67, 1044.86) * mm, "radius": 27.56 * mm});
            skCircle(sketch, "E1187", {"center": v(-185.67, 944.86) * mm, "radius": 27.56 * mm});
            skCircle(sketch, "E1188", {"center": v(-185.67, 1044.86) * mm, "radius": 27.56 * mm});
            skCircle(sketch, "E1189", {"center": v(-85.67, 944.86) * mm, "radius": 27.56 * mm});
            skCircle(sketch, "E1190", {"center": v(-85.67, 1044.86) * mm, "radius": 27.56 * mm});
            skCircle(sketch, "E1191", {"center": v(14.33, 944.86) * mm, "radius": 27.56 * mm});
            skCircle(sketch, "E1192", {"center": v(14.33, 1044.86) * mm, "radius": 27.56 * mm});
            skCircle(sketch, "E1193", {"center": v(114.33, 944.86) * mm, "radius": 27.56 * mm});
            skCircle(sketch, "E1194", {"center": v(114.33, 1044.86) * mm, "radius": 27.56 * mm});
            skCircle(sketch, "E1195", {"center": v(214.33, 944.86) * mm, "radius": 27.56 * mm});
            skCircle(sketch, "E1196", {"center": v(214.33, 1044.86) * mm, "radius": 27.56 * mm});
            skCircle(sketch, "E1197", {"center": v(314.33, 944.86) * mm, "radius": 27.56 * mm});
            skCircle(sketch, "E1198", {"center": v(314.33, 1044.86) * mm, "radius": 27.56 * mm});
            skCircle(sketch, "E1199", {"center": v(414.33, 944.86) * mm, "radius": 27.56 * mm});
            skCircle(sketch, "E1200", {"center": v(414.33, 1044.86) * mm, "radius": 27.56 * mm});
            skCircle(sketch, "E1201", {"center": v(514.33, 944.86) * mm, "radius": 27.56 * mm});
            skCircle(sketch, "E1202", {"center": v(514.33, 1044.86) * mm, "radius": 27.56 * mm});
            skCircle(sketch, "E1203", {"center": v(614.33, 944.86) * mm, "radius": 27.56 * mm});
            skCircle(sketch, "E1204", {"center": v(614.33, 1044.86) * mm, "radius": 27.56 * mm});
            skLineSegment(sketch, "E1205", {"start": v(-1335.67, 1094.86) * mm, "end": v(664.33, 1094.86) * mm});
            skLineSegment(sketch, "E1206", {"start": v(664.33, 1094.86) * mm, "end": v(664.33, 894.86) * mm});
            skLineSegment(sketch, "E1207", {"start": v(664.33, 894.86) * mm, "end": v(-35.67, 894.86) * mm});
            skLineSegment(sketch, "E1208", {"start": v(-35.67, 894.86) * mm, "end": v(-1335.67, 894.86) * mm});
            skLineSegment(sketch, "E1209", {"start": v(-1335.67, 894.86) * mm, "end": v(-1335.67, 1094.86) * mm});
            skLineSegment(sketch, "E1210", {"start": v(-1285.67, 885.8) * mm, "end": v(-1325.04, 846.44) * mm});
            skLineSegment(sketch, "E1211", {"start": v(-1325.04, 846.44) * mm, "end": v(-1246.3, 846.44) * mm});
            skLineSegment(sketch, "E1212", {"start": v(-1246.3, 846.44) * mm, "end": v(-1285.67, 885.8) * mm});
            skLineSegment(sketch, "E1213", {"start": v(-1673.23, -975.21) * mm, "end": v(-1673.23, 1072.03) * mm});
            skLineSegment(sketch, "E1214", {"start": v(0, 76.62) * mm, "end": v(0, -75.97) * mm});
            skLineSegment(sketch, "E1215", {"start": v(0, 0) * mm, "end": v(75.95, 0) * mm});
            skSolve(sketch);
        }
        {
            var Q0;
            Q0=makeQuery(id+"F0.imprint","IMPRINT",FACE,{"disambiguationData":[TD([[makeQuery(id+"F0.imprint","IMPRINT",EDGE,{"derivedFrom":sQuery(id+"F0.wireOp",EDGE,"E33")}),-1.0]])]});
            var Q1;
            {var subQ4=sQuery(id+"F0.wireOp",EDGE,"E295");Q1=makeQuery(id+"F0.imprint","IMPRINT",FACE,{"disambiguationData":[TD([[makeQuery(id+"F0.imprint","IMPRINT",EDGE,{"derivedFrom":subQ4}),1.0]])]});}
            var Q2;
            {var subQ1=sQuery(id+"F0.wireOp",EDGE,"E285");Q2=makeQuery(id+"F0.imprint","IMPRINT",FACE,{"disambiguationData":[TD([[makeQuery(id+"F0.imprint","IMPRINT",EDGE,{"derivedFrom":subQ1}),1.0]])]});}
            var Q3;
            {var subQ2=sQuery(id+"F0.wireOp",EDGE,"E294");Q3=makeQuery(id+"F0.imprint","IMPRINT",FACE,{"disambiguationData":[TD([[makeQuery(id+"F0.imprint","IMPRINT",EDGE,{"derivedFrom":subQ2}),1.0]])]});}
            var Q4;
            {var subQ3=sQuery(id+"F0.wireOp",EDGE,"E299");Q4=makeQuery(id+"F0.imprint","IMPRINT",FACE,{"disambiguationData":[TD([[makeQuery(id+"F0.imprint","IMPRINT",EDGE,{"derivedFrom":subQ3}),1.0]])]});}
            extrude(context, id + "F1", {"entities" : qUnion([Q0, Q1, Q2, Q3, Q4]), "depth" : 70.97 * mm, "offsetDistance" : 25.4 * mm});
        }
        {
            var Q0;
            Q0=qCreatedBy(makeId("Top.planeOp"),FACE);
            var sketch = newSketch(context, id + "F2", { "sketchPlane" : qUnion([Q0])});
            skCircle(sketch, "E1216", {"center": v(1415.5, 454) * mm, "radius": 65 * mm});
            skCircle(sketch, "E1217", {"center": v(1415.5, 4) * mm, "radius": 65 * mm});
            skLineSegment(sketch, "E1218", {"start": v(1275.73, 560.7) * mm, "end": v(1315.1, 560.7) * mm});
            skArc(sketch, "E1219", {"start": v(1315.1, 560.7) * mm, "mid": v(1338.72, 537.07) * mm, "end": v(1315.1, 513.45) * mm});
            skLineSegment(sketch, "E1220", {"start": v(1315.1, 513.45) * mm, "end": v(1275.73, 513.45) * mm});
            skArc(sketch, "E1221", {"start": v(1275.73, 513.45) * mm, "mid": v(1252.1, 537.07) * mm, "end": v(1275.73, 560.7) * mm});
            skLineSegment(sketch, "E1222", {"start": v(1275.73, -55.45) * mm, "end": v(1315.1, -55.45) * mm});
            skArc(sketch, "E1223", {"start": v(1315.1, -55.45) * mm, "mid": v(1338.72, -79.07) * mm, "end": v(1315.1, -102.7) * mm});
            skLineSegment(sketch, "E1224", {"start": v(1315.1, -102.7) * mm, "end": v(1275.73, -102.7) * mm});
            skArc(sketch, "E1225", {"start": v(1275.73, -102.7) * mm, "mid": v(1252.1, -79.07) * mm, "end": v(1275.73, -55.45) * mm});
            skCircle(sketch, "E1226", {"center": v(1165.5, 354) * mm, "radius": 21.65 * mm});
            skCircle(sketch, "E1227", {"center": v(1165.5, 254) * mm, "radius": 21.65 * mm});
            skCircle(sketch, "E1228", {"center": v(1165.5, 154) * mm, "radius": 21.65 * mm});
            skCircle(sketch, "E1229", {"center": v(1065.5, 404) * mm, "radius": 21.65 * mm});
            skCircle(sketch, "E1230", {"center": v(1065.5, 304) * mm, "radius": 21.65 * mm});
            skCircle(sketch, "E1231", {"center": v(1065.5, 204) * mm, "radius": 21.65 * mm});
            skCircle(sketch, "E1232", {"center": v(1065.5, 104) * mm, "radius": 21.65 * mm});
            skLineSegment(sketch, "E1233", {"start": v(-1594.49, 1150.77) * mm, "end": v(1594.49, 1150.77) * mm});
            skArc(sketch, "E1234", {"start": v(1594.49, 1150.77) * mm, "mid": v(1650.16, 1127.7) * mm, "end": v(1673.22, 1072.03) * mm});
            skLineSegment(sketch, "E1235", {"start": v(1673.22, 1072.03) * mm, "end": v(1673.22, -975.21) * mm});
            skArc(sketch, "E1236", {"start": v(1673.22, -975.21) * mm, "mid": v(1650.16, -1030.89) * mm, "end": v(1594.49, -1053.95) * mm});
            skLineSegment(sketch, "E1237", {"start": v(1594.48, -1053.95) * mm, "end": v(-1594.49, -1053.95) * mm});
            skArc(sketch, "E1238", {"start": v(-1594.49, -1053.95) * mm, "mid": v(-1650.16, -1030.89) * mm, "end": v(-1673.22, -975.21) * mm});
            skArc(sketch, "E1239", {"start": v(-1673.22, 1072.03) * mm, "mid": v(-1650.16, 1127.7) * mm, "end": v(-1594.49, 1150.77) * mm});
            skCircle(sketch, "E1240", {"center": v(872.83, -702.9) * mm, "radius": 31.5 * mm});
            skCircle(sketch, "E1241", {"center": v(872.83, -939.11) * mm, "radius": 31.5 * mm});
            skCircle(sketch, "E1242", {"center": v(1131.83, 770.35) * mm, "radius": 27.56 * mm});
            skCircle(sketch, "E1243", {"center": v(1210.57, 770.35) * mm, "radius": 27.56 * mm});
            skCircle(sketch, "E1244", {"center": v(1289.31, 770.35) * mm, "radius": 27.56 * mm});
            skCircle(sketch, "E1245", {"center": v(1368.05, 770.35) * mm, "radius": 27.56 * mm});
            skCircle(sketch, "E1246", {"center": v(1112.15, 876.65) * mm, "radius": 35.43 * mm});
            skCircle(sketch, "E1247", {"center": v(1387.74, 876.65) * mm, "radius": 35.43 * mm});
            skCircle(sketch, "E1248", {"center": v(1387.74, 664.05) * mm, "radius": 35.43 * mm});
            skCircle(sketch, "E1249", {"center": v(1112.15, 664.05) * mm, "radius": 35.43 * mm});
            skLineSegment(sketch, "E1250", {"start": v(-1642.2, -656.51) * mm, "end": v(-1642.2, -638.8) * mm});
            skArc(sketch, "E1251", {"start": v(-1642.2, -638.8) * mm, "mid": v(-1622.52, -619.1) * mm, "end": v(-1602.83, -638.8) * mm});
            skLineSegment(sketch, "E1252", {"start": v(-1602.83, -638.8) * mm, "end": v(-1602.83, -656.51) * mm});
            skArc(sketch, "E1253", {"start": v(-1602.83, -656.51) * mm, "mid": v(-1622.52, -676.2) * mm, "end": v(-1642.2, -656.51) * mm});
            skLineSegment(sketch, "E1254", {"start": v(-1563.46, -597.46) * mm, "end": v(-1563.46, -579.74) * mm});
            skArc(sketch, "E1255", {"start": v(-1563.46, -579.74) * mm, "mid": v(-1543.78, -560.05) * mm, "end": v(-1524.1, -579.74) * mm});
            skLineSegment(sketch, "E1256", {"start": v(-1524.1, -579.74) * mm, "end": v(-1524.1, -597.46) * mm});
            skArc(sketch, "E1257", {"start": v(-1524.1, -597.46) * mm, "mid": v(-1543.78, -617.14) * mm, "end": v(-1563.46, -597.46) * mm});
            skLineSegment(sketch, "E1258", {"start": v(-1563.46, -715.57) * mm, "end": v(-1563.46, -697.85) * mm});
            skArc(sketch, "E1259", {"start": v(-1563.46, -697.85) * mm, "mid": v(-1543.78, -678.16) * mm, "end": v(-1524.1, -697.85) * mm});
            skLineSegment(sketch, "E1260", {"start": v(-1524.1, -697.85) * mm, "end": v(-1524.1, -715.57) * mm});
            skArc(sketch, "E1261", {"start": v(-1524.1, -715.57) * mm, "mid": v(-1543.78, -735.25) * mm, "end": v(-1563.46, -715.57) * mm});
            skLineSegment(sketch, "E1262", {"start": v(272.36, -971.28) * mm, "end": v(272.36, -955.53) * mm});
            skArc(sketch, "E1263", {"start": v(272.36, -955.53) * mm, "mid": v(288.1, -939.78) * mm, "end": v(303.85, -955.53) * mm});
            skLineSegment(sketch, "E1264", {"start": v(303.85, -955.53) * mm, "end": v(303.85, -971.28) * mm});
            skArc(sketch, "E1265", {"start": v(303.85, -971.28) * mm, "mid": v(288.1, -987.02) * mm, "end": v(272.36, -971.28) * mm});
            skLineSegment(sketch, "E1266", {"start": v(201.5, -971.28) * mm, "end": v(201.5, -955.53) * mm});
            skArc(sketch, "E1267", {"start": v(201.5, -955.53) * mm, "mid": v(217.24, -939.78) * mm, "end": v(232.99, -955.53) * mm});
            skLineSegment(sketch, "E1268", {"start": v(232.99, -955.53) * mm, "end": v(232.99, -971.28) * mm});
            skArc(sketch, "E1269", {"start": v(232.99, -971.28) * mm, "mid": v(217.24, -987.02) * mm, "end": v(201.5, -971.28) * mm});
            skCircle(sketch, "E1270", {"center": v(-1299.2, -966.63) * mm, "radius": 27.56 * mm});
            skCircle(sketch, "E1271", {"center": v(-1141.73, -966.63) * mm, "radius": 27.56 * mm});
            skCircle(sketch, "E1272", {"center": v(-1181.1, -694.98) * mm, "radius": 43.3 * mm});
            skLineSegment(sketch, "E1273", {"start": v(-1265.74, -639.86) * mm, "end": v(-1265.74, -663.48) * mm});
            skArc(sketch, "E1274", {"start": v(-1265.74, -663.48) * mm, "mid": v(-1295.27, -693) * mm, "end": v(-1324.8, -663.48) * mm});
            skLineSegment(sketch, "E1275", {"start": v(-1324.8, -663.48) * mm, "end": v(-1324.8, -639.86) * mm});
            skArc(sketch, "E1276", {"start": v(-1324.8, -639.86) * mm, "mid": v(-1295.27, -610.33) * mm, "end": v(-1265.74, -639.86) * mm});
            skLineSegment(sketch, "E1277", {"start": v(-1328.74, -757.97) * mm, "end": v(-1328.74, -781.6) * mm});
            skArc(sketch, "E1278", {"start": v(-1328.74, -781.6) * mm, "mid": v(-1358.26, -811.12) * mm, "end": v(-1387.8, -781.6) * mm});
            skLineSegment(sketch, "E1279", {"start": v(-1387.8, -781.6) * mm, "end": v(-1387.8, -757.97) * mm});
            skArc(sketch, "E1280", {"start": v(-1387.8, -757.97) * mm, "mid": v(-1358.26, -728.44) * mm, "end": v(-1328.74, -757.97) * mm});
            skLineSegment(sketch, "E1281", {"start": v(1040.34, 1021.52) * mm, "end": v(1040.34, 978.2) * mm});
            skLineSegment(sketch, "E1282", {"start": v(1040.34, 978.2) * mm, "end": v(985.22, 978.2) * mm});
            skLineSegment(sketch, "E1283", {"start": v(985.22, 978.2) * mm, "end": v(985.22, 1021.52) * mm});
            skLineSegment(sketch, "E1284", {"start": v(985.22, 1021.52) * mm, "end": v(1040.34, 1021.52) * mm});
            skLineSegment(sketch, "E1285", {"start": v(906.87, 1021.52) * mm, "end": v(918.68, 1021.52) * mm});
            skArc(sketch, "E1286", {"start": v(918.68, 1021.52) * mm, "mid": v(940.34, 999.86) * mm, "end": v(918.68, 978.2) * mm});
            skLineSegment(sketch, "E1287", {"start": v(918.68, 978.2) * mm, "end": v(906.87, 978.2) * mm});
            skArc(sketch, "E1288", {"start": v(906.87, 978.2) * mm, "mid": v(885.22, 999.86) * mm, "end": v(906.87, 1021.52) * mm});
            skLineSegment(sketch, "E1289", {"start": v(806.87, 1021.52) * mm, "end": v(818.68, 1021.52) * mm});
            skArc(sketch, "E1290", {"start": v(818.68, 1021.52) * mm, "mid": v(840.34, 999.86) * mm, "end": v(818.68, 978.2) * mm});
            skLineSegment(sketch, "E1291", {"start": v(818.68, 978.2) * mm, "end": v(806.87, 978.2) * mm});
            skArc(sketch, "E1292", {"start": v(806.87, 978.2) * mm, "mid": v(785.22, 999.86) * mm, "end": v(806.87, 1021.52) * mm});
            skCircle(sketch, "E1293", {"center": v(-802.52, -952.65) * mm, "radius": 27.56 * mm});
            skCircle(sketch, "E1294", {"center": v(-702.52, -952.65) * mm, "radius": 27.56 * mm});
            skCircle(sketch, "E1295", {"center": v(1324.35, -655.45) * mm, "radius": 19.68 * mm});
            skCircle(sketch, "E1296", {"center": v(1324.35, -557.02) * mm, "radius": 19.68 * mm});
            skCircle(sketch, "E1297", {"center": v(1324.35, -478.28) * mm, "radius": 19.68 * mm});
            skCircle(sketch, "E1298", {"center": v(1324.35, -379.86) * mm, "radius": 19.68 * mm});
            skCircle(sketch, "E1299", {"center": v(1221.2, -655.45) * mm, "radius": 19.68 * mm});
            skCircle(sketch, "E1300", {"center": v(1221.2, -557.02) * mm, "radius": 19.68 * mm});
            skCircle(sketch, "E1301", {"center": v(1221.2, -478.28) * mm, "radius": 19.68 * mm});
            skCircle(sketch, "E1302", {"center": v(1221.2, -379.86) * mm, "radius": 19.68 * mm});
            skLineSegment(sketch, "E1303", {"start": v(1450.73, -822.77) * mm, "end": v(1411.36, -822.77) * mm});
            skArc(sketch, "E1304", {"start": v(1411.36, -822.77) * mm, "mid": v(1371.99, -783.4) * mm, "end": v(1411.36, -744.03) * mm});
            skLineSegment(sketch, "E1305", {"start": v(1411.36, -744.03) * mm, "end": v(1450.73, -744.03) * mm});
            skArc(sketch, "E1306", {"start": v(1450.73, -744.03) * mm, "mid": v(1490.1, -783.4) * mm, "end": v(1450.73, -822.77) * mm});
            skLineSegment(sketch, "E1307", {"start": v(1450.73, -291.28) * mm, "end": v(1411.36, -291.28) * mm});
            skArc(sketch, "E1308", {"start": v(1411.36, -291.28) * mm, "mid": v(1371.99, -251.9) * mm, "end": v(1411.36, -212.54) * mm});
            skLineSegment(sketch, "E1309", {"start": v(1411.36, -212.54) * mm, "end": v(1450.73, -212.54) * mm});
            skArc(sketch, "E1310", {"start": v(1450.73, -212.54) * mm, "mid": v(1490.1, -251.9) * mm, "end": v(1450.73, -291.28) * mm});
            skLineSegment(sketch, "E1311", {"start": v(1227.1, -291.28) * mm, "end": v(1187.74, -291.28) * mm});
            skArc(sketch, "E1312", {"start": v(1187.74, -291.28) * mm, "mid": v(1148.37, -251.9) * mm, "end": v(1187.74, -212.54) * mm});
            skLineSegment(sketch, "E1313", {"start": v(1187.74, -212.54) * mm, "end": v(1227.1, -212.54) * mm});
            skArc(sketch, "E1314", {"start": v(1227.1, -212.54) * mm, "mid": v(1266.48, -251.9) * mm, "end": v(1227.1, -291.28) * mm});
            skLineSegment(sketch, "E1315", {"start": v(1227.1, -822.77) * mm, "end": v(1187.74, -822.77) * mm});
            skArc(sketch, "E1316", {"start": v(1187.74, -822.77) * mm, "mid": v(1148.37, -783.4) * mm, "end": v(1187.74, -744.03) * mm});
            skLineSegment(sketch, "E1317", {"start": v(1187.74, -744.03) * mm, "end": v(1227.1, -744.03) * mm});
            skArc(sketch, "E1318", {"start": v(1227.1, -744.03) * mm, "mid": v(1266.48, -783.4) * mm, "end": v(1227.1, -822.77) * mm});
            skLineSegment(sketch, "E1319", {"start": v(107.96, -937.5) * mm, "end": v(107.96, -949.3) * mm});
            skArc(sketch, "E1320", {"start": v(107.96, -949.3) * mm, "mid": v(78.43, -978.83) * mm, "end": v(48.9, -949.3) * mm});
            skLineSegment(sketch, "E1321", {"start": v(48.9, -949.3) * mm, "end": v(48.9, -937.5) * mm});
            skArc(sketch, "E1322", {"start": v(48.9, -937.5) * mm, "mid": v(78.43, -907.97) * mm, "end": v(107.96, -937.5) * mm});
            skLineSegment(sketch, "E1323", {"start": v(-462.9, -937.5) * mm, "end": v(-462.9, -949.3) * mm});
            skArc(sketch, "E1324", {"start": v(-462.9, -949.3) * mm, "mid": v(-492.44, -978.83) * mm, "end": v(-521.96, -949.3) * mm});
            skLineSegment(sketch, "E1325", {"start": v(-521.96, -949.3) * mm, "end": v(-521.96, -937.5) * mm});
            skArc(sketch, "E1326", {"start": v(-521.96, -937.5) * mm, "mid": v(-492.44, -907.97) * mm, "end": v(-462.9, -937.5) * mm});
            skLineSegment(sketch, "E1327", {"start": v(107.96, -683.16) * mm, "end": v(107.96, -734.35) * mm});
            skArc(sketch, "E1328", {"start": v(107.96, -734.35) * mm, "mid": v(78.43, -763.87) * mm, "end": v(48.9, -734.35) * mm});
            skLineSegment(sketch, "E1329", {"start": v(48.9, -734.35) * mm, "end": v(48.9, -683.16) * mm});
            skArc(sketch, "E1330", {"start": v(48.9, -683.16) * mm, "mid": v(78.43, -653.64) * mm, "end": v(107.96, -683.16) * mm});
            skLineSegment(sketch, "E1331", {"start": v(-462.9, -683.16) * mm, "end": v(-462.9, -734.35) * mm});
            skArc(sketch, "E1332", {"start": v(-462.9, -734.35) * mm, "mid": v(-492.44, -763.87) * mm, "end": v(-521.96, -734.35) * mm});
            skLineSegment(sketch, "E1333", {"start": v(-521.96, -734.35) * mm, "end": v(-521.96, -683.16) * mm});
            skArc(sketch, "E1334", {"start": v(-521.96, -683.16) * mm, "mid": v(-492.44, -653.64) * mm, "end": v(-462.9, -683.16) * mm});
            skLineSegment(sketch, "E1335", {"start": v(-1673.23, -975.21) * mm, "end": v(-1673.23, 1072.03) * mm});
            skCircle(sketch, "E1336", {"center": v(-1558.38, 1034.86) * mm, "radius": 44.45 * mm});
            skCircle(sketch, "E1337", {"center": v(1557.32, 1034.86) * mm, "radius": 44.45 * mm});
            skCircle(sketch, "E1338", {"center": v(1557.32, -938.05) * mm, "radius": 44.45 * mm});
            skCircle(sketch, "E1339", {"center": v(-1557.32, -938.05) * mm, "radius": 44.45 * mm});
            skCircle(sketch, "E1340", {"center": v(-1285.67, 1044.86) * mm, "radius": 27.56 * mm});
            skCircle(sketch, "E1341", {"center": v(-1185.67, 944.86) * mm, "radius": 27.56 * mm});
            skCircle(sketch, "E1342", {"center": v(-1185.67, 1044.86) * mm, "radius": 27.56 * mm});
            skCircle(sketch, "E1343", {"center": v(-1085.67, 944.86) * mm, "radius": 27.56 * mm});
            skCircle(sketch, "E1344", {"center": v(-1085.67, 1044.86) * mm, "radius": 27.56 * mm});
            skCircle(sketch, "E1345", {"center": v(-985.67, 944.86) * mm, "radius": 27.56 * mm});
            skCircle(sketch, "E1346", {"center": v(-985.67, 1044.86) * mm, "radius": 27.56 * mm});
            skCircle(sketch, "E1347", {"center": v(-885.67, 944.86) * mm, "radius": 27.56 * mm});
            skCircle(sketch, "E1348", {"center": v(-885.67, 1044.86) * mm, "radius": 27.56 * mm});
            skCircle(sketch, "E1349", {"center": v(-785.67, 944.86) * mm, "radius": 27.56 * mm});
            skCircle(sketch, "E1350", {"center": v(-785.67, 1044.86) * mm, "radius": 27.56 * mm});
            skCircle(sketch, "E1351", {"center": v(-685.67, 944.86) * mm, "radius": 27.56 * mm});
            skCircle(sketch, "E1352", {"center": v(-685.67, 1044.86) * mm, "radius": 27.56 * mm});
            skCircle(sketch, "E1353", {"center": v(-585.67, 944.86) * mm, "radius": 27.56 * mm});
            skCircle(sketch, "E1354", {"center": v(-585.67, 1044.86) * mm, "radius": 27.56 * mm});
            skCircle(sketch, "E1355", {"center": v(-485.67, 944.86) * mm, "radius": 27.56 * mm});
            skCircle(sketch, "E1356", {"center": v(-485.67, 1044.86) * mm, "radius": 27.56 * mm});
            skCircle(sketch, "E1357", {"center": v(-385.67, 944.86) * mm, "radius": 27.56 * mm});
            skCircle(sketch, "E1358", {"center": v(-385.67, 1044.86) * mm, "radius": 27.56 * mm});
            skCircle(sketch, "E1359", {"center": v(-285.67, 944.86) * mm, "radius": 27.56 * mm});
            skCircle(sketch, "E1360", {"center": v(-285.67, 1044.86) * mm, "radius": 27.56 * mm});
            skCircle(sketch, "E1361", {"center": v(-185.67, 944.86) * mm, "radius": 27.56 * mm});
            skCircle(sketch, "E1362", {"center": v(-185.67, 1044.86) * mm, "radius": 27.56 * mm});
            skCircle(sketch, "E1363", {"center": v(-85.67, 944.86) * mm, "radius": 27.56 * mm});
            skCircle(sketch, "E1364", {"center": v(-85.67, 1044.86) * mm, "radius": 27.56 * mm});
            skCircle(sketch, "E1365", {"center": v(14.33, 944.86) * mm, "radius": 27.56 * mm});
            skCircle(sketch, "E1366", {"center": v(14.33, 1044.86) * mm, "radius": 27.56 * mm});
            skCircle(sketch, "E1367", {"center": v(114.33, 944.86) * mm, "radius": 27.56 * mm});
            skCircle(sketch, "E1368", {"center": v(114.33, 1044.86) * mm, "radius": 27.56 * mm});
            skCircle(sketch, "E1369", {"center": v(214.33, 944.86) * mm, "radius": 27.56 * mm});
            skCircle(sketch, "E1370", {"center": v(214.33, 1044.86) * mm, "radius": 27.56 * mm});
            skCircle(sketch, "E1371", {"center": v(314.33, 944.86) * mm, "radius": 27.56 * mm});
            skCircle(sketch, "E1372", {"center": v(314.33, 1044.86) * mm, "radius": 27.56 * mm});
            skCircle(sketch, "E1373", {"center": v(414.33, 944.86) * mm, "radius": 27.56 * mm});
            skCircle(sketch, "E1374", {"center": v(414.33, 1044.86) * mm, "radius": 27.56 * mm});
            skCircle(sketch, "E1375", {"center": v(514.33, 944.86) * mm, "radius": 27.56 * mm});
            skCircle(sketch, "E1376", {"center": v(514.33, 1044.86) * mm, "radius": 27.56 * mm});
            skCircle(sketch, "E1377", {"center": v(614.33, 944.86) * mm, "radius": 27.56 * mm});
            skCircle(sketch, "E1378", {"center": v(614.33, 1044.86) * mm, "radius": 27.56 * mm});
            skCircle(sketch, "E1379", {"center": v(-1285.67, 944.86) * mm, "radius": 27.56 * mm});
            skCircle(sketch, "E1380", {"center": v(-902.52, -952.65) * mm, "radius": 27.56 * mm});
            skSolve(sketch);
        }
        {
            var Q0;
            Q0 = qSketchRegion(id + "F2", true);
            extrude(context, id + "F3", {"entities" : qUnion([Q0]), "depth" : -40.64 * mm, "offsetDistance" : 25.4 * mm});
        }
        {
            var Q0;
            Q0=makeQuery(id+"FVh3tlYzcA9VAN6_3.merge.FVRMiynpMZOIpZJ.importOp","IMPORT",FACE,{"importTag":51.0});
            cPoint(context, id + "F4", {"pointType" : PointType.MESH_POINT, "mesh" : qUnion([Q0]), "x" : -795.96 * mm, "y" : -953.14 * mm, "z" : 373.9 * mm});
        }
        {
            var Q0;
            Q0=makeQuery(id+"F1.opExtrude","SWEPT_BODY",BODY,{"disambiguationData":[OSD([sQuery(id+"F0.wireOp",EDGE,"E33"),sQuery(id+"F0.wireOp",EDGE,"E34"),sQuery(id+"F0.wireOp",EDGE,"E35"),sQuery(id+"F0.wireOp",EDGE,"E36")])]});
            var Q1;
            Q1=makeQuery(id+"F1.opExtrude","SWEPT_BODY",BODY,{"disambiguationData":[OSD([sQuery(id+"F0.wireOp",EDGE,"E283"),sQuery(id+"F0.wireOp",EDGE,"E284"),sQuery(id+"F0.wireOp",EDGE,"E285"),sQuery(id+"F0.wireOp",EDGE,"E286"),sQuery(id+"F0.wireOp",EDGE,"E287"),sQuery(id+"F0.wireOp",EDGE,"E288"),sQuery(id+"F0.wireOp",EDGE,"E289"),sQuery(id+"F0.wireOp",EDGE,"E290")])]});
            var Q2;
            Q2=makeQuery(id+"F1.opExtrude","SWEPT_BODY",BODY,{"disambiguationData":[OSD([sQuery(id+"F0.wireOp",EDGE,"E295"),sQuery(id+"F0.wireOp",EDGE,"E296"),sQuery(id+"F0.wireOp",EDGE,"E297"),sQuery(id+"F0.wireOp",EDGE,"E298")])]});
            var Q3;
            Q3=makeQuery(id+"FVh3tlYzcA9VAN6_3.merge.FVRMiynpMZOIpZJ.importOp","IMPORT",BODY,{"importTag":1.0});
            var Q4;
            Q4=makeQuery(id+"FVh3tlYzcA9VAN6_3.merge.FVRMiynpMZOIpZJ.importOp","IMPORT",BODY,{"importTag":7.0});
            var Q5;
            Q5=makeQuery(id+"FVh3tlYzcA9VAN6_3.merge.FVRMiynpMZOIpZJ.importOp","IMPORT",BODY,{"importTag":10.0});
            var Q6;
            Q6=makeQuery(id+"FVh3tlYzcA9VAN6_3.merge.FVRMiynpMZOIpZJ.importOp","IMPORT",BODY,{"importTag":22.0});
            var Q7;
            Q7=makeQuery(id+"FVh3tlYzcA9VAN6_3.merge.FVRMiynpMZOIpZJ.importOp","IMPORT",BODY,{"importTag":25.0});
            var Q8;
            Q8=makeQuery(id+"FVh3tlYzcA9VAN6_3.merge.FVRMiynpMZOIpZJ.importOp","IMPORT",BODY,{"importTag":34.0});
            var Q9;
            Q9=makeQuery(id+"FVh3tlYzcA9VAN6_3.merge.FVRMiynpMZOIpZJ.importOp","IMPORT",BODY,{"importTag":49.0});
            var Q10;
            Q10=makeQuery(id+"FVh3tlYzcA9VAN6_3.merge.FVRMiynpMZOIpZJ.importOp","IMPORT",BODY,{"importTag":52.0});
            var Q11;
            Q11=makeQuery(id+"FVh3tlYzcA9VAN6_3.merge.FVRMiynpMZOIpZJ.importOp","IMPORT",BODY,{"importTag":55.0});
            var Q12;
            Q12=makeQuery(id+"FVh3tlYzcA9VAN6_3.merge.FVRMiynpMZOIpZJ.importOp","IMPORT",BODY,{"importTag":64.0});
            var Q13;
            Q13=makeQuery(id+"FVh3tlYzcA9VAN6_3.merge.FVRMiynpMZOIpZJ.importOp","IMPORT",BODY,{"importTag":82.0});
            var Q14;
            Q14=makeQuery(id+"F3.opExtrude","SWEPT_BODY",BODY,{"disambiguationData":[OSD([sQuery(id+"F2.wireOp",EDGE,"E1216"),sQuery(id+"F2.wireOp",EDGE,"E1217"),sQuery(id+"F2.wireOp",EDGE,"E1218"),sQuery(id+"F2.wireOp",EDGE,"E1219"),sQuery(id+"F2.wireOp",EDGE,"E1220"),sQuery(id+"F2.wireOp",EDGE,"E1221"),sQuery(id+"F2.wireOp",EDGE,"E1222"),sQuery(id+"F2.wireOp",EDGE,"E1223"),sQuery(id+"F2.wireOp",EDGE,"E1224"),sQuery(id+"F2.wireOp",EDGE,"E1225"),sQuery(id+"F2.wireOp",EDGE,"E1226"),sQuery(id+"F2.wireOp",EDGE,"E1227"),sQuery(id+"F2.wireOp",EDGE,"E1228"),sQuery(id+"F2.wireOp",EDGE,"E1229"),sQuery(id+"F2.wireOp",EDGE,"E1230"),sQuery(id+"F2.wireOp",EDGE,"E1231"),sQuery(id+"F2.wireOp",EDGE,"E1232"),sQuery(id+"F2.wireOp",EDGE,"E1240"),sQuery(id+"F2.wireOp",EDGE,"E1241"),sQuery(id+"F2.wireOp",EDGE,"E1242"),sQuery(id+"F2.wireOp",EDGE,"E1243"),sQuery(id+"F2.wireOp",EDGE,"E1244"),sQuery(id+"F2.wireOp",EDGE,"E1245"),sQuery(id+"F2.wireOp",EDGE,"E1246"),sQuery(id+"F2.wireOp",EDGE,"E1247"),sQuery(id+"F2.wireOp",EDGE,"E1248"),sQuery(id+"F2.wireOp",EDGE,"E1249"),sQuery(id+"F2.wireOp",EDGE,"E1250"),sQuery(id+"F2.wireOp",EDGE,"E1251"),sQuery(id+"F2.wireOp",EDGE,"E1252"),sQuery(id+"F2.wireOp",EDGE,"E1253"),sQuery(id+"F2.wireOp",EDGE,"E1254"),sQuery(id+"F2.wireOp",EDGE,"E1255"),sQuery(id+"F2.wireOp",EDGE,"E1256"),sQuery(id+"F2.wireOp",EDGE,"E1257"),sQuery(id+"F2.wireOp",EDGE,"E1258"),sQuery(id+"F2.wireOp",EDGE,"E1259"),sQuery(id+"F2.wireOp",EDGE,"E1260"),sQuery(id+"F2.wireOp",EDGE,"E1261"),sQuery(id+"F2.wireOp",EDGE,"E1262"),sQuery(id+"F2.wireOp",EDGE,"E1263"),sQuery(id+"F2.wireOp",EDGE,"E1264"),sQuery(id+"F2.wireOp",EDGE,"E1265"),sQuery(id+"F2.wireOp",EDGE,"E1266"),sQuery(id+"F2.wireOp",EDGE,"E1267"),sQuery(id+"F2.wireOp",EDGE,"E1268"),sQuery(id+"F2.wireOp",EDGE,"E1269"),sQuery(id+"F2.wireOp",EDGE,"E1270"),sQuery(id+"F2.wireOp",EDGE,"E1271"),sQuery(id+"F2.wireOp",EDGE,"E1272"),sQuery(id+"F2.wireOp",EDGE,"E1273"),sQuery(id+"F2.wireOp",EDGE,"E1274"),sQuery(id+"F2.wireOp",EDGE,"E1275"),sQuery(id+"F2.wireOp",EDGE,"E1276"),sQuery(id+"F2.wireOp",EDGE,"E1277"),sQuery(id+"F2.wireOp",EDGE,"E1278"),sQuery(id+"F2.wireOp",EDGE,"E1279"),sQuery(id+"F2.wireOp",EDGE,"E1280"),sQuery(id+"F2.wireOp",EDGE,"E1281"),sQuery(id+"F2.wireOp",EDGE,"E1282"),sQuery(id+"F2.wireOp",EDGE,"E1283"),sQuery(id+"F2.wireOp",EDGE,"E1284"),sQuery(id+"F2.wireOp",EDGE,"E1285"),sQuery(id+"F2.wireOp",EDGE,"E1286"),sQuery(id+"F2.wireOp",EDGE,"E1287"),sQuery(id+"F2.wireOp",EDGE,"E1288"),sQuery(id+"F2.wireOp",EDGE,"E1289"),sQuery(id+"F2.wireOp",EDGE,"E1290"),sQuery(id+"F2.wireOp",EDGE,"E1291"),sQuery(id+"F2.wireOp",EDGE,"E1292"),sQuery(id+"F2.wireOp",EDGE,"E1293"),sQuery(id+"F2.wireOp",EDGE,"E1294"),sQuery(id+"F2.wireOp",EDGE,"E1295"),sQuery(id+"F2.wireOp",EDGE,"E1296"),sQuery(id+"F2.wireOp",EDGE,"E1297"),sQuery(id+"F2.wireOp",EDGE,"E1298"),sQuery(id+"F2.wireOp",EDGE,"E1299"),sQuery(id+"F2.wireOp",EDGE,"E1300"),sQuery(id+"F2.wireOp",EDGE,"E1301"),sQuery(id+"F2.wireOp",EDGE,"E1302"),sQuery(id+"F2.wireOp",EDGE,"E1303"),sQuery(id+"F2.wireOp",EDGE,"E1304"),sQuery(id+"F2.wireOp",EDGE,"E1305"),sQuery(id+"F2.wireOp",EDGE,"E1306"),sQuery(id+"F2.wireOp",EDGE,"E1307"),sQuery(id+"F2.wireOp",EDGE,"E1308"),sQuery(id+"F2.wireOp",EDGE,"E1309"),sQuery(id+"F2.wireOp",EDGE,"E1310"),sQuery(id+"F2.wireOp",EDGE,"E1311"),sQuery(id+"F2.wireOp",EDGE,"E1312"),sQuery(id+"F2.wireOp",EDGE,"E1313"),sQuery(id+"F2.wireOp",EDGE,"E1314"),sQuery(id+"F2.wireOp",EDGE,"E1315"),sQuery(id+"F2.wireOp",EDGE,"E1316"),sQuery(id+"F2.wireOp",EDGE,"E1317"),sQuery(id+"F2.wireOp",EDGE,"E1318"),sQuery(id+"F2.wireOp",EDGE,"E1319"),sQuery(id+"F2.wireOp",EDGE,"E1320"),sQuery(id+"F2.wireOp",EDGE,"E1321"),sQuery(id+"F2.wireOp",EDGE,"E1322"),sQuery(id+"F2.wireOp",EDGE,"E1323"),sQuery(id+"F2.wireOp",EDGE,"E1324"),sQuery(id+"F2.wireOp",EDGE,"E1325"),sQuery(id+"F2.wireOp",EDGE,"E1326"),sQuery(id+"F2.wireOp",EDGE,"E1327"),sQuery(id+"F2.wireOp",EDGE,"E1328"),sQuery(id+"F2.wireOp",EDGE,"E1329"),sQuery(id+"F2.wireOp",EDGE,"E1330"),sQuery(id+"F2.wireOp",EDGE,"E1331"),sQuery(id+"F2.wireOp",EDGE,"E1332"),sQuery(id+"F2.wireOp",EDGE,"E1333"),sQuery(id+"F2.wireOp",EDGE,"E1334"),sQuery(id+"F2.wireOp",EDGE,"E1233"),sQuery(id+"F2.wireOp",EDGE,"E1234"),sQuery(id+"F2.wireOp",EDGE,"E1235"),sQuery(id+"F2.wireOp",EDGE,"E1236"),sQuery(id+"F2.wireOp",EDGE,"E1237"),sQuery(id+"F2.wireOp",EDGE,"E1238"),sQuery(id+"F2.wireOp",EDGE,"E1335"),sQuery(id+"F2.wireOp",EDGE,"E1239"),sQuery(id+"F2.wireOp",EDGE,"E1336"),sQuery(id+"F2.wireOp",EDGE,"E1337"),sQuery(id+"F2.wireOp",EDGE,"E1338"),sQuery(id+"F2.wireOp",EDGE,"E1339"),sQuery(id+"F2.wireOp",EDGE,"E1340"),sQuery(id+"F2.wireOp",EDGE,"E1341"),sQuery(id+"F2.wireOp",EDGE,"E1342"),sQuery(id+"F2.wireOp",EDGE,"E1343"),sQuery(id+"F2.wireOp",EDGE,"E1344"),sQuery(id+"F2.wireOp",EDGE,"E1345"),sQuery(id+"F2.wireOp",EDGE,"E1346"),sQuery(id+"F2.wireOp",EDGE,"E1347"),sQuery(id+"F2.wireOp",EDGE,"E1348"),sQuery(id+"F2.wireOp",EDGE,"E1349"),sQuery(id+"F2.wireOp",EDGE,"E1350"),sQuery(id+"F2.wireOp",EDGE,"E1351"),sQuery(id+"F2.wireOp",EDGE,"E1352"),sQuery(id+"F2.wireOp",EDGE,"E1353"),sQuery(id+"F2.wireOp",EDGE,"E1354"),sQuery(id+"F2.wireOp",EDGE,"E1355"),sQuery(id+"F2.wireOp",EDGE,"E1356"),sQuery(id+"F2.wireOp",EDGE,"E1357"),sQuery(id+"F2.wireOp",EDGE,"E1358"),sQuery(id+"F2.wireOp",EDGE,"E1359"),sQuery(id+"F2.wireOp",EDGE,"E1360"),sQuery(id+"F2.wireOp",EDGE,"E1361"),sQuery(id+"F2.wireOp",EDGE,"E1362"),sQuery(id+"F2.wireOp",EDGE,"E1363"),sQuery(id+"F2.wireOp",EDGE,"E1364"),sQuery(id+"F2.wireOp",EDGE,"E1365"),sQuery(id+"F2.wireOp",EDGE,"E1366"),sQuery(id+"F2.wireOp",EDGE,"E1367"),sQuery(id+"F2.wireOp",EDGE,"E1368"),sQuery(id+"F2.wireOp",EDGE,"E1369"),sQuery(id+"F2.wireOp",EDGE,"E1370"),sQuery(id+"F2.wireOp",EDGE,"E1371"),sQuery(id+"F2.wireOp",EDGE,"E1372"),sQuery(id+"F2.wireOp",EDGE,"E1373"),sQuery(id+"F2.wireOp",EDGE,"E1374"),sQuery(id+"F2.wireOp",EDGE,"E1375"),sQuery(id+"F2.wireOp",EDGE,"E1376"),sQuery(id+"F2.wireOp",EDGE,"E1377"),sQuery(id+"F2.wireOp",EDGE,"E1378"),sQuery(id+"F2.wireOp",EDGE,"E1379"),sQuery(id+"F2.wireOp",EDGE,"E1380")])]});
            var Q15;
            Q15=makeQuery(id+"FVh3tlYzcA9VAN6_3.merge.FVRMiynpMZOIpZJ.importOp","IMPORT",BODY,{"importTag":4.0});
            var Q16;
            Q16=makeQuery(id+"FVh3tlYzcA9VAN6_3.merge.FVRMiynpMZOIpZJ.importOp","IMPORT",BODY,{"importTag":13.0});
            var Q17;
            Q17=makeQuery(id+"FVh3tlYzcA9VAN6_3.merge.FVRMiynpMZOIpZJ.importOp","IMPORT",BODY,{"importTag":16.0});
            var Q18;
            Q18=makeQuery(id+"FVh3tlYzcA9VAN6_3.merge.FVRMiynpMZOIpZJ.importOp","IMPORT",BODY,{"importTag":19.0});
            var Q19;
            Q19=makeQuery(id+"FVh3tlYzcA9VAN6_3.merge.FVRMiynpMZOIpZJ.importOp","IMPORT",BODY,{"importTag":28.0});
            var Q20;
            Q20=makeQuery(id+"FVh3tlYzcA9VAN6_3.merge.FVRMiynpMZOIpZJ.importOp","IMPORT",BODY,{"importTag":31.0});
            var Q21;
            Q21=makeQuery(id+"FVh3tlYzcA9VAN6_3.merge.FVRMiynpMZOIpZJ.importOp","IMPORT",BODY,{"importTag":37.0});
            var Q22;
            Q22=makeQuery(id+"FVh3tlYzcA9VAN6_3.merge.FVRMiynpMZOIpZJ.importOp","IMPORT",BODY,{"importTag":40.0});
            var Q23;
            Q23=makeQuery(id+"FVh3tlYzcA9VAN6_3.merge.FVRMiynpMZOIpZJ.importOp","IMPORT",BODY,{"importTag":43.0});
            var Q24;
            Q24=makeQuery(id+"FVh3tlYzcA9VAN6_3.merge.FVRMiynpMZOIpZJ.importOp","IMPORT",BODY,{"importTag":46.0});
            var Q25;
            Q25=makeQuery(id+"FVh3tlYzcA9VAN6_3.merge.FVRMiynpMZOIpZJ.importOp","IMPORT",BODY,{"importTag":61.0});
            var Q26;
            Q26=makeQuery(id+"FVh3tlYzcA9VAN6_3.merge.FVRMiynpMZOIpZJ.importOp","IMPORT",BODY,{"importTag":67.0});
            var Q27;
            Q27=makeQuery(id+"FVh3tlYzcA9VAN6_3.merge.FVRMiynpMZOIpZJ.importOp","IMPORT",BODY,{"importTag":76.0});
            var Q28;
            Q28=makeQuery(id+"FVh3tlYzcA9VAN6_3.merge.FVRMiynpMZOIpZJ.importOp","IMPORT",BODY,{"importTag":58.0});
            var Q29;
            Q29=makeQuery(id+"FVh3tlYzcA9VAN6_3.merge.FVRMiynpMZOIpZJ.importOp","IMPORT",BODY,{"importTag":70.0});
            var Q30;
            Q30=makeQuery(id+"FVh3tlYzcA9VAN6_3.merge.FVRMiynpMZOIpZJ.importOp","IMPORT",BODY,{"importTag":73.0});
            var Q31;
            Q31=makeQuery(id+"FVh3tlYzcA9VAN6_3.merge.FVRMiynpMZOIpZJ.importOp","IMPORT",BODY,{"importTag":79.0});
            var Q32;
            Q32 = qCreatedBy(id + "F4" ,VERTEX);
            transform(context, id + "F5", {"entities" : qUnion([Q0, Q1, Q2, Q3, Q4, Q5, Q6, Q7, Q8, Q9, Q10, Q11, Q12, Q13, Q14, Q15, Q16, Q17, Q18, Q19, Q20, Q21, Q22, Q23, Q24, Q25, Q26, Q27, Q28, Q29, Q30, Q31]), "transformType" : TransformType.SCALE_UNIFORMLY, "scale" : 0.25, "scalePoint" : qUnion([Q32]), "makeCopy" : false});
        }
        {
            var Q0;
            Q0=makeQuery(id+"F1.opExtrude","SWEPT_BODY",BODY,{"disambiguationData":[OSD([sQuery(id+"F0.wireOp",EDGE,"E33"),sQuery(id+"F0.wireOp",EDGE,"E34"),sQuery(id+"F0.wireOp",EDGE,"E35"),sQuery(id+"F0.wireOp",EDGE,"E36")])]});
            var Q1;
            Q1=makeQuery(id+"F1.opExtrude","SWEPT_BODY",BODY,{"disambiguationData":[OSD([sQuery(id+"F0.wireOp",EDGE,"E283"),sQuery(id+"F0.wireOp",EDGE,"E284"),sQuery(id+"F0.wireOp",EDGE,"E285"),sQuery(id+"F0.wireOp",EDGE,"E286"),sQuery(id+"F0.wireOp",EDGE,"E287"),sQuery(id+"F0.wireOp",EDGE,"E288"),sQuery(id+"F0.wireOp",EDGE,"E289"),sQuery(id+"F0.wireOp",EDGE,"E290")])]});
            var Q2;
            Q2=makeQuery(id+"F1.opExtrude","SWEPT_BODY",BODY,{"disambiguationData":[OSD([sQuery(id+"F0.wireOp",EDGE,"E295"),sQuery(id+"F0.wireOp",EDGE,"E296"),sQuery(id+"F0.wireOp",EDGE,"E297"),sQuery(id+"F0.wireOp",EDGE,"E298")])]});
            var Q3;
            Q3=makeQuery(id+"FVh3tlYzcA9VAN6_3.merge.FVRMiynpMZOIpZJ.importOp","IMPORT",BODY,{"importTag":1.0});
            var Q4;
            Q4=makeQuery(id+"FVh3tlYzcA9VAN6_3.merge.FVRMiynpMZOIpZJ.importOp","IMPORT",BODY,{"importTag":4.0});
            var Q5;
            Q5=makeQuery(id+"FVh3tlYzcA9VAN6_3.merge.FVRMiynpMZOIpZJ.importOp","IMPORT",BODY,{"importTag":7.0});
            var Q6;
            Q6=makeQuery(id+"FVh3tlYzcA9VAN6_3.merge.FVRMiynpMZOIpZJ.importOp","IMPORT",BODY,{"importTag":16.0});
            var Q7;
            Q7=makeQuery(id+"FVh3tlYzcA9VAN6_3.merge.FVRMiynpMZOIpZJ.importOp","IMPORT",BODY,{"importTag":22.0});
            var Q8;
            Q8=makeQuery(id+"FVh3tlYzcA9VAN6_3.merge.FVRMiynpMZOIpZJ.importOp","IMPORT",BODY,{"importTag":31.0});
            var Q9;
            Q9=makeQuery(id+"FVh3tlYzcA9VAN6_3.merge.FVRMiynpMZOIpZJ.importOp","IMPORT",BODY,{"importTag":34.0});
            var Q10;
            Q10=makeQuery(id+"FVh3tlYzcA9VAN6_3.merge.FVRMiynpMZOIpZJ.importOp","IMPORT",BODY,{"importTag":37.0});
            var Q11;
            Q11=makeQuery(id+"FVh3tlYzcA9VAN6_3.merge.FVRMiynpMZOIpZJ.importOp","IMPORT",BODY,{"importTag":49.0});
            var Q12;
            Q12=makeQuery(id+"FVh3tlYzcA9VAN6_3.merge.FVRMiynpMZOIpZJ.importOp","IMPORT",BODY,{"importTag":52.0});
            var Q13;
            Q13=makeQuery(id+"FVh3tlYzcA9VAN6_3.merge.FVRMiynpMZOIpZJ.importOp","IMPORT",BODY,{"importTag":55.0});
            var Q14;
            Q14=makeQuery(id+"FVh3tlYzcA9VAN6_3.merge.FVRMiynpMZOIpZJ.importOp","IMPORT",BODY,{"importTag":64.0});
            var Q15;
            Q15=makeQuery(id+"FVh3tlYzcA9VAN6_3.merge.FVRMiynpMZOIpZJ.importOp","IMPORT",BODY,{"importTag":67.0});
            var Q16;
            Q16=makeQuery(id+"FVh3tlYzcA9VAN6_3.merge.FVRMiynpMZOIpZJ.importOp","IMPORT",BODY,{"importTag":70.0});
            var Q17;
            Q17=makeQuery(id+"FVh3tlYzcA9VAN6_3.merge.FVRMiynpMZOIpZJ.importOp","IMPORT",BODY,{"importTag":82.0});
            var Q18;
            Q18=makeQuery(id+"F3.opExtrude","SWEPT_BODY",BODY,{"disambiguationData":[OSD([sQuery(id+"F2.wireOp",EDGE,"E1216"),sQuery(id+"F2.wireOp",EDGE,"E1217"),sQuery(id+"F2.wireOp",EDGE,"E1218"),sQuery(id+"F2.wireOp",EDGE,"E1219"),sQuery(id+"F2.wireOp",EDGE,"E1220"),sQuery(id+"F2.wireOp",EDGE,"E1221"),sQuery(id+"F2.wireOp",EDGE,"E1222"),sQuery(id+"F2.wireOp",EDGE,"E1223"),sQuery(id+"F2.wireOp",EDGE,"E1224"),sQuery(id+"F2.wireOp",EDGE,"E1225"),sQuery(id+"F2.wireOp",EDGE,"E1226"),sQuery(id+"F2.wireOp",EDGE,"E1227"),sQuery(id+"F2.wireOp",EDGE,"E1228"),sQuery(id+"F2.wireOp",EDGE,"E1229"),sQuery(id+"F2.wireOp",EDGE,"E1230"),sQuery(id+"F2.wireOp",EDGE,"E1231"),sQuery(id+"F2.wireOp",EDGE,"E1232"),sQuery(id+"F2.wireOp",EDGE,"E1240"),sQuery(id+"F2.wireOp",EDGE,"E1241"),sQuery(id+"F2.wireOp",EDGE,"E1242"),sQuery(id+"F2.wireOp",EDGE,"E1243"),sQuery(id+"F2.wireOp",EDGE,"E1244"),sQuery(id+"F2.wireOp",EDGE,"E1245"),sQuery(id+"F2.wireOp",EDGE,"E1246"),sQuery(id+"F2.wireOp",EDGE,"E1247"),sQuery(id+"F2.wireOp",EDGE,"E1248"),sQuery(id+"F2.wireOp",EDGE,"E1249"),sQuery(id+"F2.wireOp",EDGE,"E1250"),sQuery(id+"F2.wireOp",EDGE,"E1251"),sQuery(id+"F2.wireOp",EDGE,"E1252"),sQuery(id+"F2.wireOp",EDGE,"E1253"),sQuery(id+"F2.wireOp",EDGE,"E1254"),sQuery(id+"F2.wireOp",EDGE,"E1255"),sQuery(id+"F2.wireOp",EDGE,"E1256"),sQuery(id+"F2.wireOp",EDGE,"E1257"),sQuery(id+"F2.wireOp",EDGE,"E1258"),sQuery(id+"F2.wireOp",EDGE,"E1259"),sQuery(id+"F2.wireOp",EDGE,"E1260"),sQuery(id+"F2.wireOp",EDGE,"E1261"),sQuery(id+"F2.wireOp",EDGE,"E1262"),sQuery(id+"F2.wireOp",EDGE,"E1263"),sQuery(id+"F2.wireOp",EDGE,"E1264"),sQuery(id+"F2.wireOp",EDGE,"E1265"),sQuery(id+"F2.wireOp",EDGE,"E1266"),sQuery(id+"F2.wireOp",EDGE,"E1267"),sQuery(id+"F2.wireOp",EDGE,"E1268"),sQuery(id+"F2.wireOp",EDGE,"E1269"),sQuery(id+"F2.wireOp",EDGE,"E1270"),sQuery(id+"F2.wireOp",EDGE,"E1271"),sQuery(id+"F2.wireOp",EDGE,"E1272"),sQuery(id+"F2.wireOp",EDGE,"E1273"),sQuery(id+"F2.wireOp",EDGE,"E1274"),sQuery(id+"F2.wireOp",EDGE,"E1275"),sQuery(id+"F2.wireOp",EDGE,"E1276"),sQuery(id+"F2.wireOp",EDGE,"E1277"),sQuery(id+"F2.wireOp",EDGE,"E1278"),sQuery(id+"F2.wireOp",EDGE,"E1279"),sQuery(id+"F2.wireOp",EDGE,"E1280"),sQuery(id+"F2.wireOp",EDGE,"E1281"),sQuery(id+"F2.wireOp",EDGE,"E1282"),sQuery(id+"F2.wireOp",EDGE,"E1283"),sQuery(id+"F2.wireOp",EDGE,"E1284"),sQuery(id+"F2.wireOp",EDGE,"E1285"),sQuery(id+"F2.wireOp",EDGE,"E1286"),sQuery(id+"F2.wireOp",EDGE,"E1287"),sQuery(id+"F2.wireOp",EDGE,"E1288"),sQuery(id+"F2.wireOp",EDGE,"E1289"),sQuery(id+"F2.wireOp",EDGE,"E1290"),sQuery(id+"F2.wireOp",EDGE,"E1291"),sQuery(id+"F2.wireOp",EDGE,"E1292"),sQuery(id+"F2.wireOp",EDGE,"E1293"),sQuery(id+"F2.wireOp",EDGE,"E1294"),sQuery(id+"F2.wireOp",EDGE,"E1295"),sQuery(id+"F2.wireOp",EDGE,"E1296"),sQuery(id+"F2.wireOp",EDGE,"E1297"),sQuery(id+"F2.wireOp",EDGE,"E1298"),sQuery(id+"F2.wireOp",EDGE,"E1299"),sQuery(id+"F2.wireOp",EDGE,"E1300"),sQuery(id+"F2.wireOp",EDGE,"E1301"),sQuery(id+"F2.wireOp",EDGE,"E1302"),sQuery(id+"F2.wireOp",EDGE,"E1303"),sQuery(id+"F2.wireOp",EDGE,"E1304"),sQuery(id+"F2.wireOp",EDGE,"E1305"),sQuery(id+"F2.wireOp",EDGE,"E1306"),sQuery(id+"F2.wireOp",EDGE,"E1307"),sQuery(id+"F2.wireOp",EDGE,"E1308"),sQuery(id+"F2.wireOp",EDGE,"E1309"),sQuery(id+"F2.wireOp",EDGE,"E1310"),sQuery(id+"F2.wireOp",EDGE,"E1311"),sQuery(id+"F2.wireOp",EDGE,"E1312"),sQuery(id+"F2.wireOp",EDGE,"E1313"),sQuery(id+"F2.wireOp",EDGE,"E1314"),sQuery(id+"F2.wireOp",EDGE,"E1315"),sQuery(id+"F2.wireOp",EDGE,"E1316"),sQuery(id+"F2.wireOp",EDGE,"E1317"),sQuery(id+"F2.wireOp",EDGE,"E1318"),sQuery(id+"F2.wireOp",EDGE,"E1319"),sQuery(id+"F2.wireOp",EDGE,"E1320"),sQuery(id+"F2.wireOp",EDGE,"E1321"),sQuery(id+"F2.wireOp",EDGE,"E1322"),sQuery(id+"F2.wireOp",EDGE,"E1323"),sQuery(id+"F2.wireOp",EDGE,"E1324"),sQuery(id+"F2.wireOp",EDGE,"E1325"),sQuery(id+"F2.wireOp",EDGE,"E1326"),sQuery(id+"F2.wireOp",EDGE,"E1327"),sQuery(id+"F2.wireOp",EDGE,"E1328"),sQuery(id+"F2.wireOp",EDGE,"E1329"),sQuery(id+"F2.wireOp",EDGE,"E1330"),sQuery(id+"F2.wireOp",EDGE,"E1331"),sQuery(id+"F2.wireOp",EDGE,"E1332"),sQuery(id+"F2.wireOp",EDGE,"E1333"),sQuery(id+"F2.wireOp",EDGE,"E1334"),sQuery(id+"F2.wireOp",EDGE,"E1233"),sQuery(id+"F2.wireOp",EDGE,"E1234"),sQuery(id+"F2.wireOp",EDGE,"E1235"),sQuery(id+"F2.wireOp",EDGE,"E1236"),sQuery(id+"F2.wireOp",EDGE,"E1237"),sQuery(id+"F2.wireOp",EDGE,"E1238"),sQuery(id+"F2.wireOp",EDGE,"E1335"),sQuery(id+"F2.wireOp",EDGE,"E1239"),sQuery(id+"F2.wireOp",EDGE,"E1336"),sQuery(id+"F2.wireOp",EDGE,"E1337"),sQuery(id+"F2.wireOp",EDGE,"E1338"),sQuery(id+"F2.wireOp",EDGE,"E1339"),sQuery(id+"F2.wireOp",EDGE,"E1340"),sQuery(id+"F2.wireOp",EDGE,"E1341"),sQuery(id+"F2.wireOp",EDGE,"E1342"),sQuery(id+"F2.wireOp",EDGE,"E1343"),sQuery(id+"F2.wireOp",EDGE,"E1344"),sQuery(id+"F2.wireOp",EDGE,"E1345"),sQuery(id+"F2.wireOp",EDGE,"E1346"),sQuery(id+"F2.wireOp",EDGE,"E1347"),sQuery(id+"F2.wireOp",EDGE,"E1348"),sQuery(id+"F2.wireOp",EDGE,"E1349"),sQuery(id+"F2.wireOp",EDGE,"E1350"),sQuery(id+"F2.wireOp",EDGE,"E1351"),sQuery(id+"F2.wireOp",EDGE,"E1352"),sQuery(id+"F2.wireOp",EDGE,"E1353"),sQuery(id+"F2.wireOp",EDGE,"E1354"),sQuery(id+"F2.wireOp",EDGE,"E1355"),sQuery(id+"F2.wireOp",EDGE,"E1356"),sQuery(id+"F2.wireOp",EDGE,"E1357"),sQuery(id+"F2.wireOp",EDGE,"E1358"),sQuery(id+"F2.wireOp",EDGE,"E1359"),sQuery(id+"F2.wireOp",EDGE,"E1360"),sQuery(id+"F2.wireOp",EDGE,"E1361"),sQuery(id+"F2.wireOp",EDGE,"E1362"),sQuery(id+"F2.wireOp",EDGE,"E1363"),sQuery(id+"F2.wireOp",EDGE,"E1364"),sQuery(id+"F2.wireOp",EDGE,"E1365"),sQuery(id+"F2.wireOp",EDGE,"E1366"),sQuery(id+"F2.wireOp",EDGE,"E1367"),sQuery(id+"F2.wireOp",EDGE,"E1368"),sQuery(id+"F2.wireOp",EDGE,"E1369"),sQuery(id+"F2.wireOp",EDGE,"E1370"),sQuery(id+"F2.wireOp",EDGE,"E1371"),sQuery(id+"F2.wireOp",EDGE,"E1372"),sQuery(id+"F2.wireOp",EDGE,"E1373"),sQuery(id+"F2.wireOp",EDGE,"E1374"),sQuery(id+"F2.wireOp",EDGE,"E1375"),sQuery(id+"F2.wireOp",EDGE,"E1376"),sQuery(id+"F2.wireOp",EDGE,"E1377"),sQuery(id+"F2.wireOp",EDGE,"E1378"),sQuery(id+"F2.wireOp",EDGE,"E1379"),sQuery(id+"F2.wireOp",EDGE,"E1380")])]});
            var Q19;
            Q19=makeQuery(id+"FVh3tlYzcA9VAN6_3.merge.FVRMiynpMZOIpZJ.importOp","IMPORT",BODY,{"importTag":10.0});
            var Q20;
            Q20=makeQuery(id+"FVh3tlYzcA9VAN6_3.merge.FVRMiynpMZOIpZJ.importOp","IMPORT",BODY,{"importTag":13.0});
            var Q21;
            Q21=makeQuery(id+"FVh3tlYzcA9VAN6_3.merge.FVRMiynpMZOIpZJ.importOp","IMPORT",BODY,{"importTag":19.0});
            var Q22;
            Q22=makeQuery(id+"FVh3tlYzcA9VAN6_3.merge.FVRMiynpMZOIpZJ.importOp","IMPORT",BODY,{"importTag":25.0});
            var Q23;
            Q23=makeQuery(id+"FVh3tlYzcA9VAN6_3.merge.FVRMiynpMZOIpZJ.importOp","IMPORT",BODY,{"importTag":28.0});
            var Q24;
            Q24=makeQuery(id+"FVh3tlYzcA9VAN6_3.merge.FVRMiynpMZOIpZJ.importOp","IMPORT",BODY,{"importTag":40.0});
            var Q25;
            Q25=makeQuery(id+"FVh3tlYzcA9VAN6_3.merge.FVRMiynpMZOIpZJ.importOp","IMPORT",BODY,{"importTag":43.0});
            var Q26;
            Q26=makeQuery(id+"FVh3tlYzcA9VAN6_3.merge.FVRMiynpMZOIpZJ.importOp","IMPORT",BODY,{"importTag":46.0});
            var Q27;
            Q27=makeQuery(id+"FVh3tlYzcA9VAN6_3.merge.FVRMiynpMZOIpZJ.importOp","IMPORT",BODY,{"importTag":58.0});
            var Q28;
            Q28=makeQuery(id+"FVh3tlYzcA9VAN6_3.merge.FVRMiynpMZOIpZJ.importOp","IMPORT",BODY,{"importTag":73.0});
            var Q29;
            Q29=makeQuery(id+"FVh3tlYzcA9VAN6_3.merge.FVRMiynpMZOIpZJ.importOp","IMPORT",BODY,{"importTag":76.0});
            var Q30;
            Q30=makeQuery(id+"FVh3tlYzcA9VAN6_3.merge.FVRMiynpMZOIpZJ.importOp","IMPORT",BODY,{"importTag":61.0});
            var Q31;
            Q31=makeQuery(id+"FVh3tlYzcA9VAN6_3.merge.FVRMiynpMZOIpZJ.importOp","IMPORT",BODY,{"importTag":79.0});
            var Q32;
            Q32=sQuery(id+"FEYRCoBc2ZQ7YS5_32.wireOp",EDGE,"BM2Z26Vd-yEVH-hGly-ram6-ONDVGuDeOsyx");
            transform(context, id + "F6", {"entities" : qUnion([Q0, Q1, Q2, Q3, Q4, Q5, Q6, Q7, Q8, Q9, Q10, Q11, Q12, Q13, Q14, Q15, Q16, Q17, Q18, Q19, Q20, Q21, Q22, Q23, Q24, Q25, Q26, Q27, Q28, Q29, Q30, Q31]), "transformType" : TransformType.TRANSLATION_3D, "dx" : 571.5 * mm, "dy" : 698.5 * mm, "dz" : 0 * mm, "makeCopy" : false});
        }
        {
            var Q0;
            Q0=makeQuery(id+"F1.opExtrude","SWEPT_BODY",BODY,{"disambiguationData":[OSD([sQuery(id+"F0.wireOp",EDGE,"E283"),sQuery(id+"F0.wireOp",EDGE,"E284"),sQuery(id+"F0.wireOp",EDGE,"E285"),sQuery(id+"F0.wireOp",EDGE,"E286"),sQuery(id+"F0.wireOp",EDGE,"E287"),sQuery(id+"F0.wireOp",EDGE,"E288"),sQuery(id+"F0.wireOp",EDGE,"E289"),sQuery(id+"F0.wireOp",EDGE,"E290")])]});
            var Q1;
            Q1=makeQuery(id+"F1.opExtrude","SWEPT_BODY",BODY,{"disambiguationData":[OSD([sQuery(id+"F0.wireOp",EDGE,"E33"),sQuery(id+"F0.wireOp",EDGE,"E34"),sQuery(id+"F0.wireOp",EDGE,"E35"),sQuery(id+"F0.wireOp",EDGE,"E36")])]});
            var Q2;
            Q2=makeQuery(id+"F3.opExtrude","SWEPT_BODY",BODY,{"disambiguationData":[OSD([sQuery(id+"F2.wireOp",EDGE,"E1216"),sQuery(id+"F2.wireOp",EDGE,"E1217"),sQuery(id+"F2.wireOp",EDGE,"E1218"),sQuery(id+"F2.wireOp",EDGE,"E1219"),sQuery(id+"F2.wireOp",EDGE,"E1220"),sQuery(id+"F2.wireOp",EDGE,"E1221"),sQuery(id+"F2.wireOp",EDGE,"E1222"),sQuery(id+"F2.wireOp",EDGE,"E1223"),sQuery(id+"F2.wireOp",EDGE,"E1224"),sQuery(id+"F2.wireOp",EDGE,"E1225"),sQuery(id+"F2.wireOp",EDGE,"E1226"),sQuery(id+"F2.wireOp",EDGE,"E1227"),sQuery(id+"F2.wireOp",EDGE,"E1228"),sQuery(id+"F2.wireOp",EDGE,"E1229"),sQuery(id+"F2.wireOp",EDGE,"E1230"),sQuery(id+"F2.wireOp",EDGE,"E1231"),sQuery(id+"F2.wireOp",EDGE,"E1232"),sQuery(id+"F2.wireOp",EDGE,"E1240"),sQuery(id+"F2.wireOp",EDGE,"E1241"),sQuery(id+"F2.wireOp",EDGE,"E1242"),sQuery(id+"F2.wireOp",EDGE,"E1243"),sQuery(id+"F2.wireOp",EDGE,"E1244"),sQuery(id+"F2.wireOp",EDGE,"E1245"),sQuery(id+"F2.wireOp",EDGE,"E1246"),sQuery(id+"F2.wireOp",EDGE,"E1247"),sQuery(id+"F2.wireOp",EDGE,"E1248"),sQuery(id+"F2.wireOp",EDGE,"E1249"),sQuery(id+"F2.wireOp",EDGE,"E1250"),sQuery(id+"F2.wireOp",EDGE,"E1251"),sQuery(id+"F2.wireOp",EDGE,"E1252"),sQuery(id+"F2.wireOp",EDGE,"E1253"),sQuery(id+"F2.wireOp",EDGE,"E1254"),sQuery(id+"F2.wireOp",EDGE,"E1255"),sQuery(id+"F2.wireOp",EDGE,"E1256"),sQuery(id+"F2.wireOp",EDGE,"E1257"),sQuery(id+"F2.wireOp",EDGE,"E1258"),sQuery(id+"F2.wireOp",EDGE,"E1259"),sQuery(id+"F2.wireOp",EDGE,"E1260"),sQuery(id+"F2.wireOp",EDGE,"E1261"),sQuery(id+"F2.wireOp",EDGE,"E1262"),sQuery(id+"F2.wireOp",EDGE,"E1263"),sQuery(id+"F2.wireOp",EDGE,"E1264"),sQuery(id+"F2.wireOp",EDGE,"E1265"),sQuery(id+"F2.wireOp",EDGE,"E1266"),sQuery(id+"F2.wireOp",EDGE,"E1267"),sQuery(id+"F2.wireOp",EDGE,"E1268"),sQuery(id+"F2.wireOp",EDGE,"E1269"),sQuery(id+"F2.wireOp",EDGE,"E1270"),sQuery(id+"F2.wireOp",EDGE,"E1271"),sQuery(id+"F2.wireOp",EDGE,"E1272"),sQuery(id+"F2.wireOp",EDGE,"E1273"),sQuery(id+"F2.wireOp",EDGE,"E1274"),sQuery(id+"F2.wireOp",EDGE,"E1275"),sQuery(id+"F2.wireOp",EDGE,"E1276"),sQuery(id+"F2.wireOp",EDGE,"E1277"),sQuery(id+"F2.wireOp",EDGE,"E1278"),sQuery(id+"F2.wireOp",EDGE,"E1279"),sQuery(id+"F2.wireOp",EDGE,"E1280"),sQuery(id+"F2.wireOp",EDGE,"E1281"),sQuery(id+"F2.wireOp",EDGE,"E1282"),sQuery(id+"F2.wireOp",EDGE,"E1283"),sQuery(id+"F2.wireOp",EDGE,"E1284"),sQuery(id+"F2.wireOp",EDGE,"E1285"),sQuery(id+"F2.wireOp",EDGE,"E1286"),sQuery(id+"F2.wireOp",EDGE,"E1287"),sQuery(id+"F2.wireOp",EDGE,"E1288"),sQuery(id+"F2.wireOp",EDGE,"E1289"),sQuery(id+"F2.wireOp",EDGE,"E1290"),sQuery(id+"F2.wireOp",EDGE,"E1291"),sQuery(id+"F2.wireOp",EDGE,"E1292"),sQuery(id+"F2.wireOp",EDGE,"E1293"),sQuery(id+"F2.wireOp",EDGE,"E1294"),sQuery(id+"F2.wireOp",EDGE,"E1295"),sQuery(id+"F2.wireOp",EDGE,"E1296"),sQuery(id+"F2.wireOp",EDGE,"E1297"),sQuery(id+"F2.wireOp",EDGE,"E1298"),sQuery(id+"F2.wireOp",EDGE,"E1299"),sQuery(id+"F2.wireOp",EDGE,"E1300"),sQuery(id+"F2.wireOp",EDGE,"E1301"),sQuery(id+"F2.wireOp",EDGE,"E1302"),sQuery(id+"F2.wireOp",EDGE,"E1303"),sQuery(id+"F2.wireOp",EDGE,"E1304"),sQuery(id+"F2.wireOp",EDGE,"E1305"),sQuery(id+"F2.wireOp",EDGE,"E1306"),sQuery(id+"F2.wireOp",EDGE,"E1307"),sQuery(id+"F2.wireOp",EDGE,"E1308"),sQuery(id+"F2.wireOp",EDGE,"E1309"),sQuery(id+"F2.wireOp",EDGE,"E1310"),sQuery(id+"F2.wireOp",EDGE,"E1311"),sQuery(id+"F2.wireOp",EDGE,"E1312"),sQuery(id+"F2.wireOp",EDGE,"E1313"),sQuery(id+"F2.wireOp",EDGE,"E1314"),sQuery(id+"F2.wireOp",EDGE,"E1315"),sQuery(id+"F2.wireOp",EDGE,"E1316"),sQuery(id+"F2.wireOp",EDGE,"E1317"),sQuery(id+"F2.wireOp",EDGE,"E1318"),sQuery(id+"F2.wireOp",EDGE,"E1319"),sQuery(id+"F2.wireOp",EDGE,"E1320"),sQuery(id+"F2.wireOp",EDGE,"E1321"),sQuery(id+"F2.wireOp",EDGE,"E1322"),sQuery(id+"F2.wireOp",EDGE,"E1323"),sQuery(id+"F2.wireOp",EDGE,"E1324"),sQuery(id+"F2.wireOp",EDGE,"E1325"),sQuery(id+"F2.wireOp",EDGE,"E1326"),sQuery(id+"F2.wireOp",EDGE,"E1327"),sQuery(id+"F2.wireOp",EDGE,"E1328"),sQuery(id+"F2.wireOp",EDGE,"E1329"),sQuery(id+"F2.wireOp",EDGE,"E1330"),sQuery(id+"F2.wireOp",EDGE,"E1331"),sQuery(id+"F2.wireOp",EDGE,"E1332"),sQuery(id+"F2.wireOp",EDGE,"E1333"),sQuery(id+"F2.wireOp",EDGE,"E1334"),sQuery(id+"F2.wireOp",EDGE,"E1233"),sQuery(id+"F2.wireOp",EDGE,"E1234"),sQuery(id+"F2.wireOp",EDGE,"E1235"),sQuery(id+"F2.wireOp",EDGE,"E1236"),sQuery(id+"F2.wireOp",EDGE,"E1237"),sQuery(id+"F2.wireOp",EDGE,"E1238"),sQuery(id+"F2.wireOp",EDGE,"E1335"),sQuery(id+"F2.wireOp",EDGE,"E1239"),sQuery(id+"F2.wireOp",EDGE,"E1336"),sQuery(id+"F2.wireOp",EDGE,"E1337"),sQuery(id+"F2.wireOp",EDGE,"E1338"),sQuery(id+"F2.wireOp",EDGE,"E1339"),sQuery(id+"F2.wireOp",EDGE,"E1340"),sQuery(id+"F2.wireOp",EDGE,"E1341"),sQuery(id+"F2.wireOp",EDGE,"E1342"),sQuery(id+"F2.wireOp",EDGE,"E1343"),sQuery(id+"F2.wireOp",EDGE,"E1344"),sQuery(id+"F2.wireOp",EDGE,"E1345"),sQuery(id+"F2.wireOp",EDGE,"E1346"),sQuery(id+"F2.wireOp",EDGE,"E1347"),sQuery(id+"F2.wireOp",EDGE,"E1348"),sQuery(id+"F2.wireOp",EDGE,"E1349"),sQuery(id+"F2.wireOp",EDGE,"E1350"),sQuery(id+"F2.wireOp",EDGE,"E1351"),sQuery(id+"F2.wireOp",EDGE,"E1352"),sQuery(id+"F2.wireOp",EDGE,"E1353"),sQuery(id+"F2.wireOp",EDGE,"E1354"),sQuery(id+"F2.wireOp",EDGE,"E1355"),sQuery(id+"F2.wireOp",EDGE,"E1356"),sQuery(id+"F2.wireOp",EDGE,"E1357"),sQuery(id+"F2.wireOp",EDGE,"E1358"),sQuery(id+"F2.wireOp",EDGE,"E1359"),sQuery(id+"F2.wireOp",EDGE,"E1360"),sQuery(id+"F2.wireOp",EDGE,"E1361"),sQuery(id+"F2.wireOp",EDGE,"E1362"),sQuery(id+"F2.wireOp",EDGE,"E1363"),sQuery(id+"F2.wireOp",EDGE,"E1364"),sQuery(id+"F2.wireOp",EDGE,"E1365"),sQuery(id+"F2.wireOp",EDGE,"E1366"),sQuery(id+"F2.wireOp",EDGE,"E1367"),sQuery(id+"F2.wireOp",EDGE,"E1368"),sQuery(id+"F2.wireOp",EDGE,"E1369"),sQuery(id+"F2.wireOp",EDGE,"E1370"),sQuery(id+"F2.wireOp",EDGE,"E1371"),sQuery(id+"F2.wireOp",EDGE,"E1372"),sQuery(id+"F2.wireOp",EDGE,"E1373"),sQuery(id+"F2.wireOp",EDGE,"E1374"),sQuery(id+"F2.wireOp",EDGE,"E1375"),sQuery(id+"F2.wireOp",EDGE,"E1376"),sQuery(id+"F2.wireOp",EDGE,"E1377"),sQuery(id+"F2.wireOp",EDGE,"E1378"),sQuery(id+"F2.wireOp",EDGE,"E1379"),sQuery(id+"F2.wireOp",EDGE,"E1380")])]});
            var Q3;
            Q3=makeQuery(id+"F1.opExtrude","SWEPT_BODY",BODY,{"disambiguationData":[OSD([sQuery(id+"F0.wireOp",EDGE,"E295"),sQuery(id+"F0.wireOp",EDGE,"E296"),sQuery(id+"F0.wireOp",EDGE,"E297"),sQuery(id+"F0.wireOp",EDGE,"E298")])]});
            transform(context, id + "F7", {"entities" : qUnion([Q0, Q1, Q2, Q3]), "transformType" : TransformType.TRANSLATION_3D, "dx" : 0 * mm, "dy" : 0 * mm, "dz" : -278.93 * mm, "makeCopy" : false});
        }
    });
